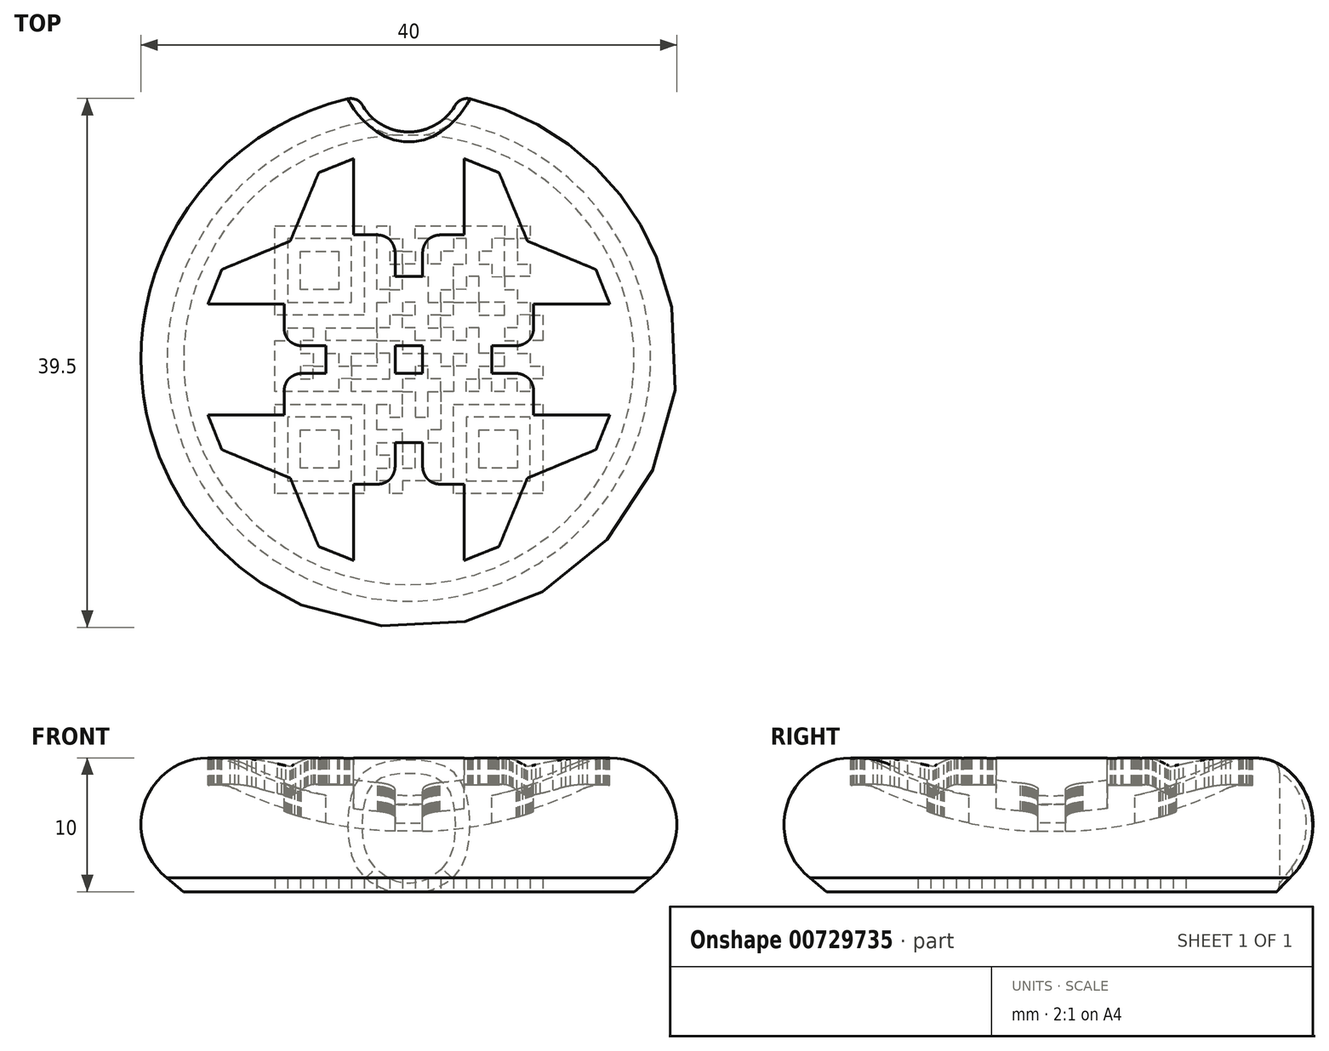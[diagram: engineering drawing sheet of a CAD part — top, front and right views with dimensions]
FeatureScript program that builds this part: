
annotation { "Feature Type Name" : "Feature", "Feature Type Description" : "" }
export const myFeature = defineFeature(function(context is Context, id is Id, definition is map)
    precondition{}
    {
        {
            var Q0;
            Q0=qCreatedBy(makeId("Front.planeOp"),FACE);
            var sketch = newSketch(context, id + "F0", { "sketchPlane" : qUnion([Q0])});
            skArc(sketch, "E0", {"start": v(-12.79, 9.48) * mm, "mid": v(-6.57, 7.26) * mm, "end": v(0, 6.5) * mm});
            skArc(sketch, "E1", {"start": v(-12.79, 9.48) * mm, "mid": v(-19.87, 6.14) * mm, "end": v(-15, 0) * mm});
            skLineSegment(sketch, "E2", {"start": v(0, 0) * mm, "end": v(-15, 0) * mm});
            skLineSegment(sketch, "E3", {"start": v(0, 0) * mm, "end": v(0, 6.5) * mm});
            skLineSegment(sketch, "E4", {"start": v(-18.21, 1.17) * mm, "end": v(-16.82, 0) * mm});
            skLineSegment(sketch, "E5", {"start": v(-16.82, 0) * mm, "end": v(-15, 0) * mm});
            skSolve(sketch);
        }
        {
            var Q0;
            Q0=qSketchRegion(id+"F0",true);
            var Q1;
            Q1=sQuery(id+"F0.wireOp",EDGE,"E3");
            revolve(context, id + "F1", {"surfaceOperationType" : NewSurfaceOperationType.NEW, "entities" : qUnion([Q0]), "axis" : qUnion([Q1]), "revolveType" : RevolveType.FULL});
        }
        {
            var Q0;
            Q0=qCreatedBy(makeId("Top.planeOp"),FACE);
            cPlane(context, id + "F2", {"entities" : qUnion([Q0]), "cplaneType" : CPlaneType.OFFSET, "offset" : 15 * mm, "width" : 150 * mm, "height" : 150 * mm});
        }
        {
            var Q0;
            Q0=qCreatedBy(id+"F2.planeOp",FACE);
            var sketch = newSketch(context, id + "F3", { "sketchPlane" : qUnion([Q0])});
            skLineSegment(sketch, "E6", {"start": v(9.31, -4.14) * mm, "end": v(9.31, -4.02) * mm});
            skLineSegment(sketch, "E7", {"start": v(9.31, -4.02) * mm, "end": v(9.31, -3.91) * mm});
            skLineSegment(sketch, "E8", {"start": v(9.31, -3.91) * mm, "end": v(9.31, -3.8) * mm});
            skLineSegment(sketch, "E9", {"start": v(9.31, -3.8) * mm, "end": v(9.31, -3.69) * mm});
            skLineSegment(sketch, "E10", {"start": v(9.31, -3.69) * mm, "end": v(9.31, -3.57) * mm});
            skLineSegment(sketch, "E11", {"start": v(9.31, -3.57) * mm, "end": v(9.31, -3.46) * mm});
            skLineSegment(sketch, "E12", {"start": v(9.31, -3.46) * mm, "end": v(9.31, -3.35) * mm});
            skLineSegment(sketch, "E13", {"start": v(9.31, -3.35) * mm, "end": v(9.31, -3.23) * mm});
            skLineSegment(sketch, "E14", {"start": v(9.31, -3.23) * mm, "end": v(9.31, -3.12) * mm});
            skLineSegment(sketch, "E15", {"start": v(9.31, -3.12) * mm, "end": v(9.31, -3) * mm});
            skLineSegment(sketch, "E16", {"start": v(9.31, -3) * mm, "end": v(9.31, -2.9) * mm});
            skLineSegment(sketch, "E17", {"start": v(9.31, -2.9) * mm, "end": v(9.31, -2.78) * mm});
            skLineSegment(sketch, "E18", {"start": v(9.31, -2.78) * mm, "end": v(9.31, -2.67) * mm});
            skLineSegment(sketch, "E19", {"start": v(9.31, -2.67) * mm, "end": v(9.31, -2.55) * mm});
            skLineSegment(sketch, "E20", {"start": v(9.31, -2.55) * mm, "end": v(9.31, -2.44) * mm});
            skLineSegment(sketch, "E21", {"start": v(9.31, -2.44) * mm, "end": v(9.31, -2.33) * mm});
            skLineSegment(sketch, "E22", {"start": v(9.31, -2.33) * mm, "end": v(9.3, -2.2) * mm});
            skLineSegment(sketch, "E23", {"start": v(9.3, -2.2) * mm, "end": v(9.28, -2.07) * mm});
            skLineSegment(sketch, "E24", {"start": v(9.28, -2.07) * mm, "end": v(9.25, -1.94) * mm});
            skLineSegment(sketch, "E25", {"start": v(9.25, -1.94) * mm, "end": v(9.2, -1.82) * mm});
            skLineSegment(sketch, "E26", {"start": v(9.2, -1.82) * mm, "end": v(9.15, -1.71) * mm});
            skLineSegment(sketch, "E27", {"start": v(9.15, -1.71) * mm, "end": v(9.09, -1.6) * mm});
            skLineSegment(sketch, "E28", {"start": v(9.09, -1.6) * mm, "end": v(9.02, -1.5) * mm});
            skLineSegment(sketch, "E29", {"start": v(9.02, -1.5) * mm, "end": v(8.93, -1.41) * mm});
            skLineSegment(sketch, "E30", {"start": v(8.93, -1.41) * mm, "end": v(8.84, -1.33) * mm});
            skLineSegment(sketch, "E31", {"start": v(8.84, -1.33) * mm, "end": v(8.74, -1.26) * mm});
            skLineSegment(sketch, "E32", {"start": v(8.74, -1.26) * mm, "end": v(8.63, -1.2) * mm});
            skLineSegment(sketch, "E33", {"start": v(8.63, -1.2) * mm, "end": v(8.52, -1.14) * mm});
            skLineSegment(sketch, "E34", {"start": v(8.52, -1.14) * mm, "end": v(8.4, -1.1) * mm});
            skLineSegment(sketch, "E35", {"start": v(8.4, -1.1) * mm, "end": v(8.28, -1.06) * mm});
            skLineSegment(sketch, "E36", {"start": v(8.28, -1.06) * mm, "end": v(8.15, -1.04) * mm});
            skLineSegment(sketch, "E37", {"start": v(8.15, -1.04) * mm, "end": v(8.02, -1.03) * mm});
            skLineSegment(sketch, "E38", {"start": v(8.02, -1.03) * mm, "end": v(7.9, -1.03) * mm});
            skLineSegment(sketch, "E39", {"start": v(7.9, -1.03) * mm, "end": v(7.8, -1.03) * mm});
            skLineSegment(sketch, "E40", {"start": v(7.8, -1.03) * mm, "end": v(7.68, -1.03) * mm});
            skLineSegment(sketch, "E41", {"start": v(7.68, -1.03) * mm, "end": v(7.56, -1.03) * mm});
            skLineSegment(sketch, "E42", {"start": v(7.56, -1.03) * mm, "end": v(7.45, -1.03) * mm});
            skLineSegment(sketch, "E43", {"start": v(7.45, -1.03) * mm, "end": v(7.34, -1.03) * mm});
            skLineSegment(sketch, "E44", {"start": v(7.34, -1.03) * mm, "end": v(7.23, -1.03) * mm});
            skLineSegment(sketch, "E45", {"start": v(7.23, -1.03) * mm, "end": v(7.11, -1.03) * mm});
            skLineSegment(sketch, "E46", {"start": v(7.11, -1.03) * mm, "end": v(7, -1.03) * mm});
            skLineSegment(sketch, "E47", {"start": v(7, -1.03) * mm, "end": v(6.89, -1.03) * mm});
            skLineSegment(sketch, "E48", {"start": v(6.89, -1.03) * mm, "end": v(6.77, -1.03) * mm});
            skLineSegment(sketch, "E49", {"start": v(6.77, -1.03) * mm, "end": v(6.66, -1.03) * mm});
            skLineSegment(sketch, "E50", {"start": v(6.66, -1.03) * mm, "end": v(6.55, -1.03) * mm});
            skLineSegment(sketch, "E51", {"start": v(6.55, -1.03) * mm, "end": v(6.43, -1.03) * mm});
            skLineSegment(sketch, "E52", {"start": v(6.43, -1.03) * mm, "end": v(6.32, -1.03) * mm});
            skLineSegment(sketch, "E53", {"start": v(6.32, -1.03) * mm, "end": v(6.2, -1.03) * mm});
            skLineSegment(sketch, "E54", {"start": v(6.2, -1.03) * mm, "end": v(6.2, -0.97) * mm});
            skLineSegment(sketch, "E55", {"start": v(6.2, -0.97) * mm, "end": v(6.2, -0.9) * mm});
            skLineSegment(sketch, "E56", {"start": v(6.2, -0.9) * mm, "end": v(6.2, -0.84) * mm});
            skLineSegment(sketch, "E57", {"start": v(6.2, -0.84) * mm, "end": v(6.2, -0.78) * mm});
            skLineSegment(sketch, "E58", {"start": v(6.2, -0.78) * mm, "end": v(6.2, -0.71) * mm});
            skLineSegment(sketch, "E59", {"start": v(6.2, -0.71) * mm, "end": v(6.2, -0.65) * mm});
            skLineSegment(sketch, "E60", {"start": v(6.2, -0.65) * mm, "end": v(6.2, -0.58) * mm});
            skLineSegment(sketch, "E61", {"start": v(6.2, -0.58) * mm, "end": v(6.2, -0.52) * mm});
            skLineSegment(sketch, "E62", {"start": v(6.2, -0.52) * mm, "end": v(6.2, -0.45) * mm});
            skLineSegment(sketch, "E63", {"start": v(6.2, -0.45) * mm, "end": v(6.2, -0.39) * mm});
            skLineSegment(sketch, "E64", {"start": v(6.2, -0.39) * mm, "end": v(6.2, -0.32) * mm});
            skLineSegment(sketch, "E65", {"start": v(6.2, -0.32) * mm, "end": v(6.2, -0.26) * mm});
            skLineSegment(sketch, "E66", {"start": v(6.2, -0.26) * mm, "end": v(6.2, -0.2) * mm});
            skLineSegment(sketch, "E67", {"start": v(6.2, -0.2) * mm, "end": v(6.2, -0.13) * mm});
            skLineSegment(sketch, "E68", {"start": v(6.2, -0.13) * mm, "end": v(6.2, -0.06) * mm});
            skLineSegment(sketch, "E69", {"start": v(6.2, -0.06) * mm, "end": v(6.2, 0) * mm});
            skLineSegment(sketch, "E70", {"start": v(6.2, 0) * mm, "end": v(6.2, 0.06) * mm});
            skLineSegment(sketch, "E71", {"start": v(6.2, 0.06) * mm, "end": v(6.2, 0.13) * mm});
            skLineSegment(sketch, "E72", {"start": v(6.2, 0.13) * mm, "end": v(6.2, 0.2) * mm});
            skLineSegment(sketch, "E73", {"start": v(6.2, 0.2) * mm, "end": v(6.2, 0.26) * mm});
            skLineSegment(sketch, "E74", {"start": v(6.2, 0.26) * mm, "end": v(6.2, 0.32) * mm});
            skLineSegment(sketch, "E75", {"start": v(6.2, 0.32) * mm, "end": v(6.2, 0.39) * mm});
            skLineSegment(sketch, "E76", {"start": v(6.2, 0.39) * mm, "end": v(6.2, 0.45) * mm});
            skLineSegment(sketch, "E77", {"start": v(6.2, 0.45) * mm, "end": v(6.2, 0.52) * mm});
            skLineSegment(sketch, "E78", {"start": v(6.2, 0.52) * mm, "end": v(6.2, 0.58) * mm});
            skLineSegment(sketch, "E79", {"start": v(6.2, 0.58) * mm, "end": v(6.2, 0.65) * mm});
            skLineSegment(sketch, "E80", {"start": v(6.2, 0.65) * mm, "end": v(6.2, 0.71) * mm});
            skLineSegment(sketch, "E81", {"start": v(6.2, 0.71) * mm, "end": v(6.2, 0.78) * mm});
            skLineSegment(sketch, "E82", {"start": v(6.2, 0.78) * mm, "end": v(6.2, 0.84) * mm});
            skLineSegment(sketch, "E83", {"start": v(6.2, 0.84) * mm, "end": v(6.2, 0.9) * mm});
            skLineSegment(sketch, "E84", {"start": v(6.2, 0.9) * mm, "end": v(6.2, 0.97) * mm});
            skLineSegment(sketch, "E85", {"start": v(6.2, 0.97) * mm, "end": v(6.2, 1.03) * mm});
            skLineSegment(sketch, "E86", {"start": v(6.2, 1.03) * mm, "end": v(6.32, 1.03) * mm});
            skLineSegment(sketch, "E87", {"start": v(6.32, 1.03) * mm, "end": v(6.43, 1.03) * mm});
            skLineSegment(sketch, "E88", {"start": v(6.43, 1.03) * mm, "end": v(6.55, 1.03) * mm});
            skLineSegment(sketch, "E89", {"start": v(6.55, 1.03) * mm, "end": v(6.66, 1.03) * mm});
            skLineSegment(sketch, "E90", {"start": v(6.66, 1.03) * mm, "end": v(6.77, 1.03) * mm});
            skLineSegment(sketch, "E91", {"start": v(6.77, 1.03) * mm, "end": v(6.89, 1.03) * mm});
            skLineSegment(sketch, "E92", {"start": v(6.89, 1.03) * mm, "end": v(7, 1.03) * mm});
            skLineSegment(sketch, "E93", {"start": v(7, 1.03) * mm, "end": v(7.11, 1.03) * mm});
            skLineSegment(sketch, "E94", {"start": v(7.11, 1.03) * mm, "end": v(7.23, 1.03) * mm});
            skLineSegment(sketch, "E95", {"start": v(7.23, 1.03) * mm, "end": v(7.34, 1.03) * mm});
            skLineSegment(sketch, "E96", {"start": v(7.34, 1.03) * mm, "end": v(7.45, 1.03) * mm});
            skLineSegment(sketch, "E97", {"start": v(7.45, 1.03) * mm, "end": v(7.56, 1.03) * mm});
            skLineSegment(sketch, "E98", {"start": v(7.56, 1.03) * mm, "end": v(7.68, 1.03) * mm});
            skLineSegment(sketch, "E99", {"start": v(7.68, 1.03) * mm, "end": v(7.8, 1.03) * mm});
            skLineSegment(sketch, "E100", {"start": v(7.8, 1.03) * mm, "end": v(7.9, 1.03) * mm});
            skLineSegment(sketch, "E101", {"start": v(7.9, 1.03) * mm, "end": v(8.02, 1.03) * mm});
            skLineSegment(sketch, "E102", {"start": v(8.02, 1.03) * mm, "end": v(8.15, 1.04) * mm});
            skLineSegment(sketch, "E103", {"start": v(8.15, 1.04) * mm, "end": v(8.28, 1.06) * mm});
            skLineSegment(sketch, "E104", {"start": v(8.28, 1.06) * mm, "end": v(8.4, 1.1) * mm});
            skLineSegment(sketch, "E105", {"start": v(8.4, 1.1) * mm, "end": v(8.52, 1.14) * mm});
            skLineSegment(sketch, "E106", {"start": v(8.52, 1.14) * mm, "end": v(8.63, 1.2) * mm});
            skLineSegment(sketch, "E107", {"start": v(8.63, 1.2) * mm, "end": v(8.74, 1.26) * mm});
            skLineSegment(sketch, "E108", {"start": v(8.74, 1.26) * mm, "end": v(8.84, 1.33) * mm});
            skLineSegment(sketch, "E109", {"start": v(8.84, 1.33) * mm, "end": v(8.93, 1.41) * mm});
            skLineSegment(sketch, "E110", {"start": v(8.93, 1.41) * mm, "end": v(9.02, 1.5) * mm});
            skLineSegment(sketch, "E111", {"start": v(9.02, 1.5) * mm, "end": v(9.09, 1.6) * mm});
            skLineSegment(sketch, "E112", {"start": v(9.09, 1.6) * mm, "end": v(9.15, 1.71) * mm});
            skLineSegment(sketch, "E113", {"start": v(9.15, 1.71) * mm, "end": v(9.2, 1.82) * mm});
            skLineSegment(sketch, "E114", {"start": v(9.2, 1.82) * mm, "end": v(9.25, 1.94) * mm});
            skLineSegment(sketch, "E115", {"start": v(9.25, 1.94) * mm, "end": v(9.28, 2.07) * mm});
            skLineSegment(sketch, "E116", {"start": v(9.28, 2.07) * mm, "end": v(9.3, 2.2) * mm});
            skLineSegment(sketch, "E117", {"start": v(9.3, 2.2) * mm, "end": v(9.31, 2.33) * mm});
            skLineSegment(sketch, "E118", {"start": v(9.31, 2.33) * mm, "end": v(9.31, 2.44) * mm});
            skLineSegment(sketch, "E119", {"start": v(9.31, 2.44) * mm, "end": v(9.31, 2.55) * mm});
            skLineSegment(sketch, "E120", {"start": v(9.31, 2.55) * mm, "end": v(9.31, 2.67) * mm});
            skLineSegment(sketch, "E121", {"start": v(9.31, 2.67) * mm, "end": v(9.31, 2.78) * mm});
            skLineSegment(sketch, "E122", {"start": v(9.31, 2.78) * mm, "end": v(9.31, 2.9) * mm});
            skLineSegment(sketch, "E123", {"start": v(9.31, 2.9) * mm, "end": v(9.31, 3) * mm});
            skLineSegment(sketch, "E124", {"start": v(9.31, 3) * mm, "end": v(9.31, 3.12) * mm});
            skLineSegment(sketch, "E125", {"start": v(9.31, 3.12) * mm, "end": v(9.31, 3.23) * mm});
            skLineSegment(sketch, "E126", {"start": v(9.31, 3.23) * mm, "end": v(9.31, 3.35) * mm});
            skLineSegment(sketch, "E127", {"start": v(9.31, 3.35) * mm, "end": v(9.31, 3.46) * mm});
            skLineSegment(sketch, "E128", {"start": v(9.31, 3.46) * mm, "end": v(9.31, 3.57) * mm});
            skLineSegment(sketch, "E129", {"start": v(9.31, 3.57) * mm, "end": v(9.31, 3.69) * mm});
            skLineSegment(sketch, "E130", {"start": v(9.31, 3.69) * mm, "end": v(9.31, 3.8) * mm});
            skLineSegment(sketch, "E131", {"start": v(9.31, 3.8) * mm, "end": v(9.31, 3.91) * mm});
            skLineSegment(sketch, "E132", {"start": v(9.31, 3.91) * mm, "end": v(9.31, 4.02) * mm});
            skLineSegment(sketch, "E133", {"start": v(9.31, 4.02) * mm, "end": v(9.31, 4.14) * mm});
            skLineSegment(sketch, "E134", {"start": v(9.31, 4.14) * mm, "end": v(9.44, 4.14) * mm});
            skLineSegment(sketch, "E135", {"start": v(9.44, 4.14) * mm, "end": v(9.57, 4.14) * mm});
            skLineSegment(sketch, "E136", {"start": v(9.57, 4.14) * mm, "end": v(9.7, 4.14) * mm});
            skLineSegment(sketch, "E137", {"start": v(9.7, 4.14) * mm, "end": v(9.83, 4.14) * mm});
            skLineSegment(sketch, "E138", {"start": v(9.83, 4.14) * mm, "end": v(9.96, 4.14) * mm});
            skLineSegment(sketch, "E139", {"start": v(9.96, 4.14) * mm, "end": v(10.09, 4.14) * mm});
            skLineSegment(sketch, "E140", {"start": v(10.09, 4.14) * mm, "end": v(10.22, 4.14) * mm});
            skLineSegment(sketch, "E141", {"start": v(10.22, 4.14) * mm, "end": v(10.34, 4.14) * mm});
            skLineSegment(sketch, "E142", {"start": v(10.34, 4.14) * mm, "end": v(10.47, 4.14) * mm});
            skLineSegment(sketch, "E143", {"start": v(10.47, 4.14) * mm, "end": v(10.6, 4.14) * mm});
            skLineSegment(sketch, "E144", {"start": v(10.6, 4.14) * mm, "end": v(10.73, 4.14) * mm});
            skLineSegment(sketch, "E145", {"start": v(10.73, 4.14) * mm, "end": v(10.86, 4.14) * mm});
            skLineSegment(sketch, "E146", {"start": v(10.86, 4.14) * mm, "end": v(11, 4.14) * mm});
            skLineSegment(sketch, "E147", {"start": v(11, 4.14) * mm, "end": v(11.12, 4.14) * mm});
            skLineSegment(sketch, "E148", {"start": v(11.12, 4.14) * mm, "end": v(11.25, 4.14) * mm});
            skLineSegment(sketch, "E149", {"start": v(11.25, 4.14) * mm, "end": v(11.38, 4.14) * mm});
            skLineSegment(sketch, "E150", {"start": v(11.38, 4.14) * mm, "end": v(11.6, 4.14) * mm});
            skLineSegment(sketch, "E151", {"start": v(11.6, 4.14) * mm, "end": v(11.83, 4.14) * mm});
            skLineSegment(sketch, "E152", {"start": v(11.83, 4.14) * mm, "end": v(12.06, 4.14) * mm});
            skLineSegment(sketch, "E153", {"start": v(12.06, 4.14) * mm, "end": v(12.28, 4.14) * mm});
            skLineSegment(sketch, "E154", {"start": v(12.28, 4.14) * mm, "end": v(12.51, 4.14) * mm});
            skLineSegment(sketch, "E155", {"start": v(12.51, 4.14) * mm, "end": v(12.74, 4.14) * mm});
            skLineSegment(sketch, "E156", {"start": v(12.74, 4.14) * mm, "end": v(12.96, 4.14) * mm});
            skLineSegment(sketch, "E157", {"start": v(12.96, 4.14) * mm, "end": v(13.19, 4.14) * mm});
            skLineSegment(sketch, "E158", {"start": v(13.19, 4.14) * mm, "end": v(13.42, 4.14) * mm});
            skLineSegment(sketch, "E159", {"start": v(13.42, 4.14) * mm, "end": v(13.64, 4.14) * mm});
            skLineSegment(sketch, "E160", {"start": v(13.64, 4.14) * mm, "end": v(13.87, 4.14) * mm});
            skLineSegment(sketch, "E161", {"start": v(13.87, 4.14) * mm, "end": v(14.1, 4.14) * mm});
            skLineSegment(sketch, "E162", {"start": v(14.1, 4.14) * mm, "end": v(14.32, 4.14) * mm});
            skLineSegment(sketch, "E163", {"start": v(14.32, 4.14) * mm, "end": v(14.55, 4.14) * mm});
            skLineSegment(sketch, "E164", {"start": v(14.55, 4.14) * mm, "end": v(14.77, 4.14) * mm});
            skLineSegment(sketch, "E165", {"start": v(14.77, 4.14) * mm, "end": v(15, 4.14) * mm});
            skLineSegment(sketch, "E166", {"start": v(15, 4.14) * mm, "end": v(14.95, 4.27) * mm});
            skLineSegment(sketch, "E167", {"start": v(14.95, 4.27) * mm, "end": v(14.9, 4.4) * mm});
            skLineSegment(sketch, "E168", {"start": v(14.9, 4.4) * mm, "end": v(14.84, 4.53) * mm});
            skLineSegment(sketch, "E169", {"start": v(14.84, 4.53) * mm, "end": v(14.8, 4.66) * mm});
            skLineSegment(sketch, "E170", {"start": v(14.8, 4.66) * mm, "end": v(14.74, 4.78) * mm});
            skLineSegment(sketch, "E171", {"start": v(14.74, 4.78) * mm, "end": v(14.69, 4.91) * mm});
            skLineSegment(sketch, "E172", {"start": v(14.69, 4.91) * mm, "end": v(14.64, 5.04) * mm});
            skLineSegment(sketch, "E173", {"start": v(14.64, 5.04) * mm, "end": v(14.59, 5.17) * mm});
            skLineSegment(sketch, "E174", {"start": v(14.59, 5.17) * mm, "end": v(14.53, 5.3) * mm});
            skLineSegment(sketch, "E175", {"start": v(14.53, 5.3) * mm, "end": v(14.48, 5.43) * mm});
            skLineSegment(sketch, "E176", {"start": v(14.48, 5.43) * mm, "end": v(14.43, 5.56) * mm});
            skLineSegment(sketch, "E177", {"start": v(14.43, 5.56) * mm, "end": v(14.38, 5.69) * mm});
            skLineSegment(sketch, "E178", {"start": v(14.38, 5.69) * mm, "end": v(14.33, 5.82) * mm});
            skLineSegment(sketch, "E179", {"start": v(14.33, 5.82) * mm, "end": v(14.28, 5.95) * mm});
            skLineSegment(sketch, "E180", {"start": v(14.28, 5.95) * mm, "end": v(14.22, 6.08) * mm});
            skLineSegment(sketch, "E181", {"start": v(14.22, 6.08) * mm, "end": v(14.17, 6.2) * mm});
            skLineSegment(sketch, "E182", {"start": v(14.17, 6.2) * mm, "end": v(14.16, 6.24) * mm});
            skLineSegment(sketch, "E183", {"start": v(14.16, 6.24) * mm, "end": v(14.15, 6.27) * mm});
            skLineSegment(sketch, "E184", {"start": v(14.15, 6.27) * mm, "end": v(14.13, 6.3) * mm});
            skLineSegment(sketch, "E185", {"start": v(14.13, 6.3) * mm, "end": v(14.12, 6.34) * mm});
            skLineSegment(sketch, "E186", {"start": v(14.12, 6.34) * mm, "end": v(14.1, 6.37) * mm});
            skLineSegment(sketch, "E187", {"start": v(14.1, 6.37) * mm, "end": v(14.1, 6.4) * mm});
            skLineSegment(sketch, "E188", {"start": v(14.1, 6.4) * mm, "end": v(14.08, 6.43) * mm});
            skLineSegment(sketch, "E189", {"start": v(14.08, 6.43) * mm, "end": v(14.07, 6.47) * mm});
            skLineSegment(sketch, "E190", {"start": v(14.07, 6.47) * mm, "end": v(14.06, 6.5) * mm});
            skLineSegment(sketch, "E191", {"start": v(14.06, 6.5) * mm, "end": v(14.04, 6.53) * mm});
            skLineSegment(sketch, "E192", {"start": v(14.04, 6.53) * mm, "end": v(14.03, 6.56) * mm});
            skLineSegment(sketch, "E193", {"start": v(14.03, 6.56) * mm, "end": v(14.02, 6.6) * mm});
            skLineSegment(sketch, "E194", {"start": v(14.02, 6.6) * mm, "end": v(14, 6.63) * mm});
            skLineSegment(sketch, "E195", {"start": v(14, 6.63) * mm, "end": v(14, 6.66) * mm});
            skLineSegment(sketch, "E196", {"start": v(14, 6.66) * mm, "end": v(13.98, 6.7) * mm});
            skLineSegment(sketch, "E197", {"start": v(13.98, 6.7) * mm, "end": v(13.97, 6.72) * mm});
            skLineSegment(sketch, "E198", {"start": v(13.97, 6.72) * mm, "end": v(13.65, 6.86) * mm});
            skLineSegment(sketch, "E199", {"start": v(13.65, 6.86) * mm, "end": v(13.33, 7) * mm});
            skLineSegment(sketch, "E200", {"start": v(13.33, 7) * mm, "end": v(13, 7.12) * mm});
            skLineSegment(sketch, "E201", {"start": v(13, 7.12) * mm, "end": v(12.69, 7.26) * mm});
            skLineSegment(sketch, "E202", {"start": v(12.69, 7.26) * mm, "end": v(12.37, 7.39) * mm});
            skLineSegment(sketch, "E203", {"start": v(12.37, 7.39) * mm, "end": v(12.05, 7.52) * mm});
            skLineSegment(sketch, "E204", {"start": v(12.05, 7.52) * mm, "end": v(11.73, 7.66) * mm});
            skLineSegment(sketch, "E205", {"start": v(11.73, 7.66) * mm, "end": v(11.4, 7.79) * mm});
            skLineSegment(sketch, "E206", {"start": v(11.4, 7.79) * mm, "end": v(11.1, 7.92) * mm});
            skLineSegment(sketch, "E207", {"start": v(11.1, 7.92) * mm, "end": v(10.77, 8.06) * mm});
            skLineSegment(sketch, "E208", {"start": v(10.77, 8.06) * mm, "end": v(10.45, 8.19) * mm});
            skLineSegment(sketch, "E209", {"start": v(10.45, 8.19) * mm, "end": v(10.13, 8.32) * mm});
            skLineSegment(sketch, "E210", {"start": v(10.13, 8.32) * mm, "end": v(9.81, 8.45) * mm});
            skLineSegment(sketch, "E211", {"start": v(9.81, 8.45) * mm, "end": v(9.5, 8.59) * mm});
            skLineSegment(sketch, "E212", {"start": v(9.5, 8.59) * mm, "end": v(9.17, 8.72) * mm});
            skLineSegment(sketch, "E213", {"start": v(9.17, 8.72) * mm, "end": v(8.85, 8.85) * mm});
            skLineSegment(sketch, "E214", {"start": v(8.85, 8.85) * mm, "end": v(8.72, 9.17) * mm});
            skLineSegment(sketch, "E215", {"start": v(8.72, 9.17) * mm, "end": v(8.59, 9.5) * mm});
            skLineSegment(sketch, "E216", {"start": v(8.59, 9.5) * mm, "end": v(8.45, 9.81) * mm});
            skLineSegment(sketch, "E217", {"start": v(8.45, 9.81) * mm, "end": v(8.32, 10.13) * mm});
            skLineSegment(sketch, "E218", {"start": v(8.32, 10.13) * mm, "end": v(8.19, 10.45) * mm});
            skLineSegment(sketch, "E219", {"start": v(8.19, 10.45) * mm, "end": v(8.06, 10.77) * mm});
            skLineSegment(sketch, "E220", {"start": v(8.06, 10.77) * mm, "end": v(7.92, 11.1) * mm});
            skLineSegment(sketch, "E221", {"start": v(7.92, 11.1) * mm, "end": v(7.79, 11.4) * mm});
            skLineSegment(sketch, "E222", {"start": v(7.79, 11.4) * mm, "end": v(7.66, 11.73) * mm});
            skLineSegment(sketch, "E223", {"start": v(7.66, 11.73) * mm, "end": v(7.52, 12.05) * mm});
            skLineSegment(sketch, "E224", {"start": v(7.52, 12.05) * mm, "end": v(7.39, 12.37) * mm});
            skLineSegment(sketch, "E225", {"start": v(7.39, 12.37) * mm, "end": v(7.26, 12.69) * mm});
            skLineSegment(sketch, "E226", {"start": v(7.26, 12.69) * mm, "end": v(7.12, 13) * mm});
            skLineSegment(sketch, "E227", {"start": v(7.12, 13) * mm, "end": v(7, 13.33) * mm});
            skLineSegment(sketch, "E228", {"start": v(7, 13.33) * mm, "end": v(6.86, 13.65) * mm});
            skLineSegment(sketch, "E229", {"start": v(6.86, 13.65) * mm, "end": v(6.72, 13.97) * mm});
            skLineSegment(sketch, "E230", {"start": v(6.72, 13.97) * mm, "end": v(6.7, 13.98) * mm});
            skLineSegment(sketch, "E231", {"start": v(6.7, 13.98) * mm, "end": v(6.66, 14) * mm});
            skLineSegment(sketch, "E232", {"start": v(6.66, 14) * mm, "end": v(6.63, 14) * mm});
            skLineSegment(sketch, "E233", {"start": v(6.63, 14) * mm, "end": v(6.6, 14.02) * mm});
            skLineSegment(sketch, "E234", {"start": v(6.6, 14.02) * mm, "end": v(6.56, 14.03) * mm});
            skLineSegment(sketch, "E235", {"start": v(6.56, 14.03) * mm, "end": v(6.53, 14.04) * mm});
            skLineSegment(sketch, "E236", {"start": v(6.53, 14.04) * mm, "end": v(6.5, 14.06) * mm});
            skLineSegment(sketch, "E237", {"start": v(6.5, 14.06) * mm, "end": v(6.47, 14.07) * mm});
            skLineSegment(sketch, "E238", {"start": v(6.47, 14.07) * mm, "end": v(6.43, 14.08) * mm});
            skLineSegment(sketch, "E239", {"start": v(6.43, 14.08) * mm, "end": v(6.4, 14.1) * mm});
            skLineSegment(sketch, "E240", {"start": v(6.4, 14.1) * mm, "end": v(6.37, 14.1) * mm});
            skLineSegment(sketch, "E241", {"start": v(6.37, 14.1) * mm, "end": v(6.34, 14.12) * mm});
            skLineSegment(sketch, "E242", {"start": v(6.34, 14.12) * mm, "end": v(6.3, 14.13) * mm});
            skLineSegment(sketch, "E243", {"start": v(6.3, 14.13) * mm, "end": v(6.27, 14.15) * mm});
            skLineSegment(sketch, "E244", {"start": v(6.27, 14.15) * mm, "end": v(6.24, 14.16) * mm});
            skLineSegment(sketch, "E245", {"start": v(6.24, 14.16) * mm, "end": v(6.2, 14.17) * mm});
            skLineSegment(sketch, "E246", {"start": v(6.2, 14.17) * mm, "end": v(6.08, 14.22) * mm});
            skLineSegment(sketch, "E247", {"start": v(6.08, 14.22) * mm, "end": v(5.95, 14.28) * mm});
            skLineSegment(sketch, "E248", {"start": v(5.95, 14.28) * mm, "end": v(5.82, 14.33) * mm});
            skLineSegment(sketch, "E249", {"start": v(5.82, 14.33) * mm, "end": v(5.69, 14.38) * mm});
            skLineSegment(sketch, "E250", {"start": v(5.69, 14.38) * mm, "end": v(5.56, 14.43) * mm});
            skLineSegment(sketch, "E251", {"start": v(5.56, 14.43) * mm, "end": v(5.43, 14.48) * mm});
            skLineSegment(sketch, "E252", {"start": v(5.43, 14.48) * mm, "end": v(5.3, 14.53) * mm});
            skLineSegment(sketch, "E253", {"start": v(5.3, 14.53) * mm, "end": v(5.17, 14.59) * mm});
            skLineSegment(sketch, "E254", {"start": v(5.17, 14.59) * mm, "end": v(5.04, 14.64) * mm});
            skLineSegment(sketch, "E255", {"start": v(5.04, 14.64) * mm, "end": v(4.91, 14.69) * mm});
            skLineSegment(sketch, "E256", {"start": v(4.91, 14.69) * mm, "end": v(4.78, 14.74) * mm});
            skLineSegment(sketch, "E257", {"start": v(4.78, 14.74) * mm, "end": v(4.66, 14.8) * mm});
            skLineSegment(sketch, "E258", {"start": v(4.66, 14.8) * mm, "end": v(4.53, 14.84) * mm});
            skLineSegment(sketch, "E259", {"start": v(4.53, 14.84) * mm, "end": v(4.4, 14.9) * mm});
            skLineSegment(sketch, "E260", {"start": v(4.4, 14.9) * mm, "end": v(4.27, 14.95) * mm});
            skLineSegment(sketch, "E261", {"start": v(4.27, 14.95) * mm, "end": v(4.14, 15) * mm});
            skLineSegment(sketch, "E262", {"start": v(4.14, 15) * mm, "end": v(4.14, 14.77) * mm});
            skLineSegment(sketch, "E263", {"start": v(4.14, 14.77) * mm, "end": v(4.14, 14.55) * mm});
            skLineSegment(sketch, "E264", {"start": v(4.14, 14.55) * mm, "end": v(4.14, 14.32) * mm});
            skLineSegment(sketch, "E265", {"start": v(4.14, 14.32) * mm, "end": v(4.14, 14.1) * mm});
            skLineSegment(sketch, "E266", {"start": v(4.14, 14.1) * mm, "end": v(4.14, 13.87) * mm});
            skLineSegment(sketch, "E267", {"start": v(4.14, 13.87) * mm, "end": v(4.14, 13.64) * mm});
            skLineSegment(sketch, "E268", {"start": v(4.14, 13.64) * mm, "end": v(4.14, 13.42) * mm});
            skLineSegment(sketch, "E269", {"start": v(4.14, 13.42) * mm, "end": v(4.14, 13.19) * mm});
            skLineSegment(sketch, "E270", {"start": v(4.14, 13.19) * mm, "end": v(4.14, 12.96) * mm});
            skLineSegment(sketch, "E271", {"start": v(4.14, 12.96) * mm, "end": v(4.14, 12.74) * mm});
            skLineSegment(sketch, "E272", {"start": v(4.14, 12.74) * mm, "end": v(4.14, 12.51) * mm});
            skLineSegment(sketch, "E273", {"start": v(4.14, 12.51) * mm, "end": v(4.14, 12.28) * mm});
            skLineSegment(sketch, "E274", {"start": v(4.14, 12.28) * mm, "end": v(4.14, 12.06) * mm});
            skLineSegment(sketch, "E275", {"start": v(4.14, 12.06) * mm, "end": v(4.14, 11.83) * mm});
            skLineSegment(sketch, "E276", {"start": v(4.14, 11.83) * mm, "end": v(4.14, 11.6) * mm});
            skLineSegment(sketch, "E277", {"start": v(4.14, 11.6) * mm, "end": v(4.14, 11.38) * mm});
            skLineSegment(sketch, "E278", {"start": v(4.14, 11.38) * mm, "end": v(4.14, 11.25) * mm});
            skLineSegment(sketch, "E279", {"start": v(4.14, 11.25) * mm, "end": v(4.14, 11.12) * mm});
            skLineSegment(sketch, "E280", {"start": v(4.14, 11.12) * mm, "end": v(4.14, 11) * mm});
            skLineSegment(sketch, "E281", {"start": v(4.14, 11) * mm, "end": v(4.14, 10.86) * mm});
            skLineSegment(sketch, "E282", {"start": v(4.14, 10.86) * mm, "end": v(4.14, 10.73) * mm});
            skLineSegment(sketch, "E283", {"start": v(4.14, 10.73) * mm, "end": v(4.14, 10.6) * mm});
            skLineSegment(sketch, "E284", {"start": v(4.14, 10.6) * mm, "end": v(4.14, 10.47) * mm});
            skLineSegment(sketch, "E285", {"start": v(4.14, 10.47) * mm, "end": v(4.14, 10.34) * mm});
            skLineSegment(sketch, "E286", {"start": v(4.14, 10.34) * mm, "end": v(4.14, 10.22) * mm});
            skLineSegment(sketch, "E287", {"start": v(4.14, 10.22) * mm, "end": v(4.14, 10.09) * mm});
            skLineSegment(sketch, "E288", {"start": v(4.14, 10.09) * mm, "end": v(4.14, 9.96) * mm});
            skLineSegment(sketch, "E289", {"start": v(4.14, 9.96) * mm, "end": v(4.14, 9.83) * mm});
            skLineSegment(sketch, "E290", {"start": v(4.14, 9.83) * mm, "end": v(4.14, 9.7) * mm});
            skLineSegment(sketch, "E291", {"start": v(4.14, 9.7) * mm, "end": v(4.14, 9.57) * mm});
            skLineSegment(sketch, "E292", {"start": v(4.14, 9.57) * mm, "end": v(4.14, 9.44) * mm});
            skLineSegment(sketch, "E293", {"start": v(4.14, 9.44) * mm, "end": v(4.14, 9.31) * mm});
            skLineSegment(sketch, "E294", {"start": v(4.14, 9.31) * mm, "end": v(4.02, 9.31) * mm});
            skLineSegment(sketch, "E295", {"start": v(4.02, 9.31) * mm, "end": v(3.91, 9.31) * mm});
            skLineSegment(sketch, "E296", {"start": v(3.91, 9.31) * mm, "end": v(3.8, 9.31) * mm});
            skLineSegment(sketch, "E297", {"start": v(3.8, 9.31) * mm, "end": v(3.69, 9.31) * mm});
            skLineSegment(sketch, "E298", {"start": v(3.69, 9.31) * mm, "end": v(3.57, 9.31) * mm});
            skLineSegment(sketch, "E299", {"start": v(3.57, 9.31) * mm, "end": v(3.46, 9.31) * mm});
            skLineSegment(sketch, "E300", {"start": v(3.46, 9.31) * mm, "end": v(3.35, 9.31) * mm});
            skLineSegment(sketch, "E301", {"start": v(3.35, 9.31) * mm, "end": v(3.23, 9.31) * mm});
            skLineSegment(sketch, "E302", {"start": v(3.23, 9.31) * mm, "end": v(3.12, 9.31) * mm});
            skLineSegment(sketch, "E303", {"start": v(3.12, 9.31) * mm, "end": v(3, 9.31) * mm});
            skLineSegment(sketch, "E304", {"start": v(3, 9.31) * mm, "end": v(2.9, 9.31) * mm});
            skLineSegment(sketch, "E305", {"start": v(2.9, 9.31) * mm, "end": v(2.78, 9.31) * mm});
            skLineSegment(sketch, "E306", {"start": v(2.78, 9.31) * mm, "end": v(2.67, 9.31) * mm});
            skLineSegment(sketch, "E307", {"start": v(2.67, 9.31) * mm, "end": v(2.55, 9.31) * mm});
            skLineSegment(sketch, "E308", {"start": v(2.55, 9.31) * mm, "end": v(2.44, 9.31) * mm});
            skLineSegment(sketch, "E309", {"start": v(2.44, 9.31) * mm, "end": v(2.33, 9.31) * mm});
            skLineSegment(sketch, "E310", {"start": v(2.33, 9.31) * mm, "end": v(2.2, 9.3) * mm});
            skLineSegment(sketch, "E311", {"start": v(2.2, 9.3) * mm, "end": v(2.07, 9.28) * mm});
            skLineSegment(sketch, "E312", {"start": v(2.07, 9.28) * mm, "end": v(1.94, 9.25) * mm});
            skLineSegment(sketch, "E313", {"start": v(1.94, 9.25) * mm, "end": v(1.82, 9.2) * mm});
            skLineSegment(sketch, "E314", {"start": v(1.82, 9.2) * mm, "end": v(1.71, 9.15) * mm});
            skLineSegment(sketch, "E315", {"start": v(1.71, 9.15) * mm, "end": v(1.6, 9.09) * mm});
            skLineSegment(sketch, "E316", {"start": v(1.6, 9.09) * mm, "end": v(1.5, 9.02) * mm});
            skLineSegment(sketch, "E317", {"start": v(1.5, 9.02) * mm, "end": v(1.41, 8.93) * mm});
            skLineSegment(sketch, "E318", {"start": v(1.41, 8.93) * mm, "end": v(1.33, 8.84) * mm});
            skLineSegment(sketch, "E319", {"start": v(1.33, 8.84) * mm, "end": v(1.26, 8.74) * mm});
            skLineSegment(sketch, "E320", {"start": v(1.26, 8.74) * mm, "end": v(1.2, 8.63) * mm});
            skLineSegment(sketch, "E321", {"start": v(1.2, 8.63) * mm, "end": v(1.14, 8.52) * mm});
            skLineSegment(sketch, "E322", {"start": v(1.14, 8.52) * mm, "end": v(1.1, 8.4) * mm});
            skLineSegment(sketch, "E323", {"start": v(1.1, 8.4) * mm, "end": v(1.06, 8.28) * mm});
            skLineSegment(sketch, "E324", {"start": v(1.06, 8.28) * mm, "end": v(1.04, 8.15) * mm});
            skLineSegment(sketch, "E325", {"start": v(1.04, 8.15) * mm, "end": v(1.03, 8.02) * mm});
            skLineSegment(sketch, "E326", {"start": v(1.03, 8.02) * mm, "end": v(1.03, 7.9) * mm});
            skLineSegment(sketch, "E327", {"start": v(1.03, 7.9) * mm, "end": v(1.03, 7.8) * mm});
            skLineSegment(sketch, "E328", {"start": v(1.03, 7.8) * mm, "end": v(1.03, 7.68) * mm});
            skLineSegment(sketch, "E329", {"start": v(1.03, 7.68) * mm, "end": v(1.03, 7.56) * mm});
            skLineSegment(sketch, "E330", {"start": v(1.03, 7.56) * mm, "end": v(1.03, 7.45) * mm});
            skLineSegment(sketch, "E331", {"start": v(1.03, 7.45) * mm, "end": v(1.03, 7.34) * mm});
            skLineSegment(sketch, "E332", {"start": v(1.03, 7.34) * mm, "end": v(1.03, 7.23) * mm});
            skLineSegment(sketch, "E333", {"start": v(1.03, 7.23) * mm, "end": v(1.03, 7.11) * mm});
            skLineSegment(sketch, "E334", {"start": v(1.03, 7.11) * mm, "end": v(1.03, 7) * mm});
            skLineSegment(sketch, "E335", {"start": v(1.03, 7) * mm, "end": v(1.03, 6.89) * mm});
            skLineSegment(sketch, "E336", {"start": v(1.03, 6.89) * mm, "end": v(1.03, 6.77) * mm});
            skLineSegment(sketch, "E337", {"start": v(1.03, 6.77) * mm, "end": v(1.03, 6.66) * mm});
            skLineSegment(sketch, "E338", {"start": v(1.03, 6.66) * mm, "end": v(1.03, 6.55) * mm});
            skLineSegment(sketch, "E339", {"start": v(1.03, 6.55) * mm, "end": v(1.03, 6.43) * mm});
            skLineSegment(sketch, "E340", {"start": v(1.03, 6.43) * mm, "end": v(1.03, 6.32) * mm});
            skLineSegment(sketch, "E341", {"start": v(1.03, 6.32) * mm, "end": v(1.03, 6.2) * mm});
            skLineSegment(sketch, "E342", {"start": v(1.03, 6.2) * mm, "end": v(0.97, 6.2) * mm});
            skLineSegment(sketch, "E343", {"start": v(0.97, 6.2) * mm, "end": v(0.9, 6.2) * mm});
            skLineSegment(sketch, "E344", {"start": v(0.9, 6.2) * mm, "end": v(0.84, 6.2) * mm});
            skLineSegment(sketch, "E345", {"start": v(0.84, 6.2) * mm, "end": v(0.78, 6.2) * mm});
            skLineSegment(sketch, "E346", {"start": v(0.78, 6.2) * mm, "end": v(0.71, 6.2) * mm});
            skLineSegment(sketch, "E347", {"start": v(0.71, 6.2) * mm, "end": v(0.65, 6.2) * mm});
            skLineSegment(sketch, "E348", {"start": v(0.65, 6.2) * mm, "end": v(0.58, 6.2) * mm});
            skLineSegment(sketch, "E349", {"start": v(0.58, 6.2) * mm, "end": v(0.52, 6.2) * mm});
            skLineSegment(sketch, "E350", {"start": v(0.52, 6.2) * mm, "end": v(0.45, 6.2) * mm});
            skLineSegment(sketch, "E351", {"start": v(0.45, 6.2) * mm, "end": v(0.39, 6.2) * mm});
            skLineSegment(sketch, "E352", {"start": v(0.39, 6.2) * mm, "end": v(0.32, 6.2) * mm});
            skLineSegment(sketch, "E353", {"start": v(0.32, 6.2) * mm, "end": v(0.26, 6.2) * mm});
            skLineSegment(sketch, "E354", {"start": v(0.26, 6.2) * mm, "end": v(0.2, 6.2) * mm});
            skLineSegment(sketch, "E355", {"start": v(0.2, 6.2) * mm, "end": v(0.13, 6.2) * mm});
            skLineSegment(sketch, "E356", {"start": v(0.13, 6.2) * mm, "end": v(0.06, 6.2) * mm});
            skLineSegment(sketch, "E357", {"start": v(0.06, 6.2) * mm, "end": v(0, 6.2) * mm});
            skLineSegment(sketch, "E358", {"start": v(0, 6.2) * mm, "end": v(-0.06, 6.2) * mm});
            skLineSegment(sketch, "E359", {"start": v(-0.06, 6.2) * mm, "end": v(-0.13, 6.2) * mm});
            skLineSegment(sketch, "E360", {"start": v(-0.13, 6.2) * mm, "end": v(-0.2, 6.2) * mm});
            skLineSegment(sketch, "E361", {"start": v(-0.2, 6.2) * mm, "end": v(-0.26, 6.2) * mm});
            skLineSegment(sketch, "E362", {"start": v(-0.26, 6.2) * mm, "end": v(-0.32, 6.2) * mm});
            skLineSegment(sketch, "E363", {"start": v(-0.32, 6.2) * mm, "end": v(-0.39, 6.2) * mm});
            skLineSegment(sketch, "E364", {"start": v(-0.39, 6.2) * mm, "end": v(-0.45, 6.2) * mm});
            skLineSegment(sketch, "E365", {"start": v(-0.45, 6.2) * mm, "end": v(-0.52, 6.2) * mm});
            skLineSegment(sketch, "E366", {"start": v(-0.52, 6.2) * mm, "end": v(-0.58, 6.2) * mm});
            skLineSegment(sketch, "E367", {"start": v(-0.58, 6.2) * mm, "end": v(-0.65, 6.2) * mm});
            skLineSegment(sketch, "E368", {"start": v(-0.65, 6.2) * mm, "end": v(-0.71, 6.2) * mm});
            skLineSegment(sketch, "E369", {"start": v(-0.71, 6.2) * mm, "end": v(-0.78, 6.2) * mm});
            skLineSegment(sketch, "E370", {"start": v(-0.78, 6.2) * mm, "end": v(-0.84, 6.2) * mm});
            skLineSegment(sketch, "E371", {"start": v(-0.84, 6.2) * mm, "end": v(-0.9, 6.2) * mm});
            skLineSegment(sketch, "E372", {"start": v(-0.9, 6.2) * mm, "end": v(-0.97, 6.2) * mm});
            skLineSegment(sketch, "E373", {"start": v(-0.97, 6.2) * mm, "end": v(-1.03, 6.2) * mm});
            skLineSegment(sketch, "E374", {"start": v(-1.03, 6.2) * mm, "end": v(-1.03, 6.32) * mm});
            skLineSegment(sketch, "E375", {"start": v(-1.03, 6.32) * mm, "end": v(-1.03, 6.43) * mm});
            skLineSegment(sketch, "E376", {"start": v(-1.03, 6.43) * mm, "end": v(-1.03, 6.55) * mm});
            skLineSegment(sketch, "E377", {"start": v(-1.03, 6.55) * mm, "end": v(-1.03, 6.66) * mm});
            skLineSegment(sketch, "E378", {"start": v(-1.03, 6.66) * mm, "end": v(-1.03, 6.77) * mm});
            skLineSegment(sketch, "E379", {"start": v(-1.03, 6.77) * mm, "end": v(-1.03, 6.89) * mm});
            skLineSegment(sketch, "E380", {"start": v(-1.03, 6.89) * mm, "end": v(-1.03, 7) * mm});
            skLineSegment(sketch, "E381", {"start": v(-1.03, 7) * mm, "end": v(-1.03, 7.11) * mm});
            skLineSegment(sketch, "E382", {"start": v(-1.03, 7.11) * mm, "end": v(-1.03, 7.23) * mm});
            skLineSegment(sketch, "E383", {"start": v(-1.03, 7.23) * mm, "end": v(-1.03, 7.34) * mm});
            skLineSegment(sketch, "E384", {"start": v(-1.03, 7.34) * mm, "end": v(-1.03, 7.45) * mm});
            skLineSegment(sketch, "E385", {"start": v(-1.03, 7.45) * mm, "end": v(-1.03, 7.56) * mm});
            skLineSegment(sketch, "E386", {"start": v(-1.03, 7.56) * mm, "end": v(-1.03, 7.68) * mm});
            skLineSegment(sketch, "E387", {"start": v(-1.03, 7.68) * mm, "end": v(-1.03, 7.8) * mm});
            skLineSegment(sketch, "E388", {"start": v(-1.03, 7.8) * mm, "end": v(-1.03, 7.9) * mm});
            skLineSegment(sketch, "E389", {"start": v(-1.03, 7.9) * mm, "end": v(-1.03, 8.02) * mm});
            skLineSegment(sketch, "E390", {"start": v(-1.03, 8.02) * mm, "end": v(-1.04, 8.15) * mm});
            skLineSegment(sketch, "E391", {"start": v(-1.04, 8.15) * mm, "end": v(-1.06, 8.28) * mm});
            skLineSegment(sketch, "E392", {"start": v(-1.06, 8.28) * mm, "end": v(-1.1, 8.4) * mm});
            skLineSegment(sketch, "E393", {"start": v(-1.1, 8.4) * mm, "end": v(-1.14, 8.52) * mm});
            skLineSegment(sketch, "E394", {"start": v(-1.14, 8.52) * mm, "end": v(-1.2, 8.63) * mm});
            skLineSegment(sketch, "E395", {"start": v(-1.2, 8.63) * mm, "end": v(-1.26, 8.74) * mm});
            skLineSegment(sketch, "E396", {"start": v(-1.26, 8.74) * mm, "end": v(-1.33, 8.84) * mm});
            skLineSegment(sketch, "E397", {"start": v(-1.33, 8.84) * mm, "end": v(-1.41, 8.93) * mm});
            skLineSegment(sketch, "E398", {"start": v(-1.41, 8.93) * mm, "end": v(-1.5, 9.02) * mm});
            skLineSegment(sketch, "E399", {"start": v(-1.5, 9.02) * mm, "end": v(-1.6, 9.09) * mm});
            skLineSegment(sketch, "E400", {"start": v(-1.6, 9.09) * mm, "end": v(-1.71, 9.15) * mm});
            skLineSegment(sketch, "E401", {"start": v(-1.71, 9.15) * mm, "end": v(-1.82, 9.2) * mm});
            skLineSegment(sketch, "E402", {"start": v(-1.82, 9.2) * mm, "end": v(-1.94, 9.25) * mm});
            skLineSegment(sketch, "E403", {"start": v(-1.94, 9.25) * mm, "end": v(-2.07, 9.28) * mm});
            skLineSegment(sketch, "E404", {"start": v(-2.07, 9.28) * mm, "end": v(-2.2, 9.3) * mm});
            skLineSegment(sketch, "E405", {"start": v(-2.2, 9.3) * mm, "end": v(-2.33, 9.31) * mm});
            skLineSegment(sketch, "E406", {"start": v(-2.33, 9.31) * mm, "end": v(-2.44, 9.31) * mm});
            skLineSegment(sketch, "E407", {"start": v(-2.44, 9.31) * mm, "end": v(-2.55, 9.31) * mm});
            skLineSegment(sketch, "E408", {"start": v(-2.55, 9.31) * mm, "end": v(-2.67, 9.31) * mm});
            skLineSegment(sketch, "E409", {"start": v(-2.67, 9.31) * mm, "end": v(-2.78, 9.31) * mm});
            skLineSegment(sketch, "E410", {"start": v(-2.78, 9.31) * mm, "end": v(-2.9, 9.31) * mm});
            skLineSegment(sketch, "E411", {"start": v(-2.9, 9.31) * mm, "end": v(-3, 9.31) * mm});
            skLineSegment(sketch, "E412", {"start": v(-3, 9.31) * mm, "end": v(-3.12, 9.31) * mm});
            skLineSegment(sketch, "E413", {"start": v(-3.12, 9.31) * mm, "end": v(-3.23, 9.31) * mm});
            skLineSegment(sketch, "E414", {"start": v(-3.23, 9.31) * mm, "end": v(-3.35, 9.31) * mm});
            skLineSegment(sketch, "E415", {"start": v(-3.35, 9.31) * mm, "end": v(-3.46, 9.31) * mm});
            skLineSegment(sketch, "E416", {"start": v(-3.46, 9.31) * mm, "end": v(-3.57, 9.31) * mm});
            skLineSegment(sketch, "E417", {"start": v(-3.57, 9.31) * mm, "end": v(-3.69, 9.31) * mm});
            skLineSegment(sketch, "E418", {"start": v(-3.69, 9.31) * mm, "end": v(-3.8, 9.31) * mm});
            skLineSegment(sketch, "E419", {"start": v(-3.8, 9.31) * mm, "end": v(-3.91, 9.31) * mm});
            skLineSegment(sketch, "E420", {"start": v(-3.91, 9.31) * mm, "end": v(-4.02, 9.31) * mm});
            skLineSegment(sketch, "E421", {"start": v(-4.02, 9.31) * mm, "end": v(-4.14, 9.31) * mm});
            skLineSegment(sketch, "E422", {"start": v(-4.14, 9.31) * mm, "end": v(-4.14, 9.44) * mm});
            skLineSegment(sketch, "E423", {"start": v(-4.14, 9.44) * mm, "end": v(-4.14, 9.57) * mm});
            skLineSegment(sketch, "E424", {"start": v(-4.14, 9.57) * mm, "end": v(-4.14, 9.7) * mm});
            skLineSegment(sketch, "E425", {"start": v(-4.14, 9.7) * mm, "end": v(-4.14, 9.83) * mm});
            skLineSegment(sketch, "E426", {"start": v(-4.14, 9.83) * mm, "end": v(-4.14, 9.96) * mm});
            skLineSegment(sketch, "E427", {"start": v(-4.14, 9.96) * mm, "end": v(-4.14, 10.09) * mm});
            skLineSegment(sketch, "E428", {"start": v(-4.14, 10.09) * mm, "end": v(-4.14, 10.22) * mm});
            skLineSegment(sketch, "E429", {"start": v(-4.14, 10.22) * mm, "end": v(-4.14, 10.34) * mm});
            skLineSegment(sketch, "E430", {"start": v(-4.14, 10.34) * mm, "end": v(-4.14, 10.47) * mm});
            skLineSegment(sketch, "E431", {"start": v(-4.14, 10.47) * mm, "end": v(-4.14, 10.6) * mm});
            skLineSegment(sketch, "E432", {"start": v(-4.14, 10.6) * mm, "end": v(-4.14, 10.73) * mm});
            skLineSegment(sketch, "E433", {"start": v(-4.14, 10.73) * mm, "end": v(-4.14, 10.86) * mm});
            skLineSegment(sketch, "E434", {"start": v(-4.14, 10.86) * mm, "end": v(-4.14, 11) * mm});
            skLineSegment(sketch, "E435", {"start": v(-4.14, 11) * mm, "end": v(-4.14, 11.12) * mm});
            skLineSegment(sketch, "E436", {"start": v(-4.14, 11.12) * mm, "end": v(-4.14, 11.25) * mm});
            skLineSegment(sketch, "E437", {"start": v(-4.14, 11.25) * mm, "end": v(-4.14, 11.38) * mm});
            skLineSegment(sketch, "E438", {"start": v(-4.14, 11.38) * mm, "end": v(-4.14, 11.6) * mm});
            skLineSegment(sketch, "E439", {"start": v(-4.14, 11.6) * mm, "end": v(-4.14, 11.83) * mm});
            skLineSegment(sketch, "E440", {"start": v(-4.14, 11.83) * mm, "end": v(-4.14, 12.06) * mm});
            skLineSegment(sketch, "E441", {"start": v(-4.14, 12.06) * mm, "end": v(-4.14, 12.28) * mm});
            skLineSegment(sketch, "E442", {"start": v(-4.14, 12.28) * mm, "end": v(-4.14, 12.51) * mm});
            skLineSegment(sketch, "E443", {"start": v(-4.14, 12.51) * mm, "end": v(-4.14, 12.74) * mm});
            skLineSegment(sketch, "E444", {"start": v(-4.14, 12.74) * mm, "end": v(-4.14, 12.96) * mm});
            skLineSegment(sketch, "E445", {"start": v(-4.14, 12.96) * mm, "end": v(-4.14, 13.19) * mm});
            skLineSegment(sketch, "E446", {"start": v(-4.14, 13.19) * mm, "end": v(-4.14, 13.42) * mm});
            skLineSegment(sketch, "E447", {"start": v(-4.14, 13.42) * mm, "end": v(-4.14, 13.64) * mm});
            skLineSegment(sketch, "E448", {"start": v(-4.14, 13.64) * mm, "end": v(-4.14, 13.87) * mm});
            skLineSegment(sketch, "E449", {"start": v(-4.14, 13.87) * mm, "end": v(-4.14, 14.1) * mm});
            skLineSegment(sketch, "E450", {"start": v(-4.14, 14.1) * mm, "end": v(-4.14, 14.32) * mm});
            skLineSegment(sketch, "E451", {"start": v(-4.14, 14.32) * mm, "end": v(-4.14, 14.55) * mm});
            skLineSegment(sketch, "E452", {"start": v(-4.14, 14.55) * mm, "end": v(-4.14, 14.77) * mm});
            skLineSegment(sketch, "E453", {"start": v(-4.14, 14.77) * mm, "end": v(-4.14, 15) * mm});
            skLineSegment(sketch, "E454", {"start": v(-4.14, 15) * mm, "end": v(-4.27, 14.95) * mm});
            skLineSegment(sketch, "E455", {"start": v(-4.27, 14.95) * mm, "end": v(-4.4, 14.9) * mm});
            skLineSegment(sketch, "E456", {"start": v(-4.4, 14.9) * mm, "end": v(-4.53, 14.84) * mm});
            skLineSegment(sketch, "E457", {"start": v(-4.53, 14.84) * mm, "end": v(-4.66, 14.8) * mm});
            skLineSegment(sketch, "E458", {"start": v(-4.66, 14.8) * mm, "end": v(-4.78, 14.74) * mm});
            skLineSegment(sketch, "E459", {"start": v(-4.78, 14.74) * mm, "end": v(-4.91, 14.69) * mm});
            skLineSegment(sketch, "E460", {"start": v(-4.91, 14.69) * mm, "end": v(-5.04, 14.64) * mm});
            skLineSegment(sketch, "E461", {"start": v(-5.04, 14.64) * mm, "end": v(-5.17, 14.59) * mm});
            skLineSegment(sketch, "E462", {"start": v(-5.17, 14.59) * mm, "end": v(-5.3, 14.53) * mm});
            skLineSegment(sketch, "E463", {"start": v(-5.3, 14.53) * mm, "end": v(-5.43, 14.48) * mm});
            skLineSegment(sketch, "E464", {"start": v(-5.43, 14.48) * mm, "end": v(-5.56, 14.43) * mm});
            skLineSegment(sketch, "E465", {"start": v(-5.56, 14.43) * mm, "end": v(-5.69, 14.38) * mm});
            skLineSegment(sketch, "E466", {"start": v(-5.69, 14.38) * mm, "end": v(-5.82, 14.33) * mm});
            skLineSegment(sketch, "E467", {"start": v(-5.82, 14.33) * mm, "end": v(-5.95, 14.28) * mm});
            skLineSegment(sketch, "E468", {"start": v(-5.95, 14.28) * mm, "end": v(-6.08, 14.22) * mm});
            skLineSegment(sketch, "E469", {"start": v(-6.08, 14.22) * mm, "end": v(-6.2, 14.17) * mm});
            skLineSegment(sketch, "E470", {"start": v(-6.2, 14.17) * mm, "end": v(-6.24, 14.16) * mm});
            skLineSegment(sketch, "E471", {"start": v(-6.24, 14.16) * mm, "end": v(-6.27, 14.15) * mm});
            skLineSegment(sketch, "E472", {"start": v(-6.27, 14.15) * mm, "end": v(-6.3, 14.13) * mm});
            skLineSegment(sketch, "E473", {"start": v(-6.3, 14.13) * mm, "end": v(-6.34, 14.12) * mm});
            skLineSegment(sketch, "E474", {"start": v(-6.34, 14.12) * mm, "end": v(-6.37, 14.1) * mm});
            skLineSegment(sketch, "E475", {"start": v(-6.37, 14.1) * mm, "end": v(-6.4, 14.1) * mm});
            skLineSegment(sketch, "E476", {"start": v(-6.4, 14.1) * mm, "end": v(-6.43, 14.08) * mm});
            skLineSegment(sketch, "E477", {"start": v(-6.43, 14.08) * mm, "end": v(-6.47, 14.07) * mm});
            skLineSegment(sketch, "E478", {"start": v(-6.47, 14.07) * mm, "end": v(-6.5, 14.06) * mm});
            skLineSegment(sketch, "E479", {"start": v(-6.5, 14.06) * mm, "end": v(-6.53, 14.04) * mm});
            skLineSegment(sketch, "E480", {"start": v(-6.53, 14.04) * mm, "end": v(-6.56, 14.03) * mm});
            skLineSegment(sketch, "E481", {"start": v(-6.56, 14.03) * mm, "end": v(-6.6, 14.02) * mm});
            skLineSegment(sketch, "E482", {"start": v(-6.6, 14.02) * mm, "end": v(-6.63, 14) * mm});
            skLineSegment(sketch, "E483", {"start": v(-6.63, 14) * mm, "end": v(-6.66, 14) * mm});
            skLineSegment(sketch, "E484", {"start": v(-6.66, 14) * mm, "end": v(-6.7, 13.98) * mm});
            skLineSegment(sketch, "E485", {"start": v(-6.7, 13.98) * mm, "end": v(-6.72, 13.97) * mm});
            skLineSegment(sketch, "E486", {"start": v(-6.72, 13.97) * mm, "end": v(-6.86, 13.65) * mm});
            skLineSegment(sketch, "E487", {"start": v(-6.86, 13.65) * mm, "end": v(-7, 13.33) * mm});
            skLineSegment(sketch, "E488", {"start": v(-7, 13.33) * mm, "end": v(-7.12, 13) * mm});
            skLineSegment(sketch, "E489", {"start": v(-7.12, 13) * mm, "end": v(-7.26, 12.69) * mm});
            skLineSegment(sketch, "E490", {"start": v(-7.26, 12.69) * mm, "end": v(-7.39, 12.37) * mm});
            skLineSegment(sketch, "E491", {"start": v(-7.39, 12.37) * mm, "end": v(-7.52, 12.05) * mm});
            skLineSegment(sketch, "E492", {"start": v(-7.52, 12.05) * mm, "end": v(-7.66, 11.73) * mm});
            skLineSegment(sketch, "E493", {"start": v(-7.66, 11.73) * mm, "end": v(-7.79, 11.4) * mm});
            skLineSegment(sketch, "E494", {"start": v(-7.79, 11.4) * mm, "end": v(-7.92, 11.1) * mm});
            skLineSegment(sketch, "E495", {"start": v(-7.92, 11.1) * mm, "end": v(-8.06, 10.77) * mm});
            skLineSegment(sketch, "E496", {"start": v(-8.06, 10.77) * mm, "end": v(-8.19, 10.45) * mm});
            skLineSegment(sketch, "E497", {"start": v(-8.19, 10.45) * mm, "end": v(-8.32, 10.13) * mm});
            skLineSegment(sketch, "E498", {"start": v(-8.32, 10.13) * mm, "end": v(-8.45, 9.81) * mm});
            skLineSegment(sketch, "E499", {"start": v(-8.45, 9.81) * mm, "end": v(-8.59, 9.5) * mm});
            skLineSegment(sketch, "E500", {"start": v(-8.59, 9.5) * mm, "end": v(-8.72, 9.17) * mm});
            skLineSegment(sketch, "E501", {"start": v(-8.72, 9.17) * mm, "end": v(-8.85, 8.85) * mm});
            skLineSegment(sketch, "E502", {"start": v(-8.85, 8.85) * mm, "end": v(-9.17, 8.72) * mm});
            skLineSegment(sketch, "E503", {"start": v(-9.17, 8.72) * mm, "end": v(-9.5, 8.59) * mm});
            skLineSegment(sketch, "E504", {"start": v(-9.5, 8.59) * mm, "end": v(-9.81, 8.45) * mm});
            skLineSegment(sketch, "E505", {"start": v(-9.81, 8.45) * mm, "end": v(-10.13, 8.32) * mm});
            skLineSegment(sketch, "E506", {"start": v(-10.13, 8.32) * mm, "end": v(-10.45, 8.19) * mm});
            skLineSegment(sketch, "E507", {"start": v(-10.45, 8.19) * mm, "end": v(-10.77, 8.06) * mm});
            skLineSegment(sketch, "E508", {"start": v(-10.77, 8.06) * mm, "end": v(-11.1, 7.92) * mm});
            skLineSegment(sketch, "E509", {"start": v(-11.1, 7.92) * mm, "end": v(-11.4, 7.79) * mm});
            skLineSegment(sketch, "E510", {"start": v(-11.4, 7.79) * mm, "end": v(-11.73, 7.66) * mm});
            skLineSegment(sketch, "E511", {"start": v(-11.73, 7.66) * mm, "end": v(-12.05, 7.52) * mm});
            skLineSegment(sketch, "E512", {"start": v(-12.05, 7.52) * mm, "end": v(-12.37, 7.39) * mm});
            skLineSegment(sketch, "E513", {"start": v(-12.37, 7.39) * mm, "end": v(-12.69, 7.26) * mm});
            skLineSegment(sketch, "E514", {"start": v(-12.69, 7.26) * mm, "end": v(-13, 7.12) * mm});
            skLineSegment(sketch, "E515", {"start": v(-13, 7.12) * mm, "end": v(-13.33, 7) * mm});
            skLineSegment(sketch, "E516", {"start": v(-13.33, 7) * mm, "end": v(-13.65, 6.86) * mm});
            skLineSegment(sketch, "E517", {"start": v(-13.65, 6.86) * mm, "end": v(-13.97, 6.72) * mm});
            skLineSegment(sketch, "E518", {"start": v(-13.97, 6.72) * mm, "end": v(-13.98, 6.7) * mm});
            skLineSegment(sketch, "E519", {"start": v(-13.98, 6.7) * mm, "end": v(-14, 6.66) * mm});
            skLineSegment(sketch, "E520", {"start": v(-14, 6.66) * mm, "end": v(-14, 6.63) * mm});
            skLineSegment(sketch, "E521", {"start": v(-14, 6.63) * mm, "end": v(-14.02, 6.6) * mm});
            skLineSegment(sketch, "E522", {"start": v(-14.02, 6.6) * mm, "end": v(-14.03, 6.56) * mm});
            skLineSegment(sketch, "E523", {"start": v(-14.03, 6.56) * mm, "end": v(-14.04, 6.53) * mm});
            skLineSegment(sketch, "E524", {"start": v(-14.04, 6.53) * mm, "end": v(-14.06, 6.5) * mm});
            skLineSegment(sketch, "E525", {"start": v(-14.06, 6.5) * mm, "end": v(-14.07, 6.47) * mm});
            skLineSegment(sketch, "E526", {"start": v(-14.07, 6.47) * mm, "end": v(-14.08, 6.43) * mm});
            skLineSegment(sketch, "E527", {"start": v(-14.08, 6.43) * mm, "end": v(-14.1, 6.4) * mm});
            skLineSegment(sketch, "E528", {"start": v(-14.1, 6.4) * mm, "end": v(-14.1, 6.37) * mm});
            skLineSegment(sketch, "E529", {"start": v(-14.1, 6.37) * mm, "end": v(-14.12, 6.34) * mm});
            skLineSegment(sketch, "E530", {"start": v(-14.12, 6.34) * mm, "end": v(-14.13, 6.3) * mm});
            skLineSegment(sketch, "E531", {"start": v(-14.13, 6.3) * mm, "end": v(-14.15, 6.27) * mm});
            skLineSegment(sketch, "E532", {"start": v(-14.15, 6.27) * mm, "end": v(-14.16, 6.24) * mm});
            skLineSegment(sketch, "E533", {"start": v(-14.16, 6.24) * mm, "end": v(-14.17, 6.2) * mm});
            skLineSegment(sketch, "E534", {"start": v(-14.17, 6.2) * mm, "end": v(-14.22, 6.08) * mm});
            skLineSegment(sketch, "E535", {"start": v(-14.22, 6.08) * mm, "end": v(-14.28, 5.95) * mm});
            skLineSegment(sketch, "E536", {"start": v(-14.28, 5.95) * mm, "end": v(-14.33, 5.82) * mm});
            skLineSegment(sketch, "E537", {"start": v(-14.33, 5.82) * mm, "end": v(-14.38, 5.69) * mm});
            skLineSegment(sketch, "E538", {"start": v(-14.38, 5.69) * mm, "end": v(-14.43, 5.56) * mm});
            skLineSegment(sketch, "E539", {"start": v(-14.43, 5.56) * mm, "end": v(-14.48, 5.43) * mm});
            skLineSegment(sketch, "E540", {"start": v(-14.48, 5.43) * mm, "end": v(-14.53, 5.3) * mm});
            skLineSegment(sketch, "E541", {"start": v(-14.53, 5.3) * mm, "end": v(-14.59, 5.17) * mm});
            skLineSegment(sketch, "E542", {"start": v(-14.59, 5.17) * mm, "end": v(-14.64, 5.04) * mm});
            skLineSegment(sketch, "E543", {"start": v(-14.64, 5.04) * mm, "end": v(-14.69, 4.91) * mm});
            skLineSegment(sketch, "E544", {"start": v(-14.69, 4.91) * mm, "end": v(-14.74, 4.78) * mm});
            skLineSegment(sketch, "E545", {"start": v(-14.74, 4.78) * mm, "end": v(-14.8, 4.66) * mm});
            skLineSegment(sketch, "E546", {"start": v(-14.8, 4.66) * mm, "end": v(-14.84, 4.53) * mm});
            skLineSegment(sketch, "E547", {"start": v(-14.84, 4.53) * mm, "end": v(-14.9, 4.4) * mm});
            skLineSegment(sketch, "E548", {"start": v(-14.9, 4.4) * mm, "end": v(-14.95, 4.27) * mm});
            skLineSegment(sketch, "E549", {"start": v(-14.95, 4.27) * mm, "end": v(-15, 4.14) * mm});
            skLineSegment(sketch, "E550", {"start": v(-15, 4.14) * mm, "end": v(-14.77, 4.14) * mm});
            skLineSegment(sketch, "E551", {"start": v(-14.77, 4.14) * mm, "end": v(-14.55, 4.14) * mm});
            skLineSegment(sketch, "E552", {"start": v(-14.55, 4.14) * mm, "end": v(-14.32, 4.14) * mm});
            skLineSegment(sketch, "E553", {"start": v(-14.32, 4.14) * mm, "end": v(-14.1, 4.14) * mm});
            skLineSegment(sketch, "E554", {"start": v(-14.1, 4.14) * mm, "end": v(-13.87, 4.14) * mm});
            skLineSegment(sketch, "E555", {"start": v(-13.87, 4.14) * mm, "end": v(-13.64, 4.14) * mm});
            skLineSegment(sketch, "E556", {"start": v(-13.64, 4.14) * mm, "end": v(-13.42, 4.14) * mm});
            skLineSegment(sketch, "E557", {"start": v(-13.42, 4.14) * mm, "end": v(-13.19, 4.14) * mm});
            skLineSegment(sketch, "E558", {"start": v(-13.19, 4.14) * mm, "end": v(-12.96, 4.14) * mm});
            skLineSegment(sketch, "E559", {"start": v(-12.96, 4.14) * mm, "end": v(-12.74, 4.14) * mm});
            skLineSegment(sketch, "E560", {"start": v(-12.74, 4.14) * mm, "end": v(-12.51, 4.14) * mm});
            skLineSegment(sketch, "E561", {"start": v(-12.51, 4.14) * mm, "end": v(-12.28, 4.14) * mm});
            skLineSegment(sketch, "E562", {"start": v(-12.28, 4.14) * mm, "end": v(-12.06, 4.14) * mm});
            skLineSegment(sketch, "E563", {"start": v(-12.06, 4.14) * mm, "end": v(-11.83, 4.14) * mm});
            skLineSegment(sketch, "E564", {"start": v(-11.83, 4.14) * mm, "end": v(-11.6, 4.14) * mm});
            skLineSegment(sketch, "E565", {"start": v(-11.6, 4.14) * mm, "end": v(-11.38, 4.14) * mm});
            skLineSegment(sketch, "E566", {"start": v(-11.38, 4.14) * mm, "end": v(-11.25, 4.14) * mm});
            skLineSegment(sketch, "E567", {"start": v(-11.25, 4.14) * mm, "end": v(-11.12, 4.14) * mm});
            skLineSegment(sketch, "E568", {"start": v(-11.12, 4.14) * mm, "end": v(-11, 4.14) * mm});
            skLineSegment(sketch, "E569", {"start": v(-11, 4.14) * mm, "end": v(-10.86, 4.14) * mm});
            skLineSegment(sketch, "E570", {"start": v(-10.86, 4.14) * mm, "end": v(-10.73, 4.14) * mm});
            skLineSegment(sketch, "E571", {"start": v(-10.73, 4.14) * mm, "end": v(-10.6, 4.14) * mm});
            skLineSegment(sketch, "E572", {"start": v(-10.6, 4.14) * mm, "end": v(-10.47, 4.14) * mm});
            skLineSegment(sketch, "E573", {"start": v(-10.47, 4.14) * mm, "end": v(-10.34, 4.14) * mm});
            skLineSegment(sketch, "E574", {"start": v(-10.34, 4.14) * mm, "end": v(-10.22, 4.14) * mm});
            skLineSegment(sketch, "E575", {"start": v(-10.22, 4.14) * mm, "end": v(-10.09, 4.14) * mm});
            skLineSegment(sketch, "E576", {"start": v(-10.09, 4.14) * mm, "end": v(-9.96, 4.14) * mm});
            skLineSegment(sketch, "E577", {"start": v(-9.96, 4.14) * mm, "end": v(-9.83, 4.14) * mm});
            skLineSegment(sketch, "E578", {"start": v(-9.83, 4.14) * mm, "end": v(-9.7, 4.14) * mm});
            skLineSegment(sketch, "E579", {"start": v(-9.7, 4.14) * mm, "end": v(-9.57, 4.14) * mm});
            skLineSegment(sketch, "E580", {"start": v(-9.57, 4.14) * mm, "end": v(-9.44, 4.14) * mm});
            skLineSegment(sketch, "E581", {"start": v(-9.44, 4.14) * mm, "end": v(-9.31, 4.14) * mm});
            skLineSegment(sketch, "E582", {"start": v(-9.31, 4.14) * mm, "end": v(-9.31, 4.02) * mm});
            skLineSegment(sketch, "E583", {"start": v(-9.31, 4.02) * mm, "end": v(-9.31, 3.91) * mm});
            skLineSegment(sketch, "E584", {"start": v(-9.31, 3.91) * mm, "end": v(-9.31, 3.8) * mm});
            skLineSegment(sketch, "E585", {"start": v(-9.31, 3.8) * mm, "end": v(-9.31, 3.69) * mm});
            skLineSegment(sketch, "E586", {"start": v(-9.31, 3.69) * mm, "end": v(-9.31, 3.57) * mm});
            skLineSegment(sketch, "E587", {"start": v(-9.31, 3.57) * mm, "end": v(-9.31, 3.46) * mm});
            skLineSegment(sketch, "E588", {"start": v(-9.31, 3.46) * mm, "end": v(-9.31, 3.35) * mm});
            skLineSegment(sketch, "E589", {"start": v(-9.31, 3.35) * mm, "end": v(-9.31, 3.23) * mm});
            skLineSegment(sketch, "E590", {"start": v(-9.31, 3.23) * mm, "end": v(-9.31, 3.12) * mm});
            skLineSegment(sketch, "E591", {"start": v(-9.31, 3.12) * mm, "end": v(-9.31, 3) * mm});
            skLineSegment(sketch, "E592", {"start": v(-9.31, 3) * mm, "end": v(-9.31, 2.9) * mm});
            skLineSegment(sketch, "E593", {"start": v(-9.31, 2.9) * mm, "end": v(-9.31, 2.78) * mm});
            skLineSegment(sketch, "E594", {"start": v(-9.31, 2.78) * mm, "end": v(-9.31, 2.67) * mm});
            skLineSegment(sketch, "E595", {"start": v(-9.31, 2.67) * mm, "end": v(-9.31, 2.55) * mm});
            skLineSegment(sketch, "E596", {"start": v(-9.31, 2.55) * mm, "end": v(-9.31, 2.44) * mm});
            skLineSegment(sketch, "E597", {"start": v(-9.31, 2.44) * mm, "end": v(-9.31, 2.33) * mm});
            skLineSegment(sketch, "E598", {"start": v(-9.31, 2.33) * mm, "end": v(-9.3, 2.2) * mm});
            skLineSegment(sketch, "E599", {"start": v(-9.3, 2.2) * mm, "end": v(-9.28, 2.07) * mm});
            skLineSegment(sketch, "E600", {"start": v(-9.28, 2.07) * mm, "end": v(-9.25, 1.94) * mm});
            skLineSegment(sketch, "E601", {"start": v(-9.25, 1.94) * mm, "end": v(-9.2, 1.82) * mm});
            skLineSegment(sketch, "E602", {"start": v(-9.2, 1.82) * mm, "end": v(-9.15, 1.71) * mm});
            skLineSegment(sketch, "E603", {"start": v(-9.15, 1.71) * mm, "end": v(-9.09, 1.6) * mm});
            skLineSegment(sketch, "E604", {"start": v(-9.09, 1.6) * mm, "end": v(-9.02, 1.5) * mm});
            skLineSegment(sketch, "E605", {"start": v(-9.02, 1.5) * mm, "end": v(-8.93, 1.41) * mm});
            skLineSegment(sketch, "E606", {"start": v(-8.93, 1.41) * mm, "end": v(-8.84, 1.33) * mm});
            skLineSegment(sketch, "E607", {"start": v(-8.84, 1.33) * mm, "end": v(-8.74, 1.26) * mm});
            skLineSegment(sketch, "E608", {"start": v(-8.74, 1.26) * mm, "end": v(-8.63, 1.2) * mm});
            skLineSegment(sketch, "E609", {"start": v(-8.63, 1.2) * mm, "end": v(-8.52, 1.14) * mm});
            skLineSegment(sketch, "E610", {"start": v(-8.52, 1.14) * mm, "end": v(-8.4, 1.1) * mm});
            skLineSegment(sketch, "E611", {"start": v(-8.4, 1.1) * mm, "end": v(-8.28, 1.06) * mm});
            skLineSegment(sketch, "E612", {"start": v(-8.28, 1.06) * mm, "end": v(-8.15, 1.04) * mm});
            skLineSegment(sketch, "E613", {"start": v(-8.15, 1.04) * mm, "end": v(-8.02, 1.03) * mm});
            skLineSegment(sketch, "E614", {"start": v(-8.02, 1.03) * mm, "end": v(-7.9, 1.03) * mm});
            skLineSegment(sketch, "E615", {"start": v(-7.9, 1.03) * mm, "end": v(-7.8, 1.03) * mm});
            skLineSegment(sketch, "E616", {"start": v(-7.8, 1.03) * mm, "end": v(-7.68, 1.03) * mm});
            skLineSegment(sketch, "E617", {"start": v(-7.68, 1.03) * mm, "end": v(-7.56, 1.03) * mm});
            skLineSegment(sketch, "E618", {"start": v(-7.56, 1.03) * mm, "end": v(-7.45, 1.03) * mm});
            skLineSegment(sketch, "E619", {"start": v(-7.45, 1.03) * mm, "end": v(-7.34, 1.03) * mm});
            skLineSegment(sketch, "E620", {"start": v(-7.34, 1.03) * mm, "end": v(-7.23, 1.03) * mm});
            skLineSegment(sketch, "E621", {"start": v(-7.23, 1.03) * mm, "end": v(-7.11, 1.03) * mm});
            skLineSegment(sketch, "E622", {"start": v(-7.11, 1.03) * mm, "end": v(-7, 1.03) * mm});
            skLineSegment(sketch, "E623", {"start": v(-7, 1.03) * mm, "end": v(-6.89, 1.03) * mm});
            skLineSegment(sketch, "E624", {"start": v(-6.89, 1.03) * mm, "end": v(-6.77, 1.03) * mm});
            skLineSegment(sketch, "E625", {"start": v(-6.77, 1.03) * mm, "end": v(-6.66, 1.03) * mm});
            skLineSegment(sketch, "E626", {"start": v(-6.66, 1.03) * mm, "end": v(-6.55, 1.03) * mm});
            skLineSegment(sketch, "E627", {"start": v(-6.55, 1.03) * mm, "end": v(-6.43, 1.03) * mm});
            skLineSegment(sketch, "E628", {"start": v(-6.43, 1.03) * mm, "end": v(-6.32, 1.03) * mm});
            skLineSegment(sketch, "E629", {"start": v(-6.32, 1.03) * mm, "end": v(-6.2, 1.03) * mm});
            skLineSegment(sketch, "E630", {"start": v(-6.2, 1.03) * mm, "end": v(-6.2, 0.97) * mm});
            skLineSegment(sketch, "E631", {"start": v(-6.2, 0.97) * mm, "end": v(-6.2, 0.9) * mm});
            skLineSegment(sketch, "E632", {"start": v(-6.2, 0.9) * mm, "end": v(-6.2, 0.84) * mm});
            skLineSegment(sketch, "E633", {"start": v(-6.2, 0.84) * mm, "end": v(-6.2, 0.78) * mm});
            skLineSegment(sketch, "E634", {"start": v(-6.2, 0.78) * mm, "end": v(-6.2, 0.71) * mm});
            skLineSegment(sketch, "E635", {"start": v(-6.2, 0.71) * mm, "end": v(-6.2, 0.65) * mm});
            skLineSegment(sketch, "E636", {"start": v(-6.2, 0.65) * mm, "end": v(-6.2, 0.58) * mm});
            skLineSegment(sketch, "E637", {"start": v(-6.2, 0.58) * mm, "end": v(-6.2, 0.52) * mm});
            skLineSegment(sketch, "E638", {"start": v(-6.2, 0.52) * mm, "end": v(-6.2, 0.45) * mm});
            skLineSegment(sketch, "E639", {"start": v(-6.2, 0.45) * mm, "end": v(-6.2, 0.39) * mm});
            skLineSegment(sketch, "E640", {"start": v(-6.2, 0.39) * mm, "end": v(-6.2, 0.32) * mm});
            skLineSegment(sketch, "E641", {"start": v(-6.2, 0.32) * mm, "end": v(-6.2, 0.26) * mm});
            skLineSegment(sketch, "E642", {"start": v(-6.2, 0.26) * mm, "end": v(-6.2, 0.2) * mm});
            skLineSegment(sketch, "E643", {"start": v(-6.2, 0.2) * mm, "end": v(-6.2, 0.13) * mm});
            skLineSegment(sketch, "E644", {"start": v(-6.2, 0.13) * mm, "end": v(-6.2, 0.06) * mm});
            skLineSegment(sketch, "E645", {"start": v(-6.2, 0.06) * mm, "end": v(-6.2, 0) * mm});
            skLineSegment(sketch, "E646", {"start": v(-6.2, 0) * mm, "end": v(-6.2, -0.06) * mm});
            skLineSegment(sketch, "E647", {"start": v(-6.2, -0.06) * mm, "end": v(-6.2, -0.13) * mm});
            skLineSegment(sketch, "E648", {"start": v(-6.2, -0.13) * mm, "end": v(-6.2, -0.2) * mm});
            skLineSegment(sketch, "E649", {"start": v(-6.2, -0.2) * mm, "end": v(-6.2, -0.26) * mm});
            skLineSegment(sketch, "E650", {"start": v(-6.2, -0.26) * mm, "end": v(-6.2, -0.32) * mm});
            skLineSegment(sketch, "E651", {"start": v(-6.2, -0.32) * mm, "end": v(-6.2, -0.39) * mm});
            skLineSegment(sketch, "E652", {"start": v(-6.2, -0.39) * mm, "end": v(-6.2, -0.45) * mm});
            skLineSegment(sketch, "E653", {"start": v(-6.2, -0.45) * mm, "end": v(-6.2, -0.52) * mm});
            skLineSegment(sketch, "E654", {"start": v(-6.2, -0.52) * mm, "end": v(-6.2, -0.58) * mm});
            skLineSegment(sketch, "E655", {"start": v(-6.2, -0.58) * mm, "end": v(-6.2, -0.65) * mm});
            skLineSegment(sketch, "E656", {"start": v(-6.2, -0.65) * mm, "end": v(-6.2, -0.71) * mm});
            skLineSegment(sketch, "E657", {"start": v(-6.2, -0.71) * mm, "end": v(-6.2, -0.78) * mm});
            skLineSegment(sketch, "E658", {"start": v(-6.2, -0.78) * mm, "end": v(-6.2, -0.84) * mm});
            skLineSegment(sketch, "E659", {"start": v(-6.2, -0.84) * mm, "end": v(-6.2, -0.9) * mm});
            skLineSegment(sketch, "E660", {"start": v(-6.2, -0.9) * mm, "end": v(-6.2, -0.97) * mm});
            skLineSegment(sketch, "E661", {"start": v(-6.2, -0.97) * mm, "end": v(-6.2, -1.03) * mm});
            skLineSegment(sketch, "E662", {"start": v(-6.2, -1.03) * mm, "end": v(-6.32, -1.03) * mm});
            skLineSegment(sketch, "E663", {"start": v(-6.32, -1.03) * mm, "end": v(-6.43, -1.03) * mm});
            skLineSegment(sketch, "E664", {"start": v(-6.43, -1.03) * mm, "end": v(-6.55, -1.03) * mm});
            skLineSegment(sketch, "E665", {"start": v(-6.55, -1.03) * mm, "end": v(-6.66, -1.03) * mm});
            skLineSegment(sketch, "E666", {"start": v(-6.66, -1.03) * mm, "end": v(-6.77, -1.03) * mm});
            skLineSegment(sketch, "E667", {"start": v(-6.77, -1.03) * mm, "end": v(-6.89, -1.03) * mm});
            skLineSegment(sketch, "E668", {"start": v(-6.89, -1.03) * mm, "end": v(-7, -1.03) * mm});
            skLineSegment(sketch, "E669", {"start": v(-7, -1.03) * mm, "end": v(-7.11, -1.03) * mm});
            skLineSegment(sketch, "E670", {"start": v(-7.11, -1.03) * mm, "end": v(-7.23, -1.03) * mm});
            skLineSegment(sketch, "E671", {"start": v(-7.23, -1.03) * mm, "end": v(-7.34, -1.03) * mm});
            skLineSegment(sketch, "E672", {"start": v(-7.34, -1.03) * mm, "end": v(-7.45, -1.03) * mm});
            skLineSegment(sketch, "E673", {"start": v(-7.45, -1.03) * mm, "end": v(-7.56, -1.03) * mm});
            skLineSegment(sketch, "E674", {"start": v(-7.56, -1.03) * mm, "end": v(-7.68, -1.03) * mm});
            skLineSegment(sketch, "E675", {"start": v(-7.68, -1.03) * mm, "end": v(-7.8, -1.03) * mm});
            skLineSegment(sketch, "E676", {"start": v(-7.8, -1.03) * mm, "end": v(-7.9, -1.03) * mm});
            skLineSegment(sketch, "E677", {"start": v(-7.9, -1.03) * mm, "end": v(-8.02, -1.03) * mm});
            skLineSegment(sketch, "E678", {"start": v(-8.02, -1.03) * mm, "end": v(-8.15, -1.04) * mm});
            skLineSegment(sketch, "E679", {"start": v(-8.15, -1.04) * mm, "end": v(-8.28, -1.06) * mm});
            skLineSegment(sketch, "E680", {"start": v(-8.28, -1.06) * mm, "end": v(-8.4, -1.1) * mm});
            skLineSegment(sketch, "E681", {"start": v(-8.4, -1.1) * mm, "end": v(-8.52, -1.14) * mm});
            skLineSegment(sketch, "E682", {"start": v(-8.52, -1.14) * mm, "end": v(-8.63, -1.2) * mm});
            skLineSegment(sketch, "E683", {"start": v(-8.63, -1.2) * mm, "end": v(-8.74, -1.26) * mm});
            skLineSegment(sketch, "E684", {"start": v(-8.74, -1.26) * mm, "end": v(-8.84, -1.33) * mm});
            skLineSegment(sketch, "E685", {"start": v(-8.84, -1.33) * mm, "end": v(-8.93, -1.41) * mm});
            skLineSegment(sketch, "E686", {"start": v(-8.93, -1.41) * mm, "end": v(-9.02, -1.5) * mm});
            skLineSegment(sketch, "E687", {"start": v(-9.02, -1.5) * mm, "end": v(-9.09, -1.6) * mm});
            skLineSegment(sketch, "E688", {"start": v(-9.09, -1.6) * mm, "end": v(-9.15, -1.71) * mm});
            skLineSegment(sketch, "E689", {"start": v(-9.15, -1.71) * mm, "end": v(-9.2, -1.82) * mm});
            skLineSegment(sketch, "E690", {"start": v(-9.2, -1.82) * mm, "end": v(-9.25, -1.94) * mm});
            skLineSegment(sketch, "E691", {"start": v(-9.25, -1.94) * mm, "end": v(-9.28, -2.07) * mm});
            skLineSegment(sketch, "E692", {"start": v(-9.28, -2.07) * mm, "end": v(-9.3, -2.2) * mm});
            skLineSegment(sketch, "E693", {"start": v(-9.3, -2.2) * mm, "end": v(-9.31, -2.33) * mm});
            skLineSegment(sketch, "E694", {"start": v(-9.31, -2.33) * mm, "end": v(-9.31, -2.44) * mm});
            skLineSegment(sketch, "E695", {"start": v(-9.31, -2.44) * mm, "end": v(-9.31, -2.55) * mm});
            skLineSegment(sketch, "E696", {"start": v(-9.31, -2.55) * mm, "end": v(-9.31, -2.67) * mm});
            skLineSegment(sketch, "E697", {"start": v(-9.31, -2.67) * mm, "end": v(-9.31, -2.78) * mm});
            skLineSegment(sketch, "E698", {"start": v(-9.31, -2.78) * mm, "end": v(-9.31, -2.9) * mm});
            skLineSegment(sketch, "E699", {"start": v(-9.31, -2.9) * mm, "end": v(-9.31, -3) * mm});
            skLineSegment(sketch, "E700", {"start": v(-9.31, -3) * mm, "end": v(-9.31, -3.12) * mm});
            skLineSegment(sketch, "E701", {"start": v(-9.31, -3.12) * mm, "end": v(-9.31, -3.23) * mm});
            skLineSegment(sketch, "E702", {"start": v(-9.31, -3.23) * mm, "end": v(-9.31, -3.35) * mm});
            skLineSegment(sketch, "E703", {"start": v(-9.31, -3.35) * mm, "end": v(-9.31, -3.46) * mm});
            skLineSegment(sketch, "E704", {"start": v(-9.31, -3.46) * mm, "end": v(-9.31, -3.57) * mm});
            skLineSegment(sketch, "E705", {"start": v(-9.31, -3.57) * mm, "end": v(-9.31, -3.69) * mm});
            skLineSegment(sketch, "E706", {"start": v(-9.31, -3.69) * mm, "end": v(-9.31, -3.8) * mm});
            skLineSegment(sketch, "E707", {"start": v(-9.31, -3.8) * mm, "end": v(-9.31, -3.91) * mm});
            skLineSegment(sketch, "E708", {"start": v(-9.31, -3.91) * mm, "end": v(-9.31, -4.02) * mm});
            skLineSegment(sketch, "E709", {"start": v(-9.31, -4.02) * mm, "end": v(-9.31, -4.14) * mm});
            skLineSegment(sketch, "E710", {"start": v(-9.31, -4.14) * mm, "end": v(-9.44, -4.14) * mm});
            skLineSegment(sketch, "E711", {"start": v(-9.44, -4.14) * mm, "end": v(-9.57, -4.14) * mm});
            skLineSegment(sketch, "E712", {"start": v(-9.57, -4.14) * mm, "end": v(-9.7, -4.14) * mm});
            skLineSegment(sketch, "E713", {"start": v(-9.7, -4.14) * mm, "end": v(-9.83, -4.14) * mm});
            skLineSegment(sketch, "E714", {"start": v(-9.83, -4.14) * mm, "end": v(-9.96, -4.14) * mm});
            skLineSegment(sketch, "E715", {"start": v(-9.96, -4.14) * mm, "end": v(-10.09, -4.14) * mm});
            skLineSegment(sketch, "E716", {"start": v(-10.09, -4.14) * mm, "end": v(-10.22, -4.14) * mm});
            skLineSegment(sketch, "E717", {"start": v(-10.22, -4.14) * mm, "end": v(-10.34, -4.14) * mm});
            skLineSegment(sketch, "E718", {"start": v(-10.34, -4.14) * mm, "end": v(-10.47, -4.14) * mm});
            skLineSegment(sketch, "E719", {"start": v(-10.47, -4.14) * mm, "end": v(-10.6, -4.14) * mm});
            skLineSegment(sketch, "E720", {"start": v(-10.6, -4.14) * mm, "end": v(-10.73, -4.14) * mm});
            skLineSegment(sketch, "E721", {"start": v(-10.73, -4.14) * mm, "end": v(-10.86, -4.14) * mm});
            skLineSegment(sketch, "E722", {"start": v(-10.86, -4.14) * mm, "end": v(-11, -4.14) * mm});
            skLineSegment(sketch, "E723", {"start": v(-11, -4.14) * mm, "end": v(-11.12, -4.14) * mm});
            skLineSegment(sketch, "E724", {"start": v(-11.12, -4.14) * mm, "end": v(-11.25, -4.14) * mm});
            skLineSegment(sketch, "E725", {"start": v(-11.25, -4.14) * mm, "end": v(-11.38, -4.14) * mm});
            skLineSegment(sketch, "E726", {"start": v(-11.38, -4.14) * mm, "end": v(-11.6, -4.14) * mm});
            skLineSegment(sketch, "E727", {"start": v(-11.6, -4.14) * mm, "end": v(-11.83, -4.14) * mm});
            skLineSegment(sketch, "E728", {"start": v(-11.83, -4.14) * mm, "end": v(-12.06, -4.14) * mm});
            skLineSegment(sketch, "E729", {"start": v(-12.06, -4.14) * mm, "end": v(-12.28, -4.14) * mm});
            skLineSegment(sketch, "E730", {"start": v(-12.28, -4.14) * mm, "end": v(-12.51, -4.14) * mm});
            skLineSegment(sketch, "E731", {"start": v(-12.51, -4.14) * mm, "end": v(-12.74, -4.14) * mm});
            skLineSegment(sketch, "E732", {"start": v(-12.74, -4.14) * mm, "end": v(-12.96, -4.14) * mm});
            skLineSegment(sketch, "E733", {"start": v(-12.96, -4.14) * mm, "end": v(-13.19, -4.14) * mm});
            skLineSegment(sketch, "E734", {"start": v(-13.19, -4.14) * mm, "end": v(-13.42, -4.14) * mm});
            skLineSegment(sketch, "E735", {"start": v(-13.42, -4.14) * mm, "end": v(-13.64, -4.14) * mm});
            skLineSegment(sketch, "E736", {"start": v(-13.64, -4.14) * mm, "end": v(-13.87, -4.14) * mm});
            skLineSegment(sketch, "E737", {"start": v(-13.87, -4.14) * mm, "end": v(-14.1, -4.14) * mm});
            skLineSegment(sketch, "E738", {"start": v(-14.1, -4.14) * mm, "end": v(-14.32, -4.14) * mm});
            skLineSegment(sketch, "E739", {"start": v(-14.32, -4.14) * mm, "end": v(-14.55, -4.14) * mm});
            skLineSegment(sketch, "E740", {"start": v(-14.55, -4.14) * mm, "end": v(-14.77, -4.14) * mm});
            skLineSegment(sketch, "E741", {"start": v(-14.77, -4.14) * mm, "end": v(-15, -4.14) * mm});
            skLineSegment(sketch, "E742", {"start": v(-15, -4.14) * mm, "end": v(-14.95, -4.27) * mm});
            skLineSegment(sketch, "E743", {"start": v(-14.95, -4.27) * mm, "end": v(-14.9, -4.4) * mm});
            skLineSegment(sketch, "E744", {"start": v(-14.9, -4.4) * mm, "end": v(-14.84, -4.53) * mm});
            skLineSegment(sketch, "E745", {"start": v(-14.84, -4.53) * mm, "end": v(-14.8, -4.66) * mm});
            skLineSegment(sketch, "E746", {"start": v(-14.8, -4.66) * mm, "end": v(-14.74, -4.78) * mm});
            skLineSegment(sketch, "E747", {"start": v(-14.74, -4.78) * mm, "end": v(-14.69, -4.91) * mm});
            skLineSegment(sketch, "E748", {"start": v(-14.69, -4.91) * mm, "end": v(-14.64, -5.04) * mm});
            skLineSegment(sketch, "E749", {"start": v(-14.64, -5.04) * mm, "end": v(-14.59, -5.17) * mm});
            skLineSegment(sketch, "E750", {"start": v(-14.59, -5.17) * mm, "end": v(-14.53, -5.3) * mm});
            skLineSegment(sketch, "E751", {"start": v(-14.53, -5.3) * mm, "end": v(-14.48, -5.43) * mm});
            skLineSegment(sketch, "E752", {"start": v(-14.48, -5.43) * mm, "end": v(-14.43, -5.56) * mm});
            skLineSegment(sketch, "E753", {"start": v(-14.43, -5.56) * mm, "end": v(-14.38, -5.69) * mm});
            skLineSegment(sketch, "E754", {"start": v(-14.38, -5.69) * mm, "end": v(-14.33, -5.82) * mm});
            skLineSegment(sketch, "E755", {"start": v(-14.33, -5.82) * mm, "end": v(-14.28, -5.95) * mm});
            skLineSegment(sketch, "E756", {"start": v(-14.28, -5.95) * mm, "end": v(-14.22, -6.08) * mm});
            skLineSegment(sketch, "E757", {"start": v(-14.22, -6.08) * mm, "end": v(-14.17, -6.2) * mm});
            skLineSegment(sketch, "E758", {"start": v(-14.17, -6.2) * mm, "end": v(-14.16, -6.24) * mm});
            skLineSegment(sketch, "E759", {"start": v(-14.16, -6.24) * mm, "end": v(-14.15, -6.27) * mm});
            skLineSegment(sketch, "E760", {"start": v(-14.15, -6.27) * mm, "end": v(-14.13, -6.3) * mm});
            skLineSegment(sketch, "E761", {"start": v(-14.13, -6.3) * mm, "end": v(-14.12, -6.34) * mm});
            skLineSegment(sketch, "E762", {"start": v(-14.12, -6.34) * mm, "end": v(-14.1, -6.37) * mm});
            skLineSegment(sketch, "E763", {"start": v(-14.1, -6.37) * mm, "end": v(-14.1, -6.4) * mm});
            skLineSegment(sketch, "E764", {"start": v(-14.1, -6.4) * mm, "end": v(-14.08, -6.43) * mm});
            skLineSegment(sketch, "E765", {"start": v(-14.08, -6.43) * mm, "end": v(-14.07, -6.47) * mm});
            skLineSegment(sketch, "E766", {"start": v(-14.07, -6.47) * mm, "end": v(-14.06, -6.5) * mm});
            skLineSegment(sketch, "E767", {"start": v(-14.06, -6.5) * mm, "end": v(-14.04, -6.53) * mm});
            skLineSegment(sketch, "E768", {"start": v(-14.04, -6.53) * mm, "end": v(-14.03, -6.56) * mm});
            skLineSegment(sketch, "E769", {"start": v(-14.03, -6.56) * mm, "end": v(-14.02, -6.6) * mm});
            skLineSegment(sketch, "E770", {"start": v(-14.02, -6.6) * mm, "end": v(-14, -6.63) * mm});
            skLineSegment(sketch, "E771", {"start": v(-14, -6.63) * mm, "end": v(-14, -6.66) * mm});
            skLineSegment(sketch, "E772", {"start": v(-14, -6.66) * mm, "end": v(-13.98, -6.7) * mm});
            skLineSegment(sketch, "E773", {"start": v(-13.98, -6.7) * mm, "end": v(-13.97, -6.72) * mm});
            skLineSegment(sketch, "E774", {"start": v(-13.97, -6.72) * mm, "end": v(-13.65, -6.86) * mm});
            skLineSegment(sketch, "E775", {"start": v(-13.65, -6.86) * mm, "end": v(-13.33, -7) * mm});
            skLineSegment(sketch, "E776", {"start": v(-13.33, -7) * mm, "end": v(-13, -7.12) * mm});
            skLineSegment(sketch, "E777", {"start": v(-13, -7.12) * mm, "end": v(-12.69, -7.26) * mm});
            skLineSegment(sketch, "E778", {"start": v(-12.69, -7.26) * mm, "end": v(-12.37, -7.39) * mm});
            skLineSegment(sketch, "E779", {"start": v(-12.37, -7.39) * mm, "end": v(-12.05, -7.52) * mm});
            skLineSegment(sketch, "E780", {"start": v(-12.05, -7.52) * mm, "end": v(-11.73, -7.66) * mm});
            skLineSegment(sketch, "E781", {"start": v(-11.73, -7.66) * mm, "end": v(-11.4, -7.79) * mm});
            skLineSegment(sketch, "E782", {"start": v(-11.4, -7.79) * mm, "end": v(-11.1, -7.92) * mm});
            skLineSegment(sketch, "E783", {"start": v(-11.1, -7.92) * mm, "end": v(-10.77, -8.06) * mm});
            skLineSegment(sketch, "E784", {"start": v(-10.77, -8.06) * mm, "end": v(-10.45, -8.19) * mm});
            skLineSegment(sketch, "E785", {"start": v(-10.45, -8.19) * mm, "end": v(-10.13, -8.32) * mm});
            skLineSegment(sketch, "E786", {"start": v(-10.13, -8.32) * mm, "end": v(-9.81, -8.45) * mm});
            skLineSegment(sketch, "E787", {"start": v(-9.81, -8.45) * mm, "end": v(-9.5, -8.59) * mm});
            skLineSegment(sketch, "E788", {"start": v(-9.5, -8.59) * mm, "end": v(-9.17, -8.72) * mm});
            skLineSegment(sketch, "E789", {"start": v(-9.17, -8.72) * mm, "end": v(-8.85, -8.85) * mm});
            skLineSegment(sketch, "E790", {"start": v(-8.85, -8.85) * mm, "end": v(-8.72, -9.17) * mm});
            skLineSegment(sketch, "E791", {"start": v(-8.72, -9.17) * mm, "end": v(-8.59, -9.5) * mm});
            skLineSegment(sketch, "E792", {"start": v(-8.59, -9.5) * mm, "end": v(-8.45, -9.81) * mm});
            skLineSegment(sketch, "E793", {"start": v(-8.45, -9.81) * mm, "end": v(-8.32, -10.13) * mm});
            skLineSegment(sketch, "E794", {"start": v(-8.32, -10.13) * mm, "end": v(-8.19, -10.45) * mm});
            skLineSegment(sketch, "E795", {"start": v(-8.19, -10.45) * mm, "end": v(-8.06, -10.77) * mm});
            skLineSegment(sketch, "E796", {"start": v(-8.06, -10.77) * mm, "end": v(-7.92, -11.1) * mm});
            skLineSegment(sketch, "E797", {"start": v(-7.92, -11.1) * mm, "end": v(-7.79, -11.4) * mm});
            skLineSegment(sketch, "E798", {"start": v(-7.79, -11.4) * mm, "end": v(-7.66, -11.73) * mm});
            skLineSegment(sketch, "E799", {"start": v(-7.66, -11.73) * mm, "end": v(-7.52, -12.05) * mm});
            skLineSegment(sketch, "E800", {"start": v(-7.52, -12.05) * mm, "end": v(-7.39, -12.37) * mm});
            skLineSegment(sketch, "E801", {"start": v(-7.39, -12.37) * mm, "end": v(-7.26, -12.69) * mm});
            skLineSegment(sketch, "E802", {"start": v(-7.26, -12.69) * mm, "end": v(-7.12, -13) * mm});
            skLineSegment(sketch, "E803", {"start": v(-7.12, -13) * mm, "end": v(-7, -13.33) * mm});
            skLineSegment(sketch, "E804", {"start": v(-7, -13.33) * mm, "end": v(-6.86, -13.65) * mm});
            skLineSegment(sketch, "E805", {"start": v(-6.86, -13.65) * mm, "end": v(-6.72, -13.97) * mm});
            skLineSegment(sketch, "E806", {"start": v(-6.72, -13.97) * mm, "end": v(-6.7, -13.98) * mm});
            skLineSegment(sketch, "E807", {"start": v(-6.7, -13.98) * mm, "end": v(-6.66, -14) * mm});
            skLineSegment(sketch, "E808", {"start": v(-6.66, -14) * mm, "end": v(-6.63, -14) * mm});
            skLineSegment(sketch, "E809", {"start": v(-6.63, -14) * mm, "end": v(-6.6, -14.02) * mm});
            skLineSegment(sketch, "E810", {"start": v(-6.6, -14.02) * mm, "end": v(-6.56, -14.03) * mm});
            skLineSegment(sketch, "E811", {"start": v(-6.56, -14.03) * mm, "end": v(-6.53, -14.04) * mm});
            skLineSegment(sketch, "E812", {"start": v(-6.53, -14.04) * mm, "end": v(-6.5, -14.06) * mm});
            skLineSegment(sketch, "E813", {"start": v(-6.5, -14.06) * mm, "end": v(-6.47, -14.07) * mm});
            skLineSegment(sketch, "E814", {"start": v(-6.47, -14.07) * mm, "end": v(-6.43, -14.08) * mm});
            skLineSegment(sketch, "E815", {"start": v(-6.43, -14.08) * mm, "end": v(-6.4, -14.1) * mm});
            skLineSegment(sketch, "E816", {"start": v(-6.4, -14.1) * mm, "end": v(-6.37, -14.1) * mm});
            skLineSegment(sketch, "E817", {"start": v(-6.37, -14.1) * mm, "end": v(-6.34, -14.12) * mm});
            skLineSegment(sketch, "E818", {"start": v(-6.34, -14.12) * mm, "end": v(-6.3, -14.13) * mm});
            skLineSegment(sketch, "E819", {"start": v(-6.3, -14.13) * mm, "end": v(-6.27, -14.15) * mm});
            skLineSegment(sketch, "E820", {"start": v(-6.27, -14.15) * mm, "end": v(-6.24, -14.16) * mm});
            skLineSegment(sketch, "E821", {"start": v(-6.24, -14.16) * mm, "end": v(-6.2, -14.17) * mm});
            skLineSegment(sketch, "E822", {"start": v(-6.2, -14.17) * mm, "end": v(-6.08, -14.22) * mm});
            skLineSegment(sketch, "E823", {"start": v(-6.08, -14.22) * mm, "end": v(-5.95, -14.28) * mm});
            skLineSegment(sketch, "E824", {"start": v(-5.95, -14.28) * mm, "end": v(-5.82, -14.33) * mm});
            skLineSegment(sketch, "E825", {"start": v(-5.82, -14.33) * mm, "end": v(-5.69, -14.38) * mm});
            skLineSegment(sketch, "E826", {"start": v(-5.69, -14.38) * mm, "end": v(-5.56, -14.43) * mm});
            skLineSegment(sketch, "E827", {"start": v(-5.56, -14.43) * mm, "end": v(-5.43, -14.48) * mm});
            skLineSegment(sketch, "E828", {"start": v(-5.43, -14.48) * mm, "end": v(-5.3, -14.53) * mm});
            skLineSegment(sketch, "E829", {"start": v(-5.3, -14.53) * mm, "end": v(-5.17, -14.59) * mm});
            skLineSegment(sketch, "E830", {"start": v(-5.17, -14.59) * mm, "end": v(-5.04, -14.64) * mm});
            skLineSegment(sketch, "E831", {"start": v(-5.04, -14.64) * mm, "end": v(-4.91, -14.69) * mm});
            skLineSegment(sketch, "E832", {"start": v(-4.91, -14.69) * mm, "end": v(-4.78, -14.74) * mm});
            skLineSegment(sketch, "E833", {"start": v(-4.78, -14.74) * mm, "end": v(-4.66, -14.8) * mm});
            skLineSegment(sketch, "E834", {"start": v(-4.66, -14.8) * mm, "end": v(-4.53, -14.84) * mm});
            skLineSegment(sketch, "E835", {"start": v(-4.53, -14.84) * mm, "end": v(-4.4, -14.9) * mm});
            skLineSegment(sketch, "E836", {"start": v(-4.4, -14.9) * mm, "end": v(-4.27, -14.95) * mm});
            skLineSegment(sketch, "E837", {"start": v(-4.27, -14.95) * mm, "end": v(-4.14, -15) * mm});
            skLineSegment(sketch, "E838", {"start": v(-4.14, -15) * mm, "end": v(-4.14, -14.77) * mm});
            skLineSegment(sketch, "E839", {"start": v(-4.14, -14.77) * mm, "end": v(-4.14, -14.55) * mm});
            skLineSegment(sketch, "E840", {"start": v(-4.14, -14.55) * mm, "end": v(-4.14, -14.32) * mm});
            skLineSegment(sketch, "E841", {"start": v(-4.14, -14.32) * mm, "end": v(-4.14, -14.1) * mm});
            skLineSegment(sketch, "E842", {"start": v(-4.14, -14.1) * mm, "end": v(-4.14, -13.87) * mm});
            skLineSegment(sketch, "E843", {"start": v(-4.14, -13.87) * mm, "end": v(-4.14, -13.64) * mm});
            skLineSegment(sketch, "E844", {"start": v(-4.14, -13.64) * mm, "end": v(-4.14, -13.42) * mm});
            skLineSegment(sketch, "E845", {"start": v(-4.14, -13.42) * mm, "end": v(-4.14, -13.19) * mm});
            skLineSegment(sketch, "E846", {"start": v(-4.14, -13.19) * mm, "end": v(-4.14, -12.96) * mm});
            skLineSegment(sketch, "E847", {"start": v(-4.14, -12.96) * mm, "end": v(-4.14, -12.74) * mm});
            skLineSegment(sketch, "E848", {"start": v(-4.14, -12.74) * mm, "end": v(-4.14, -12.51) * mm});
            skLineSegment(sketch, "E849", {"start": v(-4.14, -12.51) * mm, "end": v(-4.14, -12.28) * mm});
            skLineSegment(sketch, "E850", {"start": v(-4.14, -12.28) * mm, "end": v(-4.14, -12.06) * mm});
            skLineSegment(sketch, "E851", {"start": v(-4.14, -12.06) * mm, "end": v(-4.14, -11.83) * mm});
            skLineSegment(sketch, "E852", {"start": v(-4.14, -11.83) * mm, "end": v(-4.14, -11.6) * mm});
            skLineSegment(sketch, "E853", {"start": v(-4.14, -11.6) * mm, "end": v(-4.14, -11.38) * mm});
            skLineSegment(sketch, "E854", {"start": v(-4.14, -11.38) * mm, "end": v(-4.14, -11.25) * mm});
            skLineSegment(sketch, "E855", {"start": v(-4.14, -11.25) * mm, "end": v(-4.14, -11.12) * mm});
            skLineSegment(sketch, "E856", {"start": v(-4.14, -11.12) * mm, "end": v(-4.14, -11) * mm});
            skLineSegment(sketch, "E857", {"start": v(-4.14, -11) * mm, "end": v(-4.14, -10.86) * mm});
            skLineSegment(sketch, "E858", {"start": v(-4.14, -10.86) * mm, "end": v(-4.14, -10.73) * mm});
            skLineSegment(sketch, "E859", {"start": v(-4.14, -10.73) * mm, "end": v(-4.14, -10.6) * mm});
            skLineSegment(sketch, "E860", {"start": v(-4.14, -10.6) * mm, "end": v(-4.14, -10.47) * mm});
            skLineSegment(sketch, "E861", {"start": v(-4.14, -10.47) * mm, "end": v(-4.14, -10.34) * mm});
            skLineSegment(sketch, "E862", {"start": v(-4.14, -10.34) * mm, "end": v(-4.14, -10.22) * mm});
            skLineSegment(sketch, "E863", {"start": v(-4.14, -10.22) * mm, "end": v(-4.14, -10.09) * mm});
            skLineSegment(sketch, "E864", {"start": v(-4.14, -10.09) * mm, "end": v(-4.14, -9.96) * mm});
            skLineSegment(sketch, "E865", {"start": v(-4.14, -9.96) * mm, "end": v(-4.14, -9.83) * mm});
            skLineSegment(sketch, "E866", {"start": v(-4.14, -9.83) * mm, "end": v(-4.14, -9.7) * mm});
            skLineSegment(sketch, "E867", {"start": v(-4.14, -9.7) * mm, "end": v(-4.14, -9.57) * mm});
            skLineSegment(sketch, "E868", {"start": v(-4.14, -9.57) * mm, "end": v(-4.14, -9.44) * mm});
            skLineSegment(sketch, "E869", {"start": v(-4.14, -9.44) * mm, "end": v(-4.14, -9.31) * mm});
            skLineSegment(sketch, "E870", {"start": v(-4.14, -9.31) * mm, "end": v(-4.02, -9.31) * mm});
            skLineSegment(sketch, "E871", {"start": v(-4.02, -9.31) * mm, "end": v(-3.91, -9.31) * mm});
            skLineSegment(sketch, "E872", {"start": v(-3.91, -9.31) * mm, "end": v(-3.8, -9.31) * mm});
            skLineSegment(sketch, "E873", {"start": v(-3.8, -9.31) * mm, "end": v(-3.69, -9.31) * mm});
            skLineSegment(sketch, "E874", {"start": v(-3.69, -9.31) * mm, "end": v(-3.57, -9.31) * mm});
            skLineSegment(sketch, "E875", {"start": v(-3.57, -9.31) * mm, "end": v(-3.46, -9.31) * mm});
            skLineSegment(sketch, "E876", {"start": v(-3.46, -9.31) * mm, "end": v(-3.35, -9.31) * mm});
            skLineSegment(sketch, "E877", {"start": v(-3.35, -9.31) * mm, "end": v(-3.23, -9.31) * mm});
            skLineSegment(sketch, "E878", {"start": v(-3.23, -9.31) * mm, "end": v(-3.12, -9.31) * mm});
            skLineSegment(sketch, "E879", {"start": v(-3.12, -9.31) * mm, "end": v(-3, -9.31) * mm});
            skLineSegment(sketch, "E880", {"start": v(-3, -9.31) * mm, "end": v(-2.9, -9.31) * mm});
            skLineSegment(sketch, "E881", {"start": v(-2.9, -9.31) * mm, "end": v(-2.78, -9.31) * mm});
            skLineSegment(sketch, "E882", {"start": v(-2.78, -9.31) * mm, "end": v(-2.67, -9.31) * mm});
            skLineSegment(sketch, "E883", {"start": v(-2.67, -9.31) * mm, "end": v(-2.55, -9.31) * mm});
            skLineSegment(sketch, "E884", {"start": v(-2.55, -9.31) * mm, "end": v(-2.44, -9.31) * mm});
            skLineSegment(sketch, "E885", {"start": v(-2.44, -9.31) * mm, "end": v(-2.33, -9.31) * mm});
            skLineSegment(sketch, "E886", {"start": v(-2.33, -9.31) * mm, "end": v(-2.2, -9.3) * mm});
            skLineSegment(sketch, "E887", {"start": v(-2.2, -9.3) * mm, "end": v(-2.07, -9.28) * mm});
            skLineSegment(sketch, "E888", {"start": v(-2.07, -9.28) * mm, "end": v(-1.94, -9.25) * mm});
            skLineSegment(sketch, "E889", {"start": v(-1.94, -9.25) * mm, "end": v(-1.82, -9.2) * mm});
            skLineSegment(sketch, "E890", {"start": v(-1.82, -9.2) * mm, "end": v(-1.71, -9.15) * mm});
            skLineSegment(sketch, "E891", {"start": v(-1.71, -9.15) * mm, "end": v(-1.6, -9.09) * mm});
            skLineSegment(sketch, "E892", {"start": v(-1.6, -9.09) * mm, "end": v(-1.5, -9.02) * mm});
            skLineSegment(sketch, "E893", {"start": v(-1.5, -9.02) * mm, "end": v(-1.41, -8.93) * mm});
            skLineSegment(sketch, "E894", {"start": v(-1.41, -8.93) * mm, "end": v(-1.33, -8.84) * mm});
            skLineSegment(sketch, "E895", {"start": v(-1.33, -8.84) * mm, "end": v(-1.26, -8.74) * mm});
            skLineSegment(sketch, "E896", {"start": v(-1.26, -8.74) * mm, "end": v(-1.2, -8.63) * mm});
            skLineSegment(sketch, "E897", {"start": v(-1.2, -8.63) * mm, "end": v(-1.14, -8.52) * mm});
            skLineSegment(sketch, "E898", {"start": v(-1.14, -8.52) * mm, "end": v(-1.1, -8.4) * mm});
            skLineSegment(sketch, "E899", {"start": v(-1.1, -8.4) * mm, "end": v(-1.06, -8.28) * mm});
            skLineSegment(sketch, "E900", {"start": v(-1.06, -8.28) * mm, "end": v(-1.04, -8.15) * mm});
            skLineSegment(sketch, "E901", {"start": v(-1.04, -8.15) * mm, "end": v(-1.03, -8.02) * mm});
            skLineSegment(sketch, "E902", {"start": v(-1.03, -8.02) * mm, "end": v(-1.03, -7.9) * mm});
            skLineSegment(sketch, "E903", {"start": v(-1.03, -7.9) * mm, "end": v(-1.03, -7.8) * mm});
            skLineSegment(sketch, "E904", {"start": v(-1.03, -7.8) * mm, "end": v(-1.03, -7.68) * mm});
            skLineSegment(sketch, "E905", {"start": v(-1.03, -7.68) * mm, "end": v(-1.03, -7.56) * mm});
            skLineSegment(sketch, "E906", {"start": v(-1.03, -7.56) * mm, "end": v(-1.03, -7.45) * mm});
            skLineSegment(sketch, "E907", {"start": v(-1.03, -7.45) * mm, "end": v(-1.03, -7.34) * mm});
            skLineSegment(sketch, "E908", {"start": v(-1.03, -7.34) * mm, "end": v(-1.03, -7.23) * mm});
            skLineSegment(sketch, "E909", {"start": v(-1.03, -7.23) * mm, "end": v(-1.03, -7.11) * mm});
            skLineSegment(sketch, "E910", {"start": v(-1.03, -7.11) * mm, "end": v(-1.03, -7) * mm});
            skLineSegment(sketch, "E911", {"start": v(-1.03, -7) * mm, "end": v(-1.03, -6.89) * mm});
            skLineSegment(sketch, "E912", {"start": v(-1.03, -6.89) * mm, "end": v(-1.03, -6.77) * mm});
            skLineSegment(sketch, "E913", {"start": v(-1.03, -6.77) * mm, "end": v(-1.03, -6.66) * mm});
            skLineSegment(sketch, "E914", {"start": v(-1.03, -6.66) * mm, "end": v(-1.03, -6.55) * mm});
            skLineSegment(sketch, "E915", {"start": v(-1.03, -6.55) * mm, "end": v(-1.03, -6.43) * mm});
            skLineSegment(sketch, "E916", {"start": v(-1.03, -6.43) * mm, "end": v(-1.03, -6.32) * mm});
            skLineSegment(sketch, "E917", {"start": v(-1.03, -6.32) * mm, "end": v(-1.03, -6.2) * mm});
            skLineSegment(sketch, "E918", {"start": v(-1.03, -6.2) * mm, "end": v(-0.97, -6.2) * mm});
            skLineSegment(sketch, "E919", {"start": v(-0.97, -6.2) * mm, "end": v(-0.9, -6.2) * mm});
            skLineSegment(sketch, "E920", {"start": v(-0.9, -6.2) * mm, "end": v(-0.84, -6.2) * mm});
            skLineSegment(sketch, "E921", {"start": v(-0.84, -6.2) * mm, "end": v(-0.78, -6.2) * mm});
            skLineSegment(sketch, "E922", {"start": v(-0.78, -6.2) * mm, "end": v(-0.71, -6.2) * mm});
            skLineSegment(sketch, "E923", {"start": v(-0.71, -6.2) * mm, "end": v(-0.65, -6.2) * mm});
            skLineSegment(sketch, "E924", {"start": v(-0.65, -6.2) * mm, "end": v(-0.58, -6.2) * mm});
            skLineSegment(sketch, "E925", {"start": v(-0.58, -6.2) * mm, "end": v(-0.52, -6.2) * mm});
            skLineSegment(sketch, "E926", {"start": v(-0.52, -6.2) * mm, "end": v(-0.45, -6.2) * mm});
            skLineSegment(sketch, "E927", {"start": v(-0.45, -6.2) * mm, "end": v(-0.39, -6.2) * mm});
            skLineSegment(sketch, "E928", {"start": v(-0.39, -6.2) * mm, "end": v(-0.32, -6.2) * mm});
            skLineSegment(sketch, "E929", {"start": v(-0.32, -6.2) * mm, "end": v(-0.26, -6.2) * mm});
            skLineSegment(sketch, "E930", {"start": v(-0.26, -6.2) * mm, "end": v(-0.2, -6.2) * mm});
            skLineSegment(sketch, "E931", {"start": v(-0.2, -6.2) * mm, "end": v(-0.13, -6.2) * mm});
            skLineSegment(sketch, "E932", {"start": v(-0.13, -6.2) * mm, "end": v(-0.06, -6.2) * mm});
            skLineSegment(sketch, "E933", {"start": v(-0.06, -6.2) * mm, "end": v(0, -6.2) * mm});
            skLineSegment(sketch, "E934", {"start": v(0, -6.2) * mm, "end": v(0.06, -6.2) * mm});
            skLineSegment(sketch, "E935", {"start": v(0.06, -6.2) * mm, "end": v(0.13, -6.2) * mm});
            skLineSegment(sketch, "E936", {"start": v(0.13, -6.2) * mm, "end": v(0.2, -6.2) * mm});
            skLineSegment(sketch, "E937", {"start": v(0.2, -6.2) * mm, "end": v(0.26, -6.2) * mm});
            skLineSegment(sketch, "E938", {"start": v(0.26, -6.2) * mm, "end": v(0.32, -6.2) * mm});
            skLineSegment(sketch, "E939", {"start": v(0.32, -6.2) * mm, "end": v(0.39, -6.2) * mm});
            skLineSegment(sketch, "E940", {"start": v(0.39, -6.2) * mm, "end": v(0.45, -6.2) * mm});
            skLineSegment(sketch, "E941", {"start": v(0.45, -6.2) * mm, "end": v(0.52, -6.2) * mm});
            skLineSegment(sketch, "E942", {"start": v(0.52, -6.2) * mm, "end": v(0.58, -6.2) * mm});
            skLineSegment(sketch, "E943", {"start": v(0.58, -6.2) * mm, "end": v(0.65, -6.2) * mm});
            skLineSegment(sketch, "E944", {"start": v(0.65, -6.2) * mm, "end": v(0.71, -6.2) * mm});
            skLineSegment(sketch, "E945", {"start": v(0.71, -6.2) * mm, "end": v(0.78, -6.2) * mm});
            skLineSegment(sketch, "E946", {"start": v(0.78, -6.2) * mm, "end": v(0.84, -6.2) * mm});
            skLineSegment(sketch, "E947", {"start": v(0.84, -6.2) * mm, "end": v(0.9, -6.2) * mm});
            skLineSegment(sketch, "E948", {"start": v(0.9, -6.2) * mm, "end": v(0.97, -6.2) * mm});
            skLineSegment(sketch, "E949", {"start": v(0.97, -6.2) * mm, "end": v(1.03, -6.2) * mm});
            skLineSegment(sketch, "E950", {"start": v(1.03, -6.2) * mm, "end": v(1.03, -6.32) * mm});
            skLineSegment(sketch, "E951", {"start": v(1.03, -6.32) * mm, "end": v(1.03, -6.43) * mm});
            skLineSegment(sketch, "E952", {"start": v(1.03, -6.43) * mm, "end": v(1.03, -6.55) * mm});
            skLineSegment(sketch, "E953", {"start": v(1.03, -6.55) * mm, "end": v(1.03, -6.66) * mm});
            skLineSegment(sketch, "E954", {"start": v(1.03, -6.66) * mm, "end": v(1.03, -6.77) * mm});
            skLineSegment(sketch, "E955", {"start": v(1.03, -6.77) * mm, "end": v(1.03, -6.89) * mm});
            skLineSegment(sketch, "E956", {"start": v(1.03, -6.89) * mm, "end": v(1.03, -7) * mm});
            skLineSegment(sketch, "E957", {"start": v(1.03, -7) * mm, "end": v(1.03, -7.11) * mm});
            skLineSegment(sketch, "E958", {"start": v(1.03, -7.11) * mm, "end": v(1.03, -7.23) * mm});
            skLineSegment(sketch, "E959", {"start": v(1.03, -7.23) * mm, "end": v(1.03, -7.34) * mm});
            skLineSegment(sketch, "E960", {"start": v(1.03, -7.34) * mm, "end": v(1.03, -7.45) * mm});
            skLineSegment(sketch, "E961", {"start": v(1.03, -7.45) * mm, "end": v(1.03, -7.56) * mm});
            skLineSegment(sketch, "E962", {"start": v(1.03, -7.56) * mm, "end": v(1.03, -7.68) * mm});
            skLineSegment(sketch, "E963", {"start": v(1.03, -7.68) * mm, "end": v(1.03, -7.8) * mm});
            skLineSegment(sketch, "E964", {"start": v(1.03, -7.8) * mm, "end": v(1.03, -7.9) * mm});
            skLineSegment(sketch, "E965", {"start": v(1.03, -7.9) * mm, "end": v(1.03, -8.02) * mm});
            skLineSegment(sketch, "E966", {"start": v(1.03, -8.02) * mm, "end": v(1.04, -8.15) * mm});
            skLineSegment(sketch, "E967", {"start": v(1.04, -8.15) * mm, "end": v(1.06, -8.28) * mm});
            skLineSegment(sketch, "E968", {"start": v(1.06, -8.28) * mm, "end": v(1.1, -8.4) * mm});
            skLineSegment(sketch, "E969", {"start": v(1.1, -8.4) * mm, "end": v(1.14, -8.52) * mm});
            skLineSegment(sketch, "E970", {"start": v(1.14, -8.52) * mm, "end": v(1.2, -8.63) * mm});
            skLineSegment(sketch, "E971", {"start": v(1.2, -8.63) * mm, "end": v(1.26, -8.74) * mm});
            skLineSegment(sketch, "E972", {"start": v(1.26, -8.74) * mm, "end": v(1.33, -8.84) * mm});
            skLineSegment(sketch, "E973", {"start": v(1.33, -8.84) * mm, "end": v(1.41, -8.93) * mm});
            skLineSegment(sketch, "E974", {"start": v(1.41, -8.93) * mm, "end": v(1.5, -9.02) * mm});
            skLineSegment(sketch, "E975", {"start": v(1.5, -9.02) * mm, "end": v(1.6, -9.09) * mm});
            skLineSegment(sketch, "E976", {"start": v(1.6, -9.09) * mm, "end": v(1.71, -9.15) * mm});
            skLineSegment(sketch, "E977", {"start": v(1.71, -9.15) * mm, "end": v(1.82, -9.2) * mm});
            skLineSegment(sketch, "E978", {"start": v(1.82, -9.2) * mm, "end": v(1.94, -9.25) * mm});
            skLineSegment(sketch, "E979", {"start": v(1.94, -9.25) * mm, "end": v(2.07, -9.28) * mm});
            skLineSegment(sketch, "E980", {"start": v(2.07, -9.28) * mm, "end": v(2.2, -9.3) * mm});
            skLineSegment(sketch, "E981", {"start": v(2.2, -9.3) * mm, "end": v(2.33, -9.31) * mm});
            skLineSegment(sketch, "E982", {"start": v(2.33, -9.31) * mm, "end": v(2.44, -9.31) * mm});
            skLineSegment(sketch, "E983", {"start": v(2.44, -9.31) * mm, "end": v(2.55, -9.31) * mm});
            skLineSegment(sketch, "E984", {"start": v(2.55, -9.31) * mm, "end": v(2.67, -9.31) * mm});
            skLineSegment(sketch, "E985", {"start": v(2.67, -9.31) * mm, "end": v(2.78, -9.31) * mm});
            skLineSegment(sketch, "E986", {"start": v(2.78, -9.31) * mm, "end": v(2.9, -9.31) * mm});
            skLineSegment(sketch, "E987", {"start": v(2.9, -9.31) * mm, "end": v(3, -9.31) * mm});
            skLineSegment(sketch, "E988", {"start": v(3, -9.31) * mm, "end": v(3.12, -9.31) * mm});
            skLineSegment(sketch, "E989", {"start": v(3.12, -9.31) * mm, "end": v(3.23, -9.31) * mm});
            skLineSegment(sketch, "E990", {"start": v(3.23, -9.31) * mm, "end": v(3.35, -9.31) * mm});
            skLineSegment(sketch, "E991", {"start": v(3.35, -9.31) * mm, "end": v(3.46, -9.31) * mm});
            skLineSegment(sketch, "E992", {"start": v(3.46, -9.31) * mm, "end": v(3.57, -9.31) * mm});
            skLineSegment(sketch, "E993", {"start": v(3.57, -9.31) * mm, "end": v(3.69, -9.31) * mm});
            skLineSegment(sketch, "E994", {"start": v(3.69, -9.31) * mm, "end": v(3.8, -9.31) * mm});
            skLineSegment(sketch, "E995", {"start": v(3.8, -9.31) * mm, "end": v(3.91, -9.31) * mm});
            skLineSegment(sketch, "E996", {"start": v(3.91, -9.31) * mm, "end": v(4.02, -9.31) * mm});
            skLineSegment(sketch, "E997", {"start": v(4.02, -9.31) * mm, "end": v(4.14, -9.31) * mm});
            skLineSegment(sketch, "E998", {"start": v(4.14, -9.31) * mm, "end": v(4.14, -9.44) * mm});
            skLineSegment(sketch, "E999", {"start": v(4.14, -9.44) * mm, "end": v(4.14, -9.57) * mm});
            skLineSegment(sketch, "E1000", {"start": v(4.14, -9.57) * mm, "end": v(4.14, -9.7) * mm});
            skLineSegment(sketch, "E1001", {"start": v(4.14, -9.7) * mm, "end": v(4.14, -9.83) * mm});
            skLineSegment(sketch, "E1002", {"start": v(4.14, -9.83) * mm, "end": v(4.14, -9.96) * mm});
            skLineSegment(sketch, "E1003", {"start": v(4.14, -9.96) * mm, "end": v(4.14, -10.09) * mm});
            skLineSegment(sketch, "E1004", {"start": v(4.14, -10.09) * mm, "end": v(4.14, -10.22) * mm});
            skLineSegment(sketch, "E1005", {"start": v(4.14, -10.22) * mm, "end": v(4.14, -10.34) * mm});
            skLineSegment(sketch, "E1006", {"start": v(4.14, -10.34) * mm, "end": v(4.14, -10.47) * mm});
            skLineSegment(sketch, "E1007", {"start": v(4.14, -10.47) * mm, "end": v(4.14, -10.6) * mm});
            skLineSegment(sketch, "E1008", {"start": v(4.14, -10.6) * mm, "end": v(4.14, -10.73) * mm});
            skLineSegment(sketch, "E1009", {"start": v(4.14, -10.73) * mm, "end": v(4.14, -10.86) * mm});
            skLineSegment(sketch, "E1010", {"start": v(4.14, -10.86) * mm, "end": v(4.14, -11) * mm});
            skLineSegment(sketch, "E1011", {"start": v(4.14, -11) * mm, "end": v(4.14, -11.12) * mm});
            skLineSegment(sketch, "E1012", {"start": v(4.14, -11.12) * mm, "end": v(4.14, -11.25) * mm});
            skLineSegment(sketch, "E1013", {"start": v(4.14, -11.25) * mm, "end": v(4.14, -11.38) * mm});
            skLineSegment(sketch, "E1014", {"start": v(4.14, -11.38) * mm, "end": v(4.14, -11.6) * mm});
            skLineSegment(sketch, "E1015", {"start": v(4.14, -11.6) * mm, "end": v(4.14, -11.83) * mm});
            skLineSegment(sketch, "E1016", {"start": v(4.14, -11.83) * mm, "end": v(4.14, -12.06) * mm});
            skLineSegment(sketch, "E1017", {"start": v(4.14, -12.06) * mm, "end": v(4.14, -12.28) * mm});
            skLineSegment(sketch, "E1018", {"start": v(4.14, -12.28) * mm, "end": v(4.14, -12.51) * mm});
            skLineSegment(sketch, "E1019", {"start": v(4.14, -12.51) * mm, "end": v(4.14, -12.74) * mm});
            skLineSegment(sketch, "E1020", {"start": v(4.14, -12.74) * mm, "end": v(4.14, -12.96) * mm});
            skLineSegment(sketch, "E1021", {"start": v(4.14, -12.96) * mm, "end": v(4.14, -13.19) * mm});
            skLineSegment(sketch, "E1022", {"start": v(4.14, -13.19) * mm, "end": v(4.14, -13.42) * mm});
            skLineSegment(sketch, "E1023", {"start": v(4.14, -13.42) * mm, "end": v(4.14, -13.64) * mm});
            skLineSegment(sketch, "E1024", {"start": v(4.14, -13.64) * mm, "end": v(4.14, -13.87) * mm});
            skLineSegment(sketch, "E1025", {"start": v(4.14, -13.87) * mm, "end": v(4.14, -14.1) * mm});
            skLineSegment(sketch, "E1026", {"start": v(4.14, -14.1) * mm, "end": v(4.14, -14.32) * mm});
            skLineSegment(sketch, "E1027", {"start": v(4.14, -14.32) * mm, "end": v(4.14, -14.55) * mm});
            skLineSegment(sketch, "E1028", {"start": v(4.14, -14.55) * mm, "end": v(4.14, -14.77) * mm});
            skLineSegment(sketch, "E1029", {"start": v(4.14, -14.77) * mm, "end": v(4.14, -15) * mm});
            skLineSegment(sketch, "E1030", {"start": v(4.14, -15) * mm, "end": v(4.27, -14.95) * mm});
            skLineSegment(sketch, "E1031", {"start": v(4.27, -14.95) * mm, "end": v(4.4, -14.9) * mm});
            skLineSegment(sketch, "E1032", {"start": v(4.4, -14.9) * mm, "end": v(4.53, -14.84) * mm});
            skLineSegment(sketch, "E1033", {"start": v(4.53, -14.84) * mm, "end": v(4.66, -14.8) * mm});
            skLineSegment(sketch, "E1034", {"start": v(4.66, -14.8) * mm, "end": v(4.78, -14.74) * mm});
            skLineSegment(sketch, "E1035", {"start": v(4.78, -14.74) * mm, "end": v(4.91, -14.69) * mm});
            skLineSegment(sketch, "E1036", {"start": v(4.91, -14.69) * mm, "end": v(5.04, -14.64) * mm});
            skLineSegment(sketch, "E1037", {"start": v(5.04, -14.64) * mm, "end": v(5.17, -14.59) * mm});
            skLineSegment(sketch, "E1038", {"start": v(5.17, -14.59) * mm, "end": v(5.3, -14.53) * mm});
            skLineSegment(sketch, "E1039", {"start": v(5.3, -14.53) * mm, "end": v(5.43, -14.48) * mm});
            skLineSegment(sketch, "E1040", {"start": v(5.43, -14.48) * mm, "end": v(5.56, -14.43) * mm});
            skLineSegment(sketch, "E1041", {"start": v(5.56, -14.43) * mm, "end": v(5.69, -14.38) * mm});
            skLineSegment(sketch, "E1042", {"start": v(5.69, -14.38) * mm, "end": v(5.82, -14.33) * mm});
            skLineSegment(sketch, "E1043", {"start": v(5.82, -14.33) * mm, "end": v(5.95, -14.28) * mm});
            skLineSegment(sketch, "E1044", {"start": v(5.95, -14.28) * mm, "end": v(6.08, -14.22) * mm});
            skLineSegment(sketch, "E1045", {"start": v(6.08, -14.22) * mm, "end": v(6.2, -14.17) * mm});
            skLineSegment(sketch, "E1046", {"start": v(6.2, -14.17) * mm, "end": v(6.24, -14.16) * mm});
            skLineSegment(sketch, "E1047", {"start": v(6.24, -14.16) * mm, "end": v(6.27, -14.15) * mm});
            skLineSegment(sketch, "E1048", {"start": v(6.27, -14.15) * mm, "end": v(6.3, -14.13) * mm});
            skLineSegment(sketch, "E1049", {"start": v(6.3, -14.13) * mm, "end": v(6.34, -14.12) * mm});
            skLineSegment(sketch, "E1050", {"start": v(6.34, -14.12) * mm, "end": v(6.37, -14.1) * mm});
            skLineSegment(sketch, "E1051", {"start": v(6.37, -14.1) * mm, "end": v(6.4, -14.1) * mm});
            skLineSegment(sketch, "E1052", {"start": v(6.4, -14.1) * mm, "end": v(6.43, -14.08) * mm});
            skLineSegment(sketch, "E1053", {"start": v(6.43, -14.08) * mm, "end": v(6.47, -14.07) * mm});
            skLineSegment(sketch, "E1054", {"start": v(6.47, -14.07) * mm, "end": v(6.5, -14.06) * mm});
            skLineSegment(sketch, "E1055", {"start": v(6.5, -14.06) * mm, "end": v(6.53, -14.04) * mm});
            skLineSegment(sketch, "E1056", {"start": v(6.53, -14.04) * mm, "end": v(6.56, -14.03) * mm});
            skLineSegment(sketch, "E1057", {"start": v(6.56, -14.03) * mm, "end": v(6.6, -14.02) * mm});
            skLineSegment(sketch, "E1058", {"start": v(6.6, -14.02) * mm, "end": v(6.63, -14) * mm});
            skLineSegment(sketch, "E1059", {"start": v(6.63, -14) * mm, "end": v(6.66, -14) * mm});
            skLineSegment(sketch, "E1060", {"start": v(6.66, -14) * mm, "end": v(6.7, -13.98) * mm});
            skLineSegment(sketch, "E1061", {"start": v(6.7, -13.98) * mm, "end": v(6.72, -13.97) * mm});
            skLineSegment(sketch, "E1062", {"start": v(6.72, -13.97) * mm, "end": v(6.86, -13.65) * mm});
            skLineSegment(sketch, "E1063", {"start": v(6.86, -13.65) * mm, "end": v(7, -13.33) * mm});
            skLineSegment(sketch, "E1064", {"start": v(7, -13.33) * mm, "end": v(7.12, -13) * mm});
            skLineSegment(sketch, "E1065", {"start": v(7.12, -13) * mm, "end": v(7.26, -12.69) * mm});
            skLineSegment(sketch, "E1066", {"start": v(7.26, -12.69) * mm, "end": v(7.39, -12.37) * mm});
            skLineSegment(sketch, "E1067", {"start": v(7.39, -12.37) * mm, "end": v(7.52, -12.05) * mm});
            skLineSegment(sketch, "E1068", {"start": v(7.52, -12.05) * mm, "end": v(7.66, -11.73) * mm});
            skLineSegment(sketch, "E1069", {"start": v(7.66, -11.73) * mm, "end": v(7.79, -11.4) * mm});
            skLineSegment(sketch, "E1070", {"start": v(7.79, -11.4) * mm, "end": v(7.92, -11.1) * mm});
            skLineSegment(sketch, "E1071", {"start": v(7.92, -11.1) * mm, "end": v(8.06, -10.77) * mm});
            skLineSegment(sketch, "E1072", {"start": v(8.06, -10.77) * mm, "end": v(8.19, -10.45) * mm});
            skLineSegment(sketch, "E1073", {"start": v(8.19, -10.45) * mm, "end": v(8.32, -10.13) * mm});
            skLineSegment(sketch, "E1074", {"start": v(8.32, -10.13) * mm, "end": v(8.45, -9.81) * mm});
            skLineSegment(sketch, "E1075", {"start": v(8.45, -9.81) * mm, "end": v(8.59, -9.5) * mm});
            skLineSegment(sketch, "E1076", {"start": v(8.59, -9.5) * mm, "end": v(8.72, -9.17) * mm});
            skLineSegment(sketch, "E1077", {"start": v(8.72, -9.17) * mm, "end": v(8.85, -8.85) * mm});
            skLineSegment(sketch, "E1078", {"start": v(8.85, -8.85) * mm, "end": v(9.17, -8.72) * mm});
            skLineSegment(sketch, "E1079", {"start": v(9.17, -8.72) * mm, "end": v(9.5, -8.59) * mm});
            skLineSegment(sketch, "E1080", {"start": v(9.5, -8.59) * mm, "end": v(9.81, -8.45) * mm});
            skLineSegment(sketch, "E1081", {"start": v(9.81, -8.45) * mm, "end": v(10.13, -8.32) * mm});
            skLineSegment(sketch, "E1082", {"start": v(10.13, -8.32) * mm, "end": v(10.45, -8.19) * mm});
            skLineSegment(sketch, "E1083", {"start": v(10.45, -8.19) * mm, "end": v(10.77, -8.06) * mm});
            skLineSegment(sketch, "E1084", {"start": v(10.77, -8.06) * mm, "end": v(11.1, -7.92) * mm});
            skLineSegment(sketch, "E1085", {"start": v(11.1, -7.92) * mm, "end": v(11.4, -7.79) * mm});
            skLineSegment(sketch, "E1086", {"start": v(11.4, -7.79) * mm, "end": v(11.73, -7.66) * mm});
            skLineSegment(sketch, "E1087", {"start": v(11.73, -7.66) * mm, "end": v(12.05, -7.52) * mm});
            skLineSegment(sketch, "E1088", {"start": v(12.05, -7.52) * mm, "end": v(12.37, -7.39) * mm});
            skLineSegment(sketch, "E1089", {"start": v(12.37, -7.39) * mm, "end": v(12.69, -7.26) * mm});
            skLineSegment(sketch, "E1090", {"start": v(12.69, -7.26) * mm, "end": v(13, -7.12) * mm});
            skLineSegment(sketch, "E1091", {"start": v(13, -7.12) * mm, "end": v(13.33, -7) * mm});
            skLineSegment(sketch, "E1092", {"start": v(13.33, -7) * mm, "end": v(13.65, -6.86) * mm});
            skLineSegment(sketch, "E1093", {"start": v(13.65, -6.86) * mm, "end": v(13.97, -6.72) * mm});
            skLineSegment(sketch, "E1094", {"start": v(13.97, -6.72) * mm, "end": v(13.98, -6.7) * mm});
            skLineSegment(sketch, "E1095", {"start": v(13.98, -6.7) * mm, "end": v(14, -6.66) * mm});
            skLineSegment(sketch, "E1096", {"start": v(14, -6.66) * mm, "end": v(14, -6.63) * mm});
            skLineSegment(sketch, "E1097", {"start": v(14, -6.63) * mm, "end": v(14.02, -6.6) * mm});
            skLineSegment(sketch, "E1098", {"start": v(14.02, -6.6) * mm, "end": v(14.03, -6.56) * mm});
            skLineSegment(sketch, "E1099", {"start": v(14.03, -6.56) * mm, "end": v(14.04, -6.53) * mm});
            skLineSegment(sketch, "E1100", {"start": v(14.04, -6.53) * mm, "end": v(14.06, -6.5) * mm});
            skLineSegment(sketch, "E1101", {"start": v(14.06, -6.5) * mm, "end": v(14.07, -6.47) * mm});
            skLineSegment(sketch, "E1102", {"start": v(14.07, -6.47) * mm, "end": v(14.08, -6.43) * mm});
            skLineSegment(sketch, "E1103", {"start": v(14.08, -6.43) * mm, "end": v(14.1, -6.4) * mm});
            skLineSegment(sketch, "E1104", {"start": v(14.1, -6.4) * mm, "end": v(14.1, -6.37) * mm});
            skLineSegment(sketch, "E1105", {"start": v(14.1, -6.37) * mm, "end": v(14.12, -6.34) * mm});
            skLineSegment(sketch, "E1106", {"start": v(14.12, -6.34) * mm, "end": v(14.13, -6.3) * mm});
            skLineSegment(sketch, "E1107", {"start": v(14.13, -6.3) * mm, "end": v(14.15, -6.27) * mm});
            skLineSegment(sketch, "E1108", {"start": v(14.15, -6.27) * mm, "end": v(14.16, -6.24) * mm});
            skLineSegment(sketch, "E1109", {"start": v(14.16, -6.24) * mm, "end": v(14.17, -6.2) * mm});
            skLineSegment(sketch, "E1110", {"start": v(14.17, -6.2) * mm, "end": v(14.22, -6.08) * mm});
            skLineSegment(sketch, "E1111", {"start": v(14.22, -6.08) * mm, "end": v(14.28, -5.95) * mm});
            skLineSegment(sketch, "E1112", {"start": v(14.28, -5.95) * mm, "end": v(14.33, -5.82) * mm});
            skLineSegment(sketch, "E1113", {"start": v(14.33, -5.82) * mm, "end": v(14.38, -5.69) * mm});
            skLineSegment(sketch, "E1114", {"start": v(14.38, -5.69) * mm, "end": v(14.43, -5.56) * mm});
            skLineSegment(sketch, "E1115", {"start": v(14.43, -5.56) * mm, "end": v(14.48, -5.43) * mm});
            skLineSegment(sketch, "E1116", {"start": v(14.48, -5.43) * mm, "end": v(14.53, -5.3) * mm});
            skLineSegment(sketch, "E1117", {"start": v(14.53, -5.3) * mm, "end": v(14.59, -5.17) * mm});
            skLineSegment(sketch, "E1118", {"start": v(14.59, -5.17) * mm, "end": v(14.64, -5.04) * mm});
            skLineSegment(sketch, "E1119", {"start": v(14.64, -5.04) * mm, "end": v(14.69, -4.91) * mm});
            skLineSegment(sketch, "E1120", {"start": v(14.69, -4.91) * mm, "end": v(14.74, -4.78) * mm});
            skLineSegment(sketch, "E1121", {"start": v(14.74, -4.78) * mm, "end": v(14.8, -4.66) * mm});
            skLineSegment(sketch, "E1122", {"start": v(14.8, -4.66) * mm, "end": v(14.84, -4.53) * mm});
            skLineSegment(sketch, "E1123", {"start": v(14.84, -4.53) * mm, "end": v(14.9, -4.4) * mm});
            skLineSegment(sketch, "E1124", {"start": v(14.9, -4.4) * mm, "end": v(14.95, -4.27) * mm});
            skLineSegment(sketch, "E1125", {"start": v(14.95, -4.27) * mm, "end": v(15, -4.14) * mm});
            skLineSegment(sketch, "E1126", {"start": v(15, -4.14) * mm, "end": v(14.77, -4.14) * mm});
            skLineSegment(sketch, "E1127", {"start": v(14.77, -4.14) * mm, "end": v(14.55, -4.14) * mm});
            skLineSegment(sketch, "E1128", {"start": v(14.55, -4.14) * mm, "end": v(14.32, -4.14) * mm});
            skLineSegment(sketch, "E1129", {"start": v(14.32, -4.14) * mm, "end": v(14.1, -4.14) * mm});
            skLineSegment(sketch, "E1130", {"start": v(14.1, -4.14) * mm, "end": v(13.87, -4.14) * mm});
            skLineSegment(sketch, "E1131", {"start": v(13.87, -4.14) * mm, "end": v(13.64, -4.14) * mm});
            skLineSegment(sketch, "E1132", {"start": v(13.64, -4.14) * mm, "end": v(13.42, -4.14) * mm});
            skLineSegment(sketch, "E1133", {"start": v(13.42, -4.14) * mm, "end": v(13.19, -4.14) * mm});
            skLineSegment(sketch, "E1134", {"start": v(13.19, -4.14) * mm, "end": v(12.96, -4.14) * mm});
            skLineSegment(sketch, "E1135", {"start": v(12.96, -4.14) * mm, "end": v(12.74, -4.14) * mm});
            skLineSegment(sketch, "E1136", {"start": v(12.74, -4.14) * mm, "end": v(12.51, -4.14) * mm});
            skLineSegment(sketch, "E1137", {"start": v(12.51, -4.14) * mm, "end": v(12.28, -4.14) * mm});
            skLineSegment(sketch, "E1138", {"start": v(12.28, -4.14) * mm, "end": v(12.06, -4.14) * mm});
            skLineSegment(sketch, "E1139", {"start": v(12.06, -4.14) * mm, "end": v(11.83, -4.14) * mm});
            skLineSegment(sketch, "E1140", {"start": v(11.83, -4.14) * mm, "end": v(11.6, -4.14) * mm});
            skLineSegment(sketch, "E1141", {"start": v(11.6, -4.14) * mm, "end": v(11.38, -4.14) * mm});
            skLineSegment(sketch, "E1142", {"start": v(11.38, -4.14) * mm, "end": v(11.25, -4.14) * mm});
            skLineSegment(sketch, "E1143", {"start": v(11.25, -4.14) * mm, "end": v(11.12, -4.14) * mm});
            skLineSegment(sketch, "E1144", {"start": v(11.12, -4.14) * mm, "end": v(11, -4.14) * mm});
            skLineSegment(sketch, "E1145", {"start": v(11, -4.14) * mm, "end": v(10.86, -4.14) * mm});
            skLineSegment(sketch, "E1146", {"start": v(10.86, -4.14) * mm, "end": v(10.73, -4.14) * mm});
            skLineSegment(sketch, "E1147", {"start": v(10.73, -4.14) * mm, "end": v(10.6, -4.14) * mm});
            skLineSegment(sketch, "E1148", {"start": v(10.6, -4.14) * mm, "end": v(10.47, -4.14) * mm});
            skLineSegment(sketch, "E1149", {"start": v(10.47, -4.14) * mm, "end": v(10.34, -4.14) * mm});
            skLineSegment(sketch, "E1150", {"start": v(10.34, -4.14) * mm, "end": v(10.22, -4.14) * mm});
            skLineSegment(sketch, "E1151", {"start": v(10.22, -4.14) * mm, "end": v(10.09, -4.14) * mm});
            skLineSegment(sketch, "E1152", {"start": v(10.09, -4.14) * mm, "end": v(9.96, -4.14) * mm});
            skLineSegment(sketch, "E1153", {"start": v(9.96, -4.14) * mm, "end": v(9.83, -4.14) * mm});
            skLineSegment(sketch, "E1154", {"start": v(9.83, -4.14) * mm, "end": v(9.7, -4.14) * mm});
            skLineSegment(sketch, "E1155", {"start": v(9.7, -4.14) * mm, "end": v(9.57, -4.14) * mm});
            skLineSegment(sketch, "E1156", {"start": v(9.57, -4.14) * mm, "end": v(9.44, -4.14) * mm});
            skLineSegment(sketch, "E1157", {"start": v(9.44, -4.14) * mm, "end": v(9.31, -4.14) * mm});
            skLineSegment(sketch, "E1158", {"start": v(-1.03, -1.03) * mm, "end": v(-1.03, -0.9) * mm});
            skLineSegment(sketch, "E1159", {"start": v(-1.03, -0.9) * mm, "end": v(-1.03, -0.78) * mm});
            skLineSegment(sketch, "E1160", {"start": v(-1.03, -0.78) * mm, "end": v(-1.03, -0.65) * mm});
            skLineSegment(sketch, "E1161", {"start": v(-1.03, -0.65) * mm, "end": v(-1.03, -0.52) * mm});
            skLineSegment(sketch, "E1162", {"start": v(-1.03, -0.52) * mm, "end": v(-1.03, -0.39) * mm});
            skLineSegment(sketch, "E1163", {"start": v(-1.03, -0.39) * mm, "end": v(-1.03, -0.26) * mm});
            skLineSegment(sketch, "E1164", {"start": v(-1.03, -0.26) * mm, "end": v(-1.03, -0.13) * mm});
            skLineSegment(sketch, "E1165", {"start": v(-1.03, -0.13) * mm, "end": v(-1.03, 0) * mm});
            skLineSegment(sketch, "E1166", {"start": v(-1.03, 0) * mm, "end": v(-1.03, 0.13) * mm});
            skLineSegment(sketch, "E1167", {"start": v(-1.03, 0.13) * mm, "end": v(-1.03, 0.26) * mm});
            skLineSegment(sketch, "E1168", {"start": v(-1.03, 0.26) * mm, "end": v(-1.03, 0.39) * mm});
            skLineSegment(sketch, "E1169", {"start": v(-1.03, 0.39) * mm, "end": v(-1.03, 0.52) * mm});
            skLineSegment(sketch, "E1170", {"start": v(-1.03, 0.52) * mm, "end": v(-1.03, 0.65) * mm});
            skLineSegment(sketch, "E1171", {"start": v(-1.03, 0.65) * mm, "end": v(-1.03, 0.78) * mm});
            skLineSegment(sketch, "E1172", {"start": v(-1.03, 0.78) * mm, "end": v(-1.03, 0.9) * mm});
            skLineSegment(sketch, "E1173", {"start": v(-1.03, 0.9) * mm, "end": v(-1.03, 1.03) * mm});
            skLineSegment(sketch, "E1174", {"start": v(-1.03, 1.03) * mm, "end": v(-0.9, 1.03) * mm});
            skLineSegment(sketch, "E1175", {"start": v(-0.9, 1.03) * mm, "end": v(-0.78, 1.03) * mm});
            skLineSegment(sketch, "E1176", {"start": v(-0.78, 1.03) * mm, "end": v(-0.65, 1.03) * mm});
            skLineSegment(sketch, "E1177", {"start": v(-0.65, 1.03) * mm, "end": v(-0.52, 1.03) * mm});
            skLineSegment(sketch, "E1178", {"start": v(-0.52, 1.03) * mm, "end": v(-0.39, 1.03) * mm});
            skLineSegment(sketch, "E1179", {"start": v(-0.39, 1.03) * mm, "end": v(-0.26, 1.03) * mm});
            skLineSegment(sketch, "E1180", {"start": v(-0.26, 1.03) * mm, "end": v(-0.13, 1.03) * mm});
            skLineSegment(sketch, "E1181", {"start": v(-0.13, 1.03) * mm, "end": v(0, 1.03) * mm});
            skLineSegment(sketch, "E1182", {"start": v(0, 1.03) * mm, "end": v(0.13, 1.03) * mm});
            skLineSegment(sketch, "E1183", {"start": v(0.13, 1.03) * mm, "end": v(0.26, 1.03) * mm});
            skLineSegment(sketch, "E1184", {"start": v(0.26, 1.03) * mm, "end": v(0.39, 1.03) * mm});
            skLineSegment(sketch, "E1185", {"start": v(0.39, 1.03) * mm, "end": v(0.52, 1.03) * mm});
            skLineSegment(sketch, "E1186", {"start": v(0.52, 1.03) * mm, "end": v(0.65, 1.03) * mm});
            skLineSegment(sketch, "E1187", {"start": v(0.65, 1.03) * mm, "end": v(0.78, 1.03) * mm});
            skLineSegment(sketch, "E1188", {"start": v(0.78, 1.03) * mm, "end": v(0.9, 1.03) * mm});
            skLineSegment(sketch, "E1189", {"start": v(0.9, 1.03) * mm, "end": v(1.03, 1.03) * mm});
            skLineSegment(sketch, "E1190", {"start": v(1.03, 1.03) * mm, "end": v(1.03, 0.9) * mm});
            skLineSegment(sketch, "E1191", {"start": v(1.03, 0.9) * mm, "end": v(1.03, 0.78) * mm});
            skLineSegment(sketch, "E1192", {"start": v(1.03, 0.78) * mm, "end": v(1.03, 0.65) * mm});
            skLineSegment(sketch, "E1193", {"start": v(1.03, 0.65) * mm, "end": v(1.03, 0.52) * mm});
            skLineSegment(sketch, "E1194", {"start": v(1.03, 0.52) * mm, "end": v(1.03, 0.39) * mm});
            skLineSegment(sketch, "E1195", {"start": v(1.03, 0.39) * mm, "end": v(1.03, 0.26) * mm});
            skLineSegment(sketch, "E1196", {"start": v(1.03, 0.26) * mm, "end": v(1.03, 0.13) * mm});
            skLineSegment(sketch, "E1197", {"start": v(1.03, 0.13) * mm, "end": v(1.03, 0) * mm});
            skLineSegment(sketch, "E1198", {"start": v(1.03, 0) * mm, "end": v(1.03, -0.13) * mm});
            skLineSegment(sketch, "E1199", {"start": v(1.03, -0.13) * mm, "end": v(1.03, -0.26) * mm});
            skLineSegment(sketch, "E1200", {"start": v(1.03, -0.26) * mm, "end": v(1.03, -0.39) * mm});
            skLineSegment(sketch, "E1201", {"start": v(1.03, -0.39) * mm, "end": v(1.03, -0.52) * mm});
            skLineSegment(sketch, "E1202", {"start": v(1.03, -0.52) * mm, "end": v(1.03, -0.65) * mm});
            skLineSegment(sketch, "E1203", {"start": v(1.03, -0.65) * mm, "end": v(1.03, -0.78) * mm});
            skLineSegment(sketch, "E1204", {"start": v(1.03, -0.78) * mm, "end": v(1.03, -0.9) * mm});
            skLineSegment(sketch, "E1205", {"start": v(1.03, -0.9) * mm, "end": v(1.03, -1.03) * mm});
            skLineSegment(sketch, "E1206", {"start": v(1.03, -1.03) * mm, "end": v(0.9, -1.03) * mm});
            skLineSegment(sketch, "E1207", {"start": v(0.9, -1.03) * mm, "end": v(0.78, -1.03) * mm});
            skLineSegment(sketch, "E1208", {"start": v(0.78, -1.03) * mm, "end": v(0.65, -1.03) * mm});
            skLineSegment(sketch, "E1209", {"start": v(0.65, -1.03) * mm, "end": v(0.52, -1.03) * mm});
            skLineSegment(sketch, "E1210", {"start": v(0.52, -1.03) * mm, "end": v(0.39, -1.03) * mm});
            skLineSegment(sketch, "E1211", {"start": v(0.39, -1.03) * mm, "end": v(0.26, -1.03) * mm});
            skLineSegment(sketch, "E1212", {"start": v(0.26, -1.03) * mm, "end": v(0.13, -1.03) * mm});
            skLineSegment(sketch, "E1213", {"start": v(0.13, -1.03) * mm, "end": v(0, -1.03) * mm});
            skLineSegment(sketch, "E1214", {"start": v(0, -1.03) * mm, "end": v(-0.13, -1.03) * mm});
            skLineSegment(sketch, "E1215", {"start": v(-0.13, -1.03) * mm, "end": v(-0.26, -1.03) * mm});
            skLineSegment(sketch, "E1216", {"start": v(-0.26, -1.03) * mm, "end": v(-0.39, -1.03) * mm});
            skLineSegment(sketch, "E1217", {"start": v(-0.39, -1.03) * mm, "end": v(-0.52, -1.03) * mm});
            skLineSegment(sketch, "E1218", {"start": v(-0.52, -1.03) * mm, "end": v(-0.65, -1.03) * mm});
            skLineSegment(sketch, "E1219", {"start": v(-0.65, -1.03) * mm, "end": v(-0.78, -1.03) * mm});
            skLineSegment(sketch, "E1220", {"start": v(-0.78, -1.03) * mm, "end": v(-0.9, -1.03) * mm});
            skLineSegment(sketch, "E1221", {"start": v(-0.9, -1.03) * mm, "end": v(-1.03, -1.03) * mm});
            skLineSegment(sketch, "E1222.bottom", {"start": v(-1.23, 1.27) * mm, "end": v(1.39, 1.27) * mm});
            skLineSegment(sketch, "E1222.top", {"start": v(-1.23, -1.26) * mm, "end": v(1.39, -1.26) * mm});
            skLineSegment(sketch, "E1222.left", {"start": v(-1.23, 1.27) * mm, "end": v(-1.23, -1.26) * mm});
            skLineSegment(sketch, "E1222.right", {"start": v(1.39, 1.27) * mm, "end": v(1.39, -1.26) * mm});
            skSolve(sketch);
        }
        {
            var Q0;
            Q0=makeQuery(id+"F3.imprint","IMPRINT",FACE,{"disambiguationData":[TD([[makeQuery(id+"F3.imprint","IMPRINT",EDGE,{"derivedFrom":sQuery(id+"F3.wireOp",EDGE,"E6")}),1.0]])]});
            var Q1;
            Q1=makeQuery(id+"F3.imprint","IMPRINT",FACE,{"disambiguationData":[TD([[makeQuery(id+"F3.imprint","IMPRINT",EDGE,{"derivedFrom":sQuery(id+"F3.wireOp",EDGE,"E1158")}),1.0]])]});
            extrude(context, id + "F4", {"entities" : qUnion([Q0, Q1]), "operationType" : NewBodyOperationType.REMOVE, "oppositeDirection" : true, "depth" : 12 * mm, "offsetDistance" : 25 * mm});
        }
        {
            var Q0;
            Q0=qCreatedBy(makeId("Front.planeOp"),FACE);
            var sketch = newSketch(context, id + "F5", { "sketchPlane" : qUnion([Q0])});
            skArc(sketch, "E1223.0", {"start": v(-13.67, 7.7) * mm, "mid": v(-17.92, 5.68) * mm, "end": v(-15, 2) * mm});
            skArc(sketch, "E1223.1", {"start": v(-13.67, 7.7) * mm, "mid": v(-7.02, 5.3) * mm, "end": v(0, 4.5) * mm});
            skLineSegment(sketch, "E1223.2", {"start": v(0, 2) * mm, "end": v(0, 4.5) * mm});
            skLineSegment(sketch, "E1223.3", {"start": v(0, 2) * mm, "end": v(-15, 2) * mm});
            skSolve(sketch);
        }
        {
            var Q0;
            Q0=qSketchRegion(id+"F5",true);
            var Q1;
            Q1=sQuery(id+"F0.wireOp",EDGE,"E3");
            revolve(context, id + "F6", {"operationType" : NewBodyOperationType.ADD, "surfaceOperationType" : NewSurfaceOperationType.NEW, "entities" : qUnion([Q0]), "axis" : qUnion([Q1]), "revolveType" : RevolveType.FULL});
        }
        {
            var Q0;
            Q0=qCreatedBy(makeId("Top.planeOp"),FACE);
            var sketch = newSketch(context, id + "F7", { "sketchPlane" : qUnion([Q0])});
            skCircle(sketch, "E1224", {"center": v(0, 21) * mm, "radius": 4 * mm});
            skSolve(sketch);
        }
        {
            var Q0;
            Q0=makeQuery(id+"F7.imprint","IMPRINT",FACE,{"disambiguationData":[TD([[makeQuery(id+"F7.imprint","IMPRINT",EDGE,{"derivedFrom":sQuery(id+"F7.wireOp",EDGE,"E1224")}),1.0]])]});
            extrude(context, id + "F8", {"entities" : qUnion([Q0]), "operationType" : NewBodyOperationType.REMOVE, "depth" : 25 * mm, "offsetDistance" : 25 * mm});
        }
        {
            var Q0;
            Q0=makeQuery(id+"F8.boolean.opBoolean","INTERSECT",EDGE,{"derivedFrom":[makeQuery(id+"F4.boolean.opBoolean","SPLIT",FACE,{"disambiguationData":[TD([makeQuery(id+"F1.opRevolve","SWEPT_FACE",FACE,{"disambiguationData":[OSD([sQuery(id+"F0.wireOp",EDGE,"E2")])]}),makeQuery(id+"F4.opExtrude","SWEPT_FACE",FACE,{"disambiguationData":[OSD([sQuery(id+"F3.wireOp",EDGE,"705da5c4-06c6-4740-92ce-35b712dfc936.0")])]}),makeQuery(id+"F4.opExtrude","SWEPT_FACE",FACE,{"disambiguationData":[OSD([sQuery(id+"F3.wireOp",EDGE,"705da5c4-06c6-4740-92ce-35b712dfc936.1")])]}),makeQuery(id+"F4.opExtrude","SWEPT_FACE",FACE,{"disambiguationData":[OSD([sQuery(id+"F3.wireOp",EDGE,"705da5c4-06c6-4740-92ce-35b712dfc936.2")])]}),makeQuery(id+"F4.opExtrude","SWEPT_FACE",FACE,{"disambiguationData":[OSD([sQuery(id+"F3.wireOp",EDGE,"705da5c4-06c6-4740-92ce-35b712dfc936.3")])]}),makeQuery(id+"F4.opExtrude","SWEPT_FACE",FACE,{"disambiguationData":[OSD([sQuery(id+"F3.wireOp",EDGE,"705da5c4-06c6-4740-92ce-35b712dfc936.4")])]}),makeQuery(id+"F4.opExtrude","SWEPT_FACE",FACE,{"disambiguationData":[OSD([sQuery(id+"F3.wireOp",EDGE,"705da5c4-06c6-4740-92ce-35b712dfc936.5")])]})])],"derivedFrom":makeQuery(id+"F1.opRevolve","SWEPT_FACE",FACE,{"disambiguationData":[OSD([sQuery(id+"F0.wireOp",EDGE,"E1")])]})}),makeQuery(id+"F8.opExtrude","SWEPT_FACE",FACE,{"disambiguationData":[OSD([sQuery(id+"F7.wireOp",EDGE,"E1224")])]})]});
            fillet(context, id + "F9", {"entities" : qUnion([Q0]), "radius" : 1 * mm, "tangentPropagation" : true, "allowEdgeOverflow" : false});
        }
        {
            var Q0;
            Q0=makeQuery(id+"F1.opRevolve","SWEPT_FACE",FACE,{"disambiguationData":[OSD([sQuery(id+"F0.wireOp",EDGE,"E2"),sQuery(id+"F0.wireOp",EDGE,"E5")])]});
            var sketch = newSketch(context, id + "F10", { "sketchPlane" : qUnion([Q0])});
            skLineSegment(sketch, "E1225", {"start": v(9.05, -10) * mm, "end": v(9.05, -9.05) * mm});
            skLineSegment(sketch, "E1226", {"start": v(9.05, -9.05) * mm, "end": v(8.1, -9.05) * mm});
            skLineSegment(sketch, "E1227", {"start": v(8.1, -9.05) * mm, "end": v(8.1, -10) * mm});
            skLineSegment(sketch, "E1228", {"start": v(8.1, -10) * mm, "end": v(9.05, -10) * mm});
            skLineSegment(sketch, "E1229", {"start": v(7.14, -8.1) * mm, "end": v(7.14, -9.05) * mm});
            skLineSegment(sketch, "E1230", {"start": v(7.14, -9.05) * mm, "end": v(8.09, -9.04) * mm});
            skLineSegment(sketch, "E1231", {"start": v(8.09, -9.04) * mm, "end": v(8.1, -8.1) * mm});
            skLineSegment(sketch, "E1232", {"start": v(8.1, -8.1) * mm, "end": v(8.1, -7.14) * mm});
            skLineSegment(sketch, "E1233", {"start": v(8.1, -7.14) * mm, "end": v(9.05, -7.14) * mm});
            skLineSegment(sketch, "E1234", {"start": v(9.05, -7.14) * mm, "end": v(9.05, -6.2) * mm});
            skLineSegment(sketch, "E1235", {"start": v(9.05, -6.2) * mm, "end": v(8.1, -6.2) * mm});
            skLineSegment(sketch, "E1236", {"start": v(8.1, -6.2) * mm, "end": v(7.14, -6.2) * mm});
            skLineSegment(sketch, "E1237", {"start": v(7.14, -6.2) * mm, "end": v(7.14, -7.14) * mm});
            skLineSegment(sketch, "E1238", {"start": v(7.14, -7.14) * mm, "end": v(7.14, -8.1) * mm});
            skLineSegment(sketch, "E1239", {"start": v(0.48, -8.1) * mm, "end": v(0.48, -7.14) * mm});
            skLineSegment(sketch, "E1240", {"start": v(0.48, -7.14) * mm, "end": v(-0.48, -7.14) * mm});
            skLineSegment(sketch, "E1241", {"start": v(-0.48, -7.14) * mm, "end": v(-0.48, -8.1) * mm});
            skLineSegment(sketch, "E1242", {"start": v(-0.48, -8.1) * mm, "end": v(0.48, -8.1) * mm});
            skLineSegment(sketch, "E1243", {"start": v(-1.43, -5.24) * mm, "end": v(-2.38, -5.24) * mm});
            skLineSegment(sketch, "E1244", {"start": v(-2.38, -5.24) * mm, "end": v(-2.38, -6.2) * mm});
            skLineSegment(sketch, "E1245", {"start": v(-2.38, -6.2) * mm, "end": v(-2.38, -7.14) * mm});
            skLineSegment(sketch, "E1246", {"start": v(-2.38, -7.14) * mm, "end": v(-2.38, -8.1) * mm});
            skLineSegment(sketch, "E1247", {"start": v(-2.38, -8.1) * mm, "end": v(-2.38, -9.05) * mm});
            skLineSegment(sketch, "E1248", {"start": v(-2.38, -9.05) * mm, "end": v(-2.38, -10) * mm});
            skLineSegment(sketch, "E1249", {"start": v(-2.38, -10) * mm, "end": v(-1.43, -10) * mm});
            skLineSegment(sketch, "E1250", {"start": v(-1.43, -10) * mm, "end": v(-1.43, -9.05) * mm});
            skLineSegment(sketch, "E1251", {"start": v(-1.43, -9.05) * mm, "end": v(-0.48, -9.05) * mm});
            skLineSegment(sketch, "E1252", {"start": v(-0.48, -9.05) * mm, "end": v(-0.49, -8.1) * mm});
            skLineSegment(sketch, "E1253", {"start": v(-0.49, -8.1) * mm, "end": v(-1.43, -8.1) * mm});
            skLineSegment(sketch, "E1254", {"start": v(-1.43, -8.1) * mm, "end": v(-1.43, -7.14) * mm});
            skLineSegment(sketch, "E1255", {"start": v(-1.43, -7.14) * mm, "end": v(-0.49, -7.13) * mm});
            skLineSegment(sketch, "E1256", {"start": v(-0.49, -7.13) * mm, "end": v(-0.48, -6.2) * mm});
            skLineSegment(sketch, "E1257", {"start": v(-0.48, -6.2) * mm, "end": v(-1.43, -6.2) * mm});
            skLineSegment(sketch, "E1258", {"start": v(-1.43, -6.2) * mm, "end": v(-1.43, -5.24) * mm});
            skLineSegment(sketch, "E1259", {"start": v(-7.14, -5.24) * mm, "end": v(-8.1, -5.24) * mm});
            skLineSegment(sketch, "E1260", {"start": v(-8.1, -5.24) * mm, "end": v(-8.1, -6.2) * mm});
            skLineSegment(sketch, "E1261", {"start": v(-8.1, -6.2) * mm, "end": v(-8.1, -7.14) * mm});
            skLineSegment(sketch, "E1262", {"start": v(-8.1, -7.14) * mm, "end": v(-8.1, -8.1) * mm});
            skLineSegment(sketch, "E1263", {"start": v(-8.1, -8.1) * mm, "end": v(-7.14, -8.1) * mm});
            skLineSegment(sketch, "E1264", {"start": v(-7.14, -8.1) * mm, "end": v(-6.2, -8.1) * mm});
            skLineSegment(sketch, "E1265", {"start": v(-6.2, -8.1) * mm, "end": v(-5.24, -8.1) * mm});
            skLineSegment(sketch, "E1266", {"start": v(-5.24, -8.1) * mm, "end": v(-5.24, -7.14) * mm});
            skLineSegment(sketch, "E1267", {"start": v(-5.24, -7.14) * mm, "end": v(-5.24, -6.2) * mm});
            skLineSegment(sketch, "E1268", {"start": v(-5.24, -6.2) * mm, "end": v(-5.24, -5.24) * mm});
            skLineSegment(sketch, "E1269", {"start": v(-5.24, -5.24) * mm, "end": v(-6.2, -5.24) * mm});
            skLineSegment(sketch, "E1270", {"start": v(-6.2, -5.24) * mm, "end": v(-7.14, -5.24) * mm});
            skLineSegment(sketch, "E1271", {"start": v(2.38, -4.29) * mm, "end": v(2.38, -5.24) * mm});
            skLineSegment(sketch, "E1272", {"start": v(2.38, -5.24) * mm, "end": v(3.33, -5.24) * mm});
            skLineSegment(sketch, "E1273", {"start": v(3.33, -5.24) * mm, "end": v(3.33, -4.29) * mm});
            skLineSegment(sketch, "E1274", {"start": v(3.33, -4.29) * mm, "end": v(2.38, -4.29) * mm});
            skLineSegment(sketch, "E1275", {"start": v(1.43, -3.33) * mm, "end": v(1.43, -2.38) * mm});
            skLineSegment(sketch, "E1276", {"start": v(1.43, -2.38) * mm, "end": v(2.38, -2.38) * mm});
            skLineSegment(sketch, "E1277", {"start": v(2.38, -2.38) * mm, "end": v(2.38, -1.43) * mm});
            skLineSegment(sketch, "E1278", {"start": v(2.38, -1.43) * mm, "end": v(1.43, -1.43) * mm});
            skLineSegment(sketch, "E1279", {"start": v(1.43, -1.43) * mm, "end": v(0.48, -1.43) * mm});
            skLineSegment(sketch, "E1280", {"start": v(0.48, -1.43) * mm, "end": v(0.48, -2.38) * mm});
            skLineSegment(sketch, "E1281", {"start": v(0.48, -2.38) * mm, "end": v(-0.48, -2.38) * mm});
            skLineSegment(sketch, "E1282", {"start": v(-0.48, -2.38) * mm, "end": v(-0.47, -3.32) * mm});
            skLineSegment(sketch, "E1283", {"start": v(-0.47, -3.32) * mm, "end": v(0.48, -3.33) * mm});
            skLineSegment(sketch, "E1284", {"start": v(0.48, -3.33) * mm, "end": v(0.48, -4.29) * mm});
            skLineSegment(sketch, "E1285", {"start": v(0.48, -4.29) * mm, "end": v(-0.48, -4.29) * mm});
            skLineSegment(sketch, "E1286", {"start": v(-0.48, -4.29) * mm, "end": v(-0.48, -3.33) * mm});
            skLineSegment(sketch, "E1287", {"start": v(-0.48, -3.33) * mm, "end": v(-1.43, -3.33) * mm});
            skLineSegment(sketch, "E1288", {"start": v(-1.43, -3.33) * mm, "end": v(-1.43, -2.38) * mm});
            skLineSegment(sketch, "E1289", {"start": v(-1.43, -2.38) * mm, "end": v(-2.38, -2.38) * mm});
            skLineSegment(sketch, "E1290", {"start": v(-2.38, -2.38) * mm, "end": v(-2.38, -3.33) * mm});
            skLineSegment(sketch, "E1291", {"start": v(-2.38, -3.33) * mm, "end": v(-2.38, -4.29) * mm});
            skLineSegment(sketch, "E1292", {"start": v(-2.38, -4.29) * mm, "end": v(-1.43, -4.29) * mm});
            skLineSegment(sketch, "E1293", {"start": v(-1.43, -4.29) * mm, "end": v(-1.42, -5.23) * mm});
            skLineSegment(sketch, "E1294", {"start": v(-1.42, -5.23) * mm, "end": v(-0.48, -5.24) * mm});
            skLineSegment(sketch, "E1295", {"start": v(-0.48, -5.24) * mm, "end": v(-0.47, -6.18) * mm});
            skLineSegment(sketch, "E1296", {"start": v(-0.47, -6.18) * mm, "end": v(0.48, -6.2) * mm});
            skLineSegment(sketch, "E1297", {"start": v(0.48, -6.2) * mm, "end": v(1.43, -6.2) * mm});
            skLineSegment(sketch, "E1298", {"start": v(1.43, -6.2) * mm, "end": v(1.43, -5.24) * mm});
            skLineSegment(sketch, "E1299", {"start": v(1.43, -5.24) * mm, "end": v(1.43, -4.29) * mm});
            skLineSegment(sketch, "E1300", {"start": v(1.43, -4.29) * mm, "end": v(2.37, -4.28) * mm});
            skLineSegment(sketch, "E1301", {"start": v(2.37, -4.28) * mm, "end": v(2.38, -3.33) * mm});
            skLineSegment(sketch, "E1302", {"start": v(2.38, -3.33) * mm, "end": v(1.43, -3.33) * mm});
            skLineSegment(sketch, "E1303", {"start": v(-5.24, -3.33) * mm, "end": v(-6.2, -3.33) * mm});
            skLineSegment(sketch, "E1304", {"start": v(-6.2, -3.33) * mm, "end": v(-7.14, -3.33) * mm});
            skLineSegment(sketch, "E1305", {"start": v(-7.14, -3.33) * mm, "end": v(-8.1, -3.33) * mm});
            skLineSegment(sketch, "E1306", {"start": v(-8.1, -3.33) * mm, "end": v(-9.05, -3.33) * mm});
            skLineSegment(sketch, "E1307", {"start": v(-9.05, -3.33) * mm, "end": v(-10, -3.33) * mm});
            skLineSegment(sketch, "E1308", {"start": v(-10, -3.33) * mm, "end": v(-10, -4.29) * mm});
            skLineSegment(sketch, "E1309", {"start": v(-10, -4.29) * mm, "end": v(-10, -5.24) * mm});
            skLineSegment(sketch, "E1310", {"start": v(-10, -5.24) * mm, "end": v(-10, -6.2) * mm});
            skLineSegment(sketch, "E1311", {"start": v(-10, -6.2) * mm, "end": v(-10, -7.14) * mm});
            skLineSegment(sketch, "E1312", {"start": v(-10, -7.14) * mm, "end": v(-10, -8.1) * mm});
            skLineSegment(sketch, "E1313", {"start": v(-10, -8.1) * mm, "end": v(-10, -9.05) * mm});
            skLineSegment(sketch, "E1314", {"start": v(-10, -9.05) * mm, "end": v(-10, -10) * mm});
            skLineSegment(sketch, "E1315", {"start": v(-10, -10) * mm, "end": v(-9.05, -10) * mm});
            skLineSegment(sketch, "E1316", {"start": v(-9.05, -10) * mm, "end": v(-8.1, -10) * mm});
            skLineSegment(sketch, "E1317", {"start": v(-8.1, -10) * mm, "end": v(-7.14, -10) * mm});
            skLineSegment(sketch, "E1318", {"start": v(-7.14, -10) * mm, "end": v(-6.2, -10) * mm});
            skLineSegment(sketch, "E1319", {"start": v(-6.2, -10) * mm, "end": v(-5.24, -10) * mm});
            skLineSegment(sketch, "E1320", {"start": v(-5.24, -10) * mm, "end": v(-4.29, -10) * mm});
            skLineSegment(sketch, "E1321", {"start": v(-4.29, -10) * mm, "end": v(-3.33, -10) * mm});
            skLineSegment(sketch, "E1322", {"start": v(-3.33, -10) * mm, "end": v(-3.33, -9.05) * mm});
            skLineSegment(sketch, "E1323", {"start": v(-3.33, -9.05) * mm, "end": v(-3.33, -8.1) * mm});
            skLineSegment(sketch, "E1324", {"start": v(-3.33, -8.1) * mm, "end": v(-3.33, -7.14) * mm});
            skLineSegment(sketch, "E1325", {"start": v(-3.33, -7.14) * mm, "end": v(-3.33, -6.2) * mm});
            skLineSegment(sketch, "E1326", {"start": v(-3.33, -6.2) * mm, "end": v(-3.33, -5.24) * mm});
            skLineSegment(sketch, "E1327", {"start": v(-3.33, -5.24) * mm, "end": v(-3.33, -4.29) * mm});
            skLineSegment(sketch, "E1328", {"start": v(-3.33, -4.29) * mm, "end": v(-3.33, -3.33) * mm});
            skLineSegment(sketch, "E1329", {"start": v(-3.33, -3.33) * mm, "end": v(-4.29, -3.33) * mm});
            skLineSegment(sketch, "E1330", {"start": v(-4.29, -3.33) * mm, "end": v(-5.24, -3.33) * mm});
            skLineSegment(sketch, "E1331", {"start": v(-4.29, -5.24) * mm, "end": v(-4.29, -6.2) * mm});
            skLineSegment(sketch, "E1332", {"start": v(-4.29, -6.2) * mm, "end": v(-4.29, -7.14) * mm});
            skLineSegment(sketch, "E1333", {"start": v(-4.29, -7.14) * mm, "end": v(-4.29, -8.1) * mm});
            skLineSegment(sketch, "E1334", {"start": v(-4.29, -8.1) * mm, "end": v(-4.29, -9.05) * mm});
            skLineSegment(sketch, "E1335", {"start": v(-4.29, -9.05) * mm, "end": v(-5.24, -9.05) * mm});
            skLineSegment(sketch, "E1336", {"start": v(-5.24, -9.05) * mm, "end": v(-6.2, -9.05) * mm});
            skLineSegment(sketch, "E1337", {"start": v(-6.2, -9.05) * mm, "end": v(-7.14, -9.05) * mm});
            skLineSegment(sketch, "E1338", {"start": v(-7.14, -9.05) * mm, "end": v(-8.1, -9.05) * mm});
            skLineSegment(sketch, "E1339", {"start": v(-8.1, -9.05) * mm, "end": v(-9.05, -9.05) * mm});
            skLineSegment(sketch, "E1340", {"start": v(-9.05, -9.05) * mm, "end": v(-9.05, -8.1) * mm});
            skLineSegment(sketch, "E1341", {"start": v(-9.05, -8.1) * mm, "end": v(-9.05, -7.14) * mm});
            skLineSegment(sketch, "E1342", {"start": v(-9.05, -7.14) * mm, "end": v(-9.05, -6.2) * mm});
            skLineSegment(sketch, "E1343", {"start": v(-9.05, -6.2) * mm, "end": v(-9.05, -5.24) * mm});
            skLineSegment(sketch, "E1344", {"start": v(-9.05, -5.24) * mm, "end": v(-9.05, -4.29) * mm});
            skLineSegment(sketch, "E1345", {"start": v(-9.05, -4.29) * mm, "end": v(-8.1, -4.29) * mm});
            skLineSegment(sketch, "E1346", {"start": v(-8.1, -4.29) * mm, "end": v(-7.14, -4.29) * mm});
            skLineSegment(sketch, "E1347", {"start": v(-7.14, -4.29) * mm, "end": v(-6.2, -4.29) * mm});
            skLineSegment(sketch, "E1348", {"start": v(-6.2, -4.29) * mm, "end": v(-5.24, -4.29) * mm});
            skLineSegment(sketch, "E1349", {"start": v(-5.24, -4.29) * mm, "end": v(-4.29, -4.29) * mm});
            skLineSegment(sketch, "E1350", {"start": v(-4.29, -4.29) * mm, "end": v(-4.29, -5.24) * mm});
            skLineSegment(sketch, "E1351", {"start": v(10, -2.38) * mm, "end": v(10, -1.43) * mm});
            skLineSegment(sketch, "E1352", {"start": v(10, -1.43) * mm, "end": v(9.05, -1.43) * mm});
            skLineSegment(sketch, "E1353", {"start": v(9.05, -1.43) * mm, "end": v(9.05, -2.38) * mm});
            skLineSegment(sketch, "E1354", {"start": v(9.05, -2.38) * mm, "end": v(9.05, -3.33) * mm});
            skLineSegment(sketch, "E1355", {"start": v(9.05, -3.33) * mm, "end": v(10, -3.33) * mm});
            skLineSegment(sketch, "E1356", {"start": v(10, -3.33) * mm, "end": v(10, -2.38) * mm});
            skLineSegment(sketch, "E1357", {"start": v(-3.33, -1.43) * mm, "end": v(-4.29, -1.43) * mm});
            skLineSegment(sketch, "E1358", {"start": v(-4.29, -1.43) * mm, "end": v(-5.24, -1.43) * mm});
            skLineSegment(sketch, "E1359", {"start": v(-5.24, -1.43) * mm, "end": v(-6.2, -1.43) * mm});
            skLineSegment(sketch, "E1360", {"start": v(-6.2, -1.43) * mm, "end": v(-6.2, -2.38) * mm});
            skLineSegment(sketch, "E1361", {"start": v(-6.2, -2.38) * mm, "end": v(-5.24, -2.38) * mm});
            skLineSegment(sketch, "E1362", {"start": v(-5.24, -2.38) * mm, "end": v(-4.29, -2.38) * mm});
            skLineSegment(sketch, "E1363", {"start": v(-4.29, -2.38) * mm, "end": v(-3.33, -2.38) * mm});
            skLineSegment(sketch, "E1364", {"start": v(-3.33, -2.38) * mm, "end": v(-2.4, -2.37) * mm});
            skLineSegment(sketch, "E1365", {"start": v(-2.4, -2.37) * mm, "end": v(-2.38, -1.43) * mm});
            skLineSegment(sketch, "E1366", {"start": v(-2.38, -1.43) * mm, "end": v(-3.33, -1.43) * mm});
            skLineSegment(sketch, "E1367", {"start": v(-0.48, -1.43) * mm, "end": v(-0.48, -0.48) * mm});
            skLineSegment(sketch, "E1368", {"start": v(-0.48, -0.48) * mm, "end": v(0.48, -0.48) * mm});
            skLineSegment(sketch, "E1369", {"start": v(0.48, -0.48) * mm, "end": v(1.43, -0.48) * mm});
            skLineSegment(sketch, "E1370", {"start": v(1.43, -0.48) * mm, "end": v(2.38, -0.48) * mm});
            skLineSegment(sketch, "E1371", {"start": v(2.38, -0.48) * mm, "end": v(2.38, 0.48) * mm});
            skLineSegment(sketch, "E1372", {"start": v(2.38, 0.48) * mm, "end": v(3.33, 0.48) * mm});
            skLineSegment(sketch, "E1373", {"start": v(3.33, 0.48) * mm, "end": v(3.33, 1.43) * mm});
            skLineSegment(sketch, "E1374", {"start": v(3.33, 1.43) * mm, "end": v(3.33, 2.38) * mm});
            skLineSegment(sketch, "E1375", {"start": v(3.33, 2.38) * mm, "end": v(2.38, 2.38) * mm});
            skLineSegment(sketch, "E1376", {"start": v(2.38, 2.38) * mm, "end": v(2.38, 1.43) * mm});
            skLineSegment(sketch, "E1377", {"start": v(2.38, 1.43) * mm, "end": v(1.43, 1.43) * mm});
            skLineSegment(sketch, "E1378", {"start": v(1.43, 1.43) * mm, "end": v(1.43, 0.48) * mm});
            skLineSegment(sketch, "E1379", {"start": v(1.43, 0.48) * mm, "end": v(0.48, 0.48) * mm});
            skLineSegment(sketch, "E1380", {"start": v(0.48, 0.48) * mm, "end": v(0.48, 1.43) * mm});
            skLineSegment(sketch, "E1381", {"start": v(0.48, 1.43) * mm, "end": v(-0.48, 1.43) * mm});
            skLineSegment(sketch, "E1382", {"start": v(-0.48, 1.43) * mm, "end": v(-0.48, 2.38) * mm});
            skLineSegment(sketch, "E1383", {"start": v(-0.48, 2.38) * mm, "end": v(-1.43, 2.38) * mm});
            skLineSegment(sketch, "E1384", {"start": v(-1.43, 2.38) * mm, "end": v(-2.38, 2.38) * mm});
            skLineSegment(sketch, "E1385", {"start": v(-2.38, 2.38) * mm, "end": v(-3.33, 2.38) * mm});
            skLineSegment(sketch, "E1386", {"start": v(-3.33, 2.38) * mm, "end": v(-4.29, 2.38) * mm});
            skLineSegment(sketch, "E1387", {"start": v(-4.29, 2.38) * mm, "end": v(-4.29, 1.43) * mm});
            skLineSegment(sketch, "E1388", {"start": v(-4.29, 1.43) * mm, "end": v(-3.33, 1.43) * mm});
            skLineSegment(sketch, "E1389", {"start": v(-3.33, 1.43) * mm, "end": v(-2.38, 1.43) * mm});
            skLineSegment(sketch, "E1390", {"start": v(-2.38, 1.43) * mm, "end": v(-1.43, 1.43) * mm});
            skLineSegment(sketch, "E1391", {"start": v(-1.43, 1.43) * mm, "end": v(-1.43, 0.48) * mm});
            skLineSegment(sketch, "E1392", {"start": v(-1.43, 0.48) * mm, "end": v(-1.43, -0.48) * mm});
            skLineSegment(sketch, "E1393", {"start": v(-1.43, -0.48) * mm, "end": v(-2.38, -0.48) * mm});
            skLineSegment(sketch, "E1394", {"start": v(-2.38, -0.48) * mm, "end": v(-2.37, -1.42) * mm});
            skLineSegment(sketch, "E1395", {"start": v(-2.37, -1.42) * mm, "end": v(-1.43, -1.43) * mm});
            skLineSegment(sketch, "E1396", {"start": v(-1.43, -1.43) * mm, "end": v(-0.48, -1.43) * mm});
            skLineSegment(sketch, "E1397", {"start": v(4.29, -0.48) * mm, "end": v(4.29, 0.48) * mm});
            skLineSegment(sketch, "E1398", {"start": v(4.29, 0.48) * mm, "end": v(3.34, 0.47) * mm});
            skLineSegment(sketch, "E1399", {"start": v(3.34, 0.47) * mm, "end": v(3.33, -0.48) * mm});
            skLineSegment(sketch, "E1400", {"start": v(3.33, -0.48) * mm, "end": v(4.29, -0.48) * mm});
            skLineSegment(sketch, "E1401", {"start": v(-3.33, 0.48) * mm, "end": v(-4.29, 0.48) * mm});
            skLineSegment(sketch, "E1402", {"start": v(-4.29, 0.48) * mm, "end": v(-4.29, -0.48) * mm});
            skLineSegment(sketch, "E1403", {"start": v(-4.29, -0.48) * mm, "end": v(-3.33, -0.48) * mm});
            skLineSegment(sketch, "E1404", {"start": v(-3.33, -0.48) * mm, "end": v(-2.4, -0.47) * mm});
            skLineSegment(sketch, "E1405", {"start": v(-2.4, -0.47) * mm, "end": v(-2.38, 0.48) * mm});
            skLineSegment(sketch, "E1406", {"start": v(-2.38, 0.48) * mm, "end": v(-3.33, 0.48) * mm});
            skLineSegment(sketch, "E1407", {"start": v(-5.24, 1.43) * mm, "end": v(-5.24, 2.38) * mm});
            skLineSegment(sketch, "E1408", {"start": v(-5.24, 2.38) * mm, "end": v(-6.2, 2.38) * mm});
            skLineSegment(sketch, "E1409", {"start": v(-6.2, 2.38) * mm, "end": v(-7.14, 2.38) * mm});
            skLineSegment(sketch, "E1410", {"start": v(-7.14, 2.38) * mm, "end": v(-8.1, 2.38) * mm});
            skLineSegment(sketch, "E1411", {"start": v(-8.1, 2.38) * mm, "end": v(-9.05, 2.38) * mm});
            skLineSegment(sketch, "E1412", {"start": v(-9.05, 2.38) * mm, "end": v(-10, 2.38) * mm});
            skLineSegment(sketch, "E1413", {"start": v(-10, 2.38) * mm, "end": v(-10, 1.43) * mm});
            skLineSegment(sketch, "E1414", {"start": v(-10, 1.43) * mm, "end": v(-10, 0.48) * mm});
            skLineSegment(sketch, "E1415", {"start": v(-10, 0.48) * mm, "end": v(-10, -0.48) * mm});
            skLineSegment(sketch, "E1416", {"start": v(-10, -0.48) * mm, "end": v(-10, -1.43) * mm});
            skLineSegment(sketch, "E1417", {"start": v(-10, -1.43) * mm, "end": v(-9.05, -1.43) * mm});
            skLineSegment(sketch, "E1418", {"start": v(-9.05, -1.43) * mm, "end": v(-9.05, -2.38) * mm});
            skLineSegment(sketch, "E1419", {"start": v(-9.05, -2.38) * mm, "end": v(-8.1, -2.38) * mm});
            skLineSegment(sketch, "E1420", {"start": v(-8.1, -2.38) * mm, "end": v(-7.14, -2.38) * mm});
            skLineSegment(sketch, "E1421", {"start": v(-7.14, -2.38) * mm, "end": v(-7.14, -1.43) * mm});
            skLineSegment(sketch, "E1422", {"start": v(-7.14, -1.43) * mm, "end": v(-8.1, -1.43) * mm});
            skLineSegment(sketch, "E1423", {"start": v(-8.1, -1.43) * mm, "end": v(-8.1, -0.48) * mm});
            skLineSegment(sketch, "E1424", {"start": v(-8.1, -0.48) * mm, "end": v(-7.14, -0.48) * mm});
            skLineSegment(sketch, "E1425", {"start": v(-7.14, -0.48) * mm, "end": v(-7.15, 0.47) * mm});
            skLineSegment(sketch, "E1426", {"start": v(-7.15, 0.47) * mm, "end": v(-8.1, 0.48) * mm});
            skLineSegment(sketch, "E1427", {"start": v(-8.1, 0.48) * mm, "end": v(-8.1, 1.43) * mm});
            skLineSegment(sketch, "E1428", {"start": v(-8.1, 1.43) * mm, "end": v(-7.14, 1.43) * mm});
            skLineSegment(sketch, "E1429", {"start": v(-7.14, 1.43) * mm, "end": v(-7.14, 0.48) * mm});
            skLineSegment(sketch, "E1430", {"start": v(-7.14, 0.48) * mm, "end": v(-6.2, 0.48) * mm});
            skLineSegment(sketch, "E1431", {"start": v(-6.2, 0.48) * mm, "end": v(-6.2, -0.48) * mm});
            skLineSegment(sketch, "E1432", {"start": v(-6.2, -0.48) * mm, "end": v(-5.24, -0.48) * mm});
            skLineSegment(sketch, "E1433", {"start": v(-5.24, -0.48) * mm, "end": v(-5.24, 0.48) * mm});
            skLineSegment(sketch, "E1434", {"start": v(-5.24, 0.48) * mm, "end": v(-4.29, 0.49) * mm});
            skLineSegment(sketch, "E1435", {"start": v(-4.29, 0.49) * mm, "end": v(-4.29, 1.42) * mm});
            skLineSegment(sketch, "E1436", {"start": v(-4.29, 1.42) * mm, "end": v(-5.23, 1.43) * mm});
            skLineSegment(sketch, "E1437", {"start": v(-5.23, 1.43) * mm, "end": v(-5.24, 1.43) * mm});
            skLineSegment(sketch, "E1438", {"start": v(9.05, 2.38) * mm, "end": v(8.1, 2.38) * mm});
            skLineSegment(sketch, "E1439", {"start": v(8.1, 2.38) * mm, "end": v(8.1, 1.43) * mm});
            skLineSegment(sketch, "E1440", {"start": v(8.1, 1.43) * mm, "end": v(7.14, 1.43) * mm});
            skLineSegment(sketch, "E1441", {"start": v(7.14, 1.43) * mm, "end": v(7.14, 2.38) * mm});
            skLineSegment(sketch, "E1442", {"start": v(7.14, 2.38) * mm, "end": v(6.2, 2.38) * mm});
            skLineSegment(sketch, "E1443", {"start": v(6.2, 2.38) * mm, "end": v(6.2, 1.43) * mm});
            skLineSegment(sketch, "E1444", {"start": v(6.2, 1.43) * mm, "end": v(5.24, 1.43) * mm});
            skLineSegment(sketch, "E1445", {"start": v(5.24, 1.43) * mm, "end": v(5.24, 0.48) * mm});
            skLineSegment(sketch, "E1446", {"start": v(5.24, 0.48) * mm, "end": v(6.2, 0.48) * mm});
            skLineSegment(sketch, "E1447", {"start": v(6.2, 0.48) * mm, "end": v(7.14, 0.48) * mm});
            skLineSegment(sketch, "E1448", {"start": v(7.14, 0.48) * mm, "end": v(7.14, -0.48) * mm});
            skLineSegment(sketch, "E1449", {"start": v(7.14, -0.48) * mm, "end": v(6.2, -0.48) * mm});
            skLineSegment(sketch, "E1450", {"start": v(6.2, -0.48) * mm, "end": v(5.24, -0.48) * mm});
            skLineSegment(sketch, "E1451", {"start": v(5.24, -0.48) * mm, "end": v(5.24, -1.43) * mm});
            skLineSegment(sketch, "E1452", {"start": v(5.24, -1.43) * mm, "end": v(5.24, -2.38) * mm});
            skLineSegment(sketch, "E1453", {"start": v(5.24, -2.38) * mm, "end": v(4.29, -2.38) * mm});
            skLineSegment(sketch, "E1454", {"start": v(4.29, -2.38) * mm, "end": v(4.29, -1.43) * mm});
            skLineSegment(sketch, "E1455", {"start": v(4.29, -1.43) * mm, "end": v(3.33, -1.43) * mm});
            skLineSegment(sketch, "E1456", {"start": v(3.33, -1.43) * mm, "end": v(3.33, -2.38) * mm});
            skLineSegment(sketch, "E1457", {"start": v(3.33, -2.38) * mm, "end": v(2.38, -2.4) * mm});
            skLineSegment(sketch, "E1458", {"start": v(2.38, -2.4) * mm, "end": v(2.38, -3.32) * mm});
            skLineSegment(sketch, "E1459", {"start": v(2.38, -3.32) * mm, "end": v(3.33, -3.33) * mm});
            skLineSegment(sketch, "E1460", {"start": v(3.33, -3.33) * mm, "end": v(3.34, -4.28) * mm});
            skLineSegment(sketch, "E1461", {"start": v(3.34, -4.28) * mm, "end": v(4.29, -4.29) * mm});
            skLineSegment(sketch, "E1462", {"start": v(4.29, -4.29) * mm, "end": v(5.23, -4.28) * mm});
            skLineSegment(sketch, "E1463", {"start": v(5.23, -4.28) * mm, "end": v(5.24, -3.33) * mm});
            skLineSegment(sketch, "E1464", {"start": v(5.24, -3.33) * mm, "end": v(6.2, -3.33) * mm});
            skLineSegment(sketch, "E1465", {"start": v(6.2, -3.33) * mm, "end": v(7.14, -3.33) * mm});
            skLineSegment(sketch, "E1466", {"start": v(7.14, -3.33) * mm, "end": v(7.14, -4.29) * mm});
            skLineSegment(sketch, "E1467", {"start": v(7.14, -4.29) * mm, "end": v(6.2, -4.29) * mm});
            skLineSegment(sketch, "E1468", {"start": v(6.2, -4.29) * mm, "end": v(5.24, -4.29) * mm});
            skLineSegment(sketch, "E1469", {"start": v(5.24, -4.29) * mm, "end": v(5.24, -5.24) * mm});
            skLineSegment(sketch, "E1470", {"start": v(5.24, -5.24) * mm, "end": v(5.24, -6.2) * mm});
            skLineSegment(sketch, "E1471", {"start": v(5.24, -6.2) * mm, "end": v(4.29, -6.2) * mm});
            skLineSegment(sketch, "E1472", {"start": v(4.29, -6.2) * mm, "end": v(4.29, -5.24) * mm});
            skLineSegment(sketch, "E1473", {"start": v(4.29, -5.24) * mm, "end": v(3.34, -5.25) * mm});
            skLineSegment(sketch, "E1474", {"start": v(3.34, -5.25) * mm, "end": v(3.33, -6.2) * mm});
            skLineSegment(sketch, "E1475", {"start": v(3.33, -6.2) * mm, "end": v(3.33, -7.14) * mm});
            skLineSegment(sketch, "E1476", {"start": v(3.33, -7.14) * mm, "end": v(4.29, -7.14) * mm});
            skLineSegment(sketch, "E1477", {"start": v(4.29, -7.14) * mm, "end": v(4.29, -8.1) * mm});
            skLineSegment(sketch, "E1478", {"start": v(4.29, -8.1) * mm, "end": v(4.29, -9.05) * mm});
            skLineSegment(sketch, "E1479", {"start": v(4.29, -9.05) * mm, "end": v(3.33, -9.05) * mm});
            skLineSegment(sketch, "E1480", {"start": v(3.33, -9.05) * mm, "end": v(3.33, -8.1) * mm});
            skLineSegment(sketch, "E1481", {"start": v(3.33, -8.1) * mm, "end": v(2.38, -8.1) * mm});
            skLineSegment(sketch, "E1482", {"start": v(2.38, -8.1) * mm, "end": v(2.38, -7.14) * mm});
            skLineSegment(sketch, "E1483", {"start": v(2.38, -7.14) * mm, "end": v(1.43, -7.14) * mm});
            skLineSegment(sketch, "E1484", {"start": v(1.43, -7.14) * mm, "end": v(1.43, -8.1) * mm});
            skLineSegment(sketch, "E1485", {"start": v(1.43, -8.1) * mm, "end": v(1.43, -9.05) * mm});
            skLineSegment(sketch, "E1486", {"start": v(1.43, -9.05) * mm, "end": v(0.48, -9.05) * mm});
            skLineSegment(sketch, "E1487", {"start": v(0.48, -9.05) * mm, "end": v(0.48, -10) * mm});
            skLineSegment(sketch, "E1488", {"start": v(0.48, -10) * mm, "end": v(1.43, -10) * mm});
            skLineSegment(sketch, "E1489", {"start": v(1.43, -10) * mm, "end": v(2.38, -10) * mm});
            skLineSegment(sketch, "E1490", {"start": v(2.38, -10) * mm, "end": v(3.33, -10) * mm});
            skLineSegment(sketch, "E1491", {"start": v(3.33, -10) * mm, "end": v(4.29, -10) * mm});
            skLineSegment(sketch, "E1492", {"start": v(4.29, -10) * mm, "end": v(5.24, -10) * mm});
            skLineSegment(sketch, "E1493", {"start": v(5.24, -10) * mm, "end": v(6.2, -10) * mm});
            skLineSegment(sketch, "E1494", {"start": v(6.2, -10) * mm, "end": v(7.14, -10) * mm});
            skLineSegment(sketch, "E1495", {"start": v(7.14, -10) * mm, "end": v(7.13, -9.06) * mm});
            skLineSegment(sketch, "E1496", {"start": v(7.13, -9.06) * mm, "end": v(6.2, -9.05) * mm});
            skLineSegment(sketch, "E1497", {"start": v(6.2, -9.05) * mm, "end": v(6.2, -8.1) * mm});
            skLineSegment(sketch, "E1498", {"start": v(6.2, -8.1) * mm, "end": v(5.24, -8.1) * mm});
            skLineSegment(sketch, "E1499", {"start": v(5.24, -8.1) * mm, "end": v(5.24, -7.14) * mm});
            skLineSegment(sketch, "E1500", {"start": v(5.24, -7.14) * mm, "end": v(6.2, -7.14) * mm});
            skLineSegment(sketch, "E1501", {"start": v(6.2, -7.14) * mm, "end": v(6.2, -6.2) * mm});
            skLineSegment(sketch, "E1502", {"start": v(6.2, -6.2) * mm, "end": v(7.13, -6.18) * mm});
            skLineSegment(sketch, "E1503", {"start": v(7.13, -6.18) * mm, "end": v(7.14, -5.24) * mm});
            skLineSegment(sketch, "E1504", {"start": v(7.14, -5.24) * mm, "end": v(8.1, -5.24) * mm});
            skLineSegment(sketch, "E1505", {"start": v(8.1, -5.24) * mm, "end": v(8.1, -4.29) * mm});
            skLineSegment(sketch, "E1506", {"start": v(8.1, -4.29) * mm, "end": v(9.05, -4.29) * mm});
            skLineSegment(sketch, "E1507", {"start": v(9.05, -4.29) * mm, "end": v(9.04, -3.34) * mm});
            skLineSegment(sketch, "E1508", {"start": v(9.04, -3.34) * mm, "end": v(8.1, -3.33) * mm});
            skLineSegment(sketch, "E1509", {"start": v(8.1, -3.33) * mm, "end": v(8.1, -2.38) * mm});
            skLineSegment(sketch, "E1510", {"start": v(8.1, -2.38) * mm, "end": v(7.14, -2.38) * mm});
            skLineSegment(sketch, "E1511", {"start": v(7.14, -2.38) * mm, "end": v(7.14, -1.43) * mm});
            skLineSegment(sketch, "E1512", {"start": v(7.14, -1.43) * mm, "end": v(8.1, -1.43) * mm});
            skLineSegment(sketch, "E1513", {"start": v(8.1, -1.43) * mm, "end": v(8.1, -0.48) * mm});
            skLineSegment(sketch, "E1514", {"start": v(8.1, -0.48) * mm, "end": v(9.05, -0.48) * mm});
            skLineSegment(sketch, "E1515", {"start": v(9.05, -0.48) * mm, "end": v(9.05, 0.48) * mm});
            skLineSegment(sketch, "E1516", {"start": v(9.05, 0.48) * mm, "end": v(10, 0.48) * mm});
            skLineSegment(sketch, "E1517", {"start": v(10, 0.48) * mm, "end": v(10, 1.43) * mm});
            skLineSegment(sketch, "E1518", {"start": v(10, 1.43) * mm, "end": v(9.05, 1.43) * mm});
            skLineSegment(sketch, "E1519", {"start": v(9.05, 1.43) * mm, "end": v(9.05, 2.38) * mm});
            skLineSegment(sketch, "E1520", {"start": v(4.29, 2.38) * mm, "end": v(4.29, 1.43) * mm});
            skLineSegment(sketch, "E1521", {"start": v(4.29, 1.43) * mm, "end": v(5.23, 1.44) * mm});
            skLineSegment(sketch, "E1522", {"start": v(5.23, 1.44) * mm, "end": v(5.24, 2.38) * mm});
            skLineSegment(sketch, "E1523", {"start": v(5.24, 2.38) * mm, "end": v(4.29, 2.38) * mm});
            skLineSegment(sketch, "E1524", {"start": v(0.48, 3.33) * mm, "end": v(0.48, 4.29) * mm});
            skLineSegment(sketch, "E1525", {"start": v(0.48, 4.29) * mm, "end": v(1.43, 4.29) * mm});
            skLineSegment(sketch, "E1526", {"start": v(1.43, 4.29) * mm, "end": v(1.43, 3.33) * mm});
            skLineSegment(sketch, "E1527", {"start": v(1.43, 3.33) * mm, "end": v(1.43, 2.38) * mm});
            skLineSegment(sketch, "E1528", {"start": v(1.43, 2.38) * mm, "end": v(2.37, 2.4) * mm});
            skLineSegment(sketch, "E1529", {"start": v(2.37, 2.4) * mm, "end": v(2.38, 3.33) * mm});
            skLineSegment(sketch, "E1530", {"start": v(2.38, 3.33) * mm, "end": v(2.38, 4.29) * mm});
            skLineSegment(sketch, "E1531", {"start": v(2.38, 4.29) * mm, "end": v(2.38, 5.24) * mm});
            skLineSegment(sketch, "E1532", {"start": v(2.38, 5.24) * mm, "end": v(1.43, 5.24) * mm});
            skLineSegment(sketch, "E1533", {"start": v(1.43, 5.24) * mm, "end": v(1.43, 6.2) * mm});
            skLineSegment(sketch, "E1534", {"start": v(1.43, 6.2) * mm, "end": v(2.38, 6.2) * mm});
            skLineSegment(sketch, "E1535", {"start": v(2.38, 6.2) * mm, "end": v(2.38, 7.14) * mm});
            skLineSegment(sketch, "E1536", {"start": v(2.38, 7.14) * mm, "end": v(2.38, 8.1) * mm});
            skLineSegment(sketch, "E1537", {"start": v(2.38, 8.1) * mm, "end": v(2.38, 9.05) * mm});
            skLineSegment(sketch, "E1538", {"start": v(2.38, 9.05) * mm, "end": v(1.43, 9.05) * mm});
            skLineSegment(sketch, "E1539", {"start": v(1.43, 9.05) * mm, "end": v(0.48, 9.05) * mm});
            skLineSegment(sketch, "E1540", {"start": v(0.48, 9.05) * mm, "end": v(-0.48, 9.05) * mm});
            skLineSegment(sketch, "E1541", {"start": v(-0.48, 9.05) * mm, "end": v(-0.48, 10) * mm});
            skLineSegment(sketch, "E1542", {"start": v(-0.48, 10) * mm, "end": v(-1.43, 10) * mm});
            skLineSegment(sketch, "E1543", {"start": v(-1.43, 10) * mm, "end": v(-1.43, 9.05) * mm});
            skLineSegment(sketch, "E1544", {"start": v(-1.43, 9.05) * mm, "end": v(-2.38, 9.05) * mm});
            skLineSegment(sketch, "E1545", {"start": v(-2.38, 9.05) * mm, "end": v(-2.38, 8.1) * mm});
            skLineSegment(sketch, "E1546", {"start": v(-2.38, 8.1) * mm, "end": v(-1.43, 8.1) * mm});
            skLineSegment(sketch, "E1547", {"start": v(-1.43, 8.1) * mm, "end": v(-1.43, 7.14) * mm});
            skLineSegment(sketch, "E1548", {"start": v(-1.43, 7.14) * mm, "end": v(-2.38, 7.14) * mm});
            skLineSegment(sketch, "E1549", {"start": v(-2.38, 7.14) * mm, "end": v(-2.38, 6.2) * mm});
            skLineSegment(sketch, "E1550", {"start": v(-2.38, 6.2) * mm, "end": v(-1.43, 6.2) * mm});
            skLineSegment(sketch, "E1551", {"start": v(-1.43, 6.2) * mm, "end": v(-0.49, 6.2) * mm});
            skLineSegment(sketch, "E1552", {"start": v(-0.49, 6.2) * mm, "end": v(-0.48, 7.14) * mm});
            skLineSegment(sketch, "E1553", {"start": v(-0.48, 7.14) * mm, "end": v(-0.48, 8.1) * mm});
            skLineSegment(sketch, "E1554", {"start": v(-0.48, 8.1) * mm, "end": v(0.48, 8.1) * mm});
            skLineSegment(sketch, "E1555", {"start": v(0.48, 8.1) * mm, "end": v(0.48, 7.14) * mm});
            skLineSegment(sketch, "E1556", {"start": v(0.48, 7.14) * mm, "end": v(0.48, 6.2) * mm});
            skLineSegment(sketch, "E1557", {"start": v(0.48, 6.2) * mm, "end": v(-0.48, 6.2) * mm});
            skLineSegment(sketch, "E1558", {"start": v(-0.48, 6.2) * mm, "end": v(-0.48, 5.24) * mm});
            skLineSegment(sketch, "E1559", {"start": v(-0.48, 5.24) * mm, "end": v(-1.43, 5.24) * mm});
            skLineSegment(sketch, "E1560", {"start": v(-1.43, 5.24) * mm, "end": v(-2.38, 5.24) * mm});
            skLineSegment(sketch, "E1561", {"start": v(-2.38, 5.24) * mm, "end": v(-2.38, 4.29) * mm});
            skLineSegment(sketch, "E1562", {"start": v(-2.38, 4.29) * mm, "end": v(-2.38, 3.33) * mm});
            skLineSegment(sketch, "E1563", {"start": v(-2.38, 3.33) * mm, "end": v(-1.43, 3.33) * mm});
            skLineSegment(sketch, "E1564", {"start": v(-1.43, 3.33) * mm, "end": v(-1.43, 4.29) * mm});
            skLineSegment(sketch, "E1565", {"start": v(-1.43, 4.29) * mm, "end": v(-0.48, 4.29) * mm});
            skLineSegment(sketch, "E1566", {"start": v(-0.48, 4.29) * mm, "end": v(-0.48, 3.33) * mm});
            skLineSegment(sketch, "E1567", {"start": v(-0.48, 3.33) * mm, "end": v(-0.47, 2.4) * mm});
            skLineSegment(sketch, "E1568", {"start": v(-0.47, 2.4) * mm, "end": v(0.48, 2.38) * mm});
            skLineSegment(sketch, "E1569", {"start": v(0.48, 2.38) * mm, "end": v(0.48, 3.33) * mm});
            skLineSegment(sketch, "E1570", {"start": v(-8.1, 3.33) * mm, "end": v(-7.14, 3.33) * mm});
            skLineSegment(sketch, "E1571", {"start": v(-7.14, 3.33) * mm, "end": v(-6.2, 3.33) * mm});
            skLineSegment(sketch, "E1572", {"start": v(-6.2, 3.33) * mm, "end": v(-5.24, 3.33) * mm});
            skLineSegment(sketch, "E1573", {"start": v(-5.24, 3.33) * mm, "end": v(-4.29, 3.33) * mm});
            skLineSegment(sketch, "E1574", {"start": v(-4.29, 3.33) * mm, "end": v(-3.33, 3.33) * mm});
            skLineSegment(sketch, "E1575", {"start": v(-3.33, 3.33) * mm, "end": v(-3.33, 4.29) * mm});
            skLineSegment(sketch, "E1576", {"start": v(-3.33, 4.29) * mm, "end": v(-3.33, 5.24) * mm});
            skLineSegment(sketch, "E1577", {"start": v(-3.33, 5.24) * mm, "end": v(-3.33, 6.2) * mm});
            skLineSegment(sketch, "E1578", {"start": v(-3.33, 6.2) * mm, "end": v(-3.33, 7.14) * mm});
            skLineSegment(sketch, "E1579", {"start": v(-3.33, 7.14) * mm, "end": v(-3.33, 8.1) * mm});
            skLineSegment(sketch, "E1580", {"start": v(-3.33, 8.1) * mm, "end": v(-3.33, 9.05) * mm});
            skLineSegment(sketch, "E1581", {"start": v(-3.33, 9.05) * mm, "end": v(-3.33, 10) * mm});
            skLineSegment(sketch, "E1582", {"start": v(-3.33, 10) * mm, "end": v(-4.29, 10) * mm});
            skLineSegment(sketch, "E1583", {"start": v(-4.29, 10) * mm, "end": v(-5.24, 10) * mm});
            skLineSegment(sketch, "E1584", {"start": v(-5.24, 10) * mm, "end": v(-6.2, 10) * mm});
            skLineSegment(sketch, "E1585", {"start": v(-6.2, 10) * mm, "end": v(-7.14, 10) * mm});
            skLineSegment(sketch, "E1586", {"start": v(-7.14, 10) * mm, "end": v(-8.1, 10) * mm});
            skLineSegment(sketch, "E1587", {"start": v(-8.1, 10) * mm, "end": v(-9.05, 10) * mm});
            skLineSegment(sketch, "E1588", {"start": v(-9.05, 10) * mm, "end": v(-10, 10) * mm});
            skLineSegment(sketch, "E1589", {"start": v(-10, 10) * mm, "end": v(-10, 9.05) * mm});
            skLineSegment(sketch, "E1590", {"start": v(-10, 9.05) * mm, "end": v(-10, 8.1) * mm});
            skLineSegment(sketch, "E1591", {"start": v(-10, 8.1) * mm, "end": v(-10, 7.14) * mm});
            skLineSegment(sketch, "E1592", {"start": v(-10, 7.14) * mm, "end": v(-10, 6.2) * mm});
            skLineSegment(sketch, "E1593", {"start": v(-10, 6.2) * mm, "end": v(-10, 5.24) * mm});
            skLineSegment(sketch, "E1594", {"start": v(-10, 5.24) * mm, "end": v(-10, 4.29) * mm});
            skLineSegment(sketch, "E1595", {"start": v(-10, 4.29) * mm, "end": v(-10, 3.33) * mm});
            skLineSegment(sketch, "E1596", {"start": v(-10, 3.33) * mm, "end": v(-9.05, 3.33) * mm});
            skLineSegment(sketch, "E1597", {"start": v(-9.05, 3.33) * mm, "end": v(-8.1, 3.33) * mm});
            skLineSegment(sketch, "E1598", {"start": v(-9.05, 5.24) * mm, "end": v(-9.05, 6.2) * mm});
            skLineSegment(sketch, "E1599", {"start": v(-9.05, 6.2) * mm, "end": v(-9.05, 7.14) * mm});
            skLineSegment(sketch, "E1600", {"start": v(-9.05, 7.14) * mm, "end": v(-9.05, 8.1) * mm});
            skLineSegment(sketch, "E1601", {"start": v(-9.05, 8.1) * mm, "end": v(-9.05, 9.05) * mm});
            skLineSegment(sketch, "E1602", {"start": v(-9.05, 9.05) * mm, "end": v(-8.1, 9.05) * mm});
            skLineSegment(sketch, "E1603", {"start": v(-8.1, 9.05) * mm, "end": v(-7.14, 9.05) * mm});
            skLineSegment(sketch, "E1604", {"start": v(-7.14, 9.05) * mm, "end": v(-6.2, 9.05) * mm});
            skLineSegment(sketch, "E1605", {"start": v(-6.2, 9.05) * mm, "end": v(-5.24, 9.05) * mm});
            skLineSegment(sketch, "E1606", {"start": v(-5.24, 9.05) * mm, "end": v(-4.29, 9.05) * mm});
            skLineSegment(sketch, "E1607", {"start": v(-4.29, 9.05) * mm, "end": v(-4.29, 8.1) * mm});
            skLineSegment(sketch, "E1608", {"start": v(-4.29, 8.1) * mm, "end": v(-4.29, 7.14) * mm});
            skLineSegment(sketch, "E1609", {"start": v(-4.29, 7.14) * mm, "end": v(-4.29, 6.2) * mm});
            skLineSegment(sketch, "E1610", {"start": v(-4.29, 6.2) * mm, "end": v(-4.29, 5.24) * mm});
            skLineSegment(sketch, "E1611", {"start": v(-4.29, 5.24) * mm, "end": v(-4.29, 4.29) * mm});
            skLineSegment(sketch, "E1612", {"start": v(-4.29, 4.29) * mm, "end": v(-5.24, 4.29) * mm});
            skLineSegment(sketch, "E1613", {"start": v(-5.24, 4.29) * mm, "end": v(-6.2, 4.29) * mm});
            skLineSegment(sketch, "E1614", {"start": v(-6.2, 4.29) * mm, "end": v(-7.14, 4.29) * mm});
            skLineSegment(sketch, "E1615", {"start": v(-7.14, 4.29) * mm, "end": v(-8.1, 4.29) * mm});
            skLineSegment(sketch, "E1616", {"start": v(-8.1, 4.29) * mm, "end": v(-9.05, 4.29) * mm});
            skLineSegment(sketch, "E1617", {"start": v(-9.05, 4.29) * mm, "end": v(-9.05, 5.24) * mm});
            skLineSegment(sketch, "E1618", {"start": v(-6.2, 5.24) * mm, "end": v(-5.24, 5.24) * mm});
            skLineSegment(sketch, "E1619", {"start": v(-5.24, 5.24) * mm, "end": v(-5.24, 6.2) * mm});
            skLineSegment(sketch, "E1620", {"start": v(-5.24, 6.2) * mm, "end": v(-5.24, 7.14) * mm});
            skLineSegment(sketch, "E1621", {"start": v(-5.24, 7.14) * mm, "end": v(-5.24, 8.1) * mm});
            skLineSegment(sketch, "E1622", {"start": v(-5.24, 8.1) * mm, "end": v(-6.2, 8.1) * mm});
            skLineSegment(sketch, "E1623", {"start": v(-6.2, 8.1) * mm, "end": v(-7.14, 8.1) * mm});
            skLineSegment(sketch, "E1624", {"start": v(-7.14, 8.1) * mm, "end": v(-8.1, 8.1) * mm});
            skLineSegment(sketch, "E1625", {"start": v(-8.1, 8.1) * mm, "end": v(-8.1, 7.14) * mm});
            skLineSegment(sketch, "E1626", {"start": v(-8.1, 7.14) * mm, "end": v(-8.1, 6.2) * mm});
            skLineSegment(sketch, "E1627", {"start": v(-8.1, 6.2) * mm, "end": v(-8.1, 5.24) * mm});
            skLineSegment(sketch, "E1628", {"start": v(-8.1, 5.24) * mm, "end": v(-7.14, 5.24) * mm});
            skLineSegment(sketch, "E1629", {"start": v(-7.14, 5.24) * mm, "end": v(-6.2, 5.24) * mm});
            skLineSegment(sketch, "E1630", {"start": v(6.2, 8.1) * mm, "end": v(5.24, 8.1) * mm});
            skLineSegment(sketch, "E1631", {"start": v(5.24, 8.1) * mm, "end": v(5.24, 7.14) * mm});
            skLineSegment(sketch, "E1632", {"start": v(5.24, 7.14) * mm, "end": v(5.24, 6.2) * mm});
            skLineSegment(sketch, "E1633", {"start": v(5.24, 6.2) * mm, "end": v(5.24, 5.24) * mm});
            skLineSegment(sketch, "E1634", {"start": v(5.24, 5.24) * mm, "end": v(6.2, 5.24) * mm});
            skLineSegment(sketch, "E1635", {"start": v(6.2, 5.24) * mm, "end": v(7.14, 5.24) * mm});
            skLineSegment(sketch, "E1636", {"start": v(7.14, 5.24) * mm, "end": v(8.1, 5.24) * mm});
            skLineSegment(sketch, "E1637", {"start": v(8.1, 5.24) * mm, "end": v(8.1, 6.2) * mm});
            skLineSegment(sketch, "E1638", {"start": v(8.1, 6.2) * mm, "end": v(8.1, 7.14) * mm});
            skLineSegment(sketch, "E1639", {"start": v(8.1, 7.14) * mm, "end": v(8.1, 8.1) * mm});
            skLineSegment(sketch, "E1640", {"start": v(8.1, 8.1) * mm, "end": v(7.14, 8.1) * mm});
            skLineSegment(sketch, "E1641", {"start": v(7.14, 8.1) * mm, "end": v(6.2, 8.1) * mm});
            skLineSegment(sketch, "E1642", {"start": v(9.05, 10) * mm, "end": v(8.1, 10) * mm});
            skLineSegment(sketch, "E1643", {"start": v(8.1, 10) * mm, "end": v(7.14, 10) * mm});
            skLineSegment(sketch, "E1644", {"start": v(7.14, 10) * mm, "end": v(6.2, 10) * mm});
            skLineSegment(sketch, "E1645", {"start": v(6.2, 10) * mm, "end": v(5.24, 10) * mm});
            skLineSegment(sketch, "E1646", {"start": v(5.24, 10) * mm, "end": v(4.29, 10) * mm});
            skLineSegment(sketch, "E1647", {"start": v(4.29, 10) * mm, "end": v(3.33, 10) * mm});
            skLineSegment(sketch, "E1648", {"start": v(3.33, 10) * mm, "end": v(3.33, 9.05) * mm});
            skLineSegment(sketch, "E1649", {"start": v(3.33, 9.05) * mm, "end": v(3.33, 8.1) * mm});
            skLineSegment(sketch, "E1650", {"start": v(3.33, 8.1) * mm, "end": v(3.33, 7.14) * mm});
            skLineSegment(sketch, "E1651", {"start": v(3.33, 7.14) * mm, "end": v(3.33, 6.2) * mm});
            skLineSegment(sketch, "E1652", {"start": v(3.33, 6.2) * mm, "end": v(3.33, 5.24) * mm});
            skLineSegment(sketch, "E1653", {"start": v(3.33, 5.24) * mm, "end": v(3.33, 4.29) * mm});
            skLineSegment(sketch, "E1654", {"start": v(3.33, 4.29) * mm, "end": v(3.33, 3.33) * mm});
            skLineSegment(sketch, "E1655", {"start": v(3.33, 3.33) * mm, "end": v(4.29, 3.33) * mm});
            skLineSegment(sketch, "E1656", {"start": v(4.29, 3.33) * mm, "end": v(5.24, 3.33) * mm});
            skLineSegment(sketch, "E1657", {"start": v(5.24, 3.33) * mm, "end": v(6.2, 3.33) * mm});
            skLineSegment(sketch, "E1658", {"start": v(6.2, 3.33) * mm, "end": v(7.14, 3.33) * mm});
            skLineSegment(sketch, "E1659", {"start": v(7.14, 3.33) * mm, "end": v(8.1, 3.33) * mm});
            skLineSegment(sketch, "E1660", {"start": v(8.1, 3.33) * mm, "end": v(9.05, 3.33) * mm});
            skLineSegment(sketch, "E1661", {"start": v(9.05, 3.33) * mm, "end": v(10, 3.33) * mm});
            skLineSegment(sketch, "E1662", {"start": v(10, 3.33) * mm, "end": v(10, 4.29) * mm});
            skLineSegment(sketch, "E1663", {"start": v(10, 4.29) * mm, "end": v(10, 5.24) * mm});
            skLineSegment(sketch, "E1664", {"start": v(10, 5.24) * mm, "end": v(10, 6.2) * mm});
            skLineSegment(sketch, "E1665", {"start": v(10, 6.2) * mm, "end": v(10, 7.14) * mm});
            skLineSegment(sketch, "E1666", {"start": v(10, 7.14) * mm, "end": v(10, 8.1) * mm});
            skLineSegment(sketch, "E1667", {"start": v(10, 8.1) * mm, "end": v(10, 9.05) * mm});
            skLineSegment(sketch, "E1668", {"start": v(10, 9.05) * mm, "end": v(10, 10) * mm});
            skLineSegment(sketch, "E1669", {"start": v(10, 10) * mm, "end": v(9.05, 10) * mm});
            skLineSegment(sketch, "E1670", {"start": v(9.05, 8.1) * mm, "end": v(9.05, 7.14) * mm});
            skLineSegment(sketch, "E1671", {"start": v(9.05, 7.14) * mm, "end": v(9.05, 6.2) * mm});
            skLineSegment(sketch, "E1672", {"start": v(9.05, 6.2) * mm, "end": v(9.05, 5.24) * mm});
            skLineSegment(sketch, "E1673", {"start": v(9.05, 5.24) * mm, "end": v(9.05, 4.29) * mm});
            skLineSegment(sketch, "E1674", {"start": v(9.05, 4.29) * mm, "end": v(8.1, 4.29) * mm});
            skLineSegment(sketch, "E1675", {"start": v(8.1, 4.29) * mm, "end": v(7.14, 4.29) * mm});
            skLineSegment(sketch, "E1676", {"start": v(7.14, 4.29) * mm, "end": v(6.2, 4.29) * mm});
            skLineSegment(sketch, "E1677", {"start": v(6.2, 4.29) * mm, "end": v(5.24, 4.29) * mm});
            skLineSegment(sketch, "E1678", {"start": v(5.24, 4.29) * mm, "end": v(4.29, 4.29) * mm});
            skLineSegment(sketch, "E1679", {"start": v(4.29, 4.29) * mm, "end": v(4.29, 5.24) * mm});
            skLineSegment(sketch, "E1680", {"start": v(4.29, 5.24) * mm, "end": v(4.29, 6.2) * mm});
            skLineSegment(sketch, "E1681", {"start": v(4.29, 6.2) * mm, "end": v(4.29, 7.14) * mm});
            skLineSegment(sketch, "E1682", {"start": v(4.29, 7.14) * mm, "end": v(4.29, 8.1) * mm});
            skLineSegment(sketch, "E1683", {"start": v(4.29, 8.1) * mm, "end": v(4.29, 9.05) * mm});
            skLineSegment(sketch, "E1684", {"start": v(4.29, 9.05) * mm, "end": v(5.24, 9.05) * mm});
            skLineSegment(sketch, "E1685", {"start": v(5.24, 9.05) * mm, "end": v(6.2, 9.05) * mm});
            skLineSegment(sketch, "E1686", {"start": v(6.2, 9.05) * mm, "end": v(7.14, 9.05) * mm});
            skLineSegment(sketch, "E1687", {"start": v(7.14, 9.05) * mm, "end": v(8.1, 9.05) * mm});
            skLineSegment(sketch, "E1688", {"start": v(8.1, 9.05) * mm, "end": v(9.05, 9.05) * mm});
            skLineSegment(sketch, "E1689", {"start": v(9.05, 9.05) * mm, "end": v(9.05, 8.1) * mm});
            skSolve(sketch);
        }
        {
            var Q0;
            Q0=qSketchRegion(id+"F10",true);
            var Q1;
            Q1=makeQuery(id+"F10.imprint","IMPRINT",FACE,{"disambiguationData":[TD([[makeQuery(id+"F10.imprint","IMPRINT",EDGE,{"derivedFrom":sQuery(id+"F10.wireOp",EDGE,"E1618")}),1.0]])]});
            var Q2;
            Q2=makeQuery(id+"F10.imprint","IMPRINT",FACE,{"disambiguationData":[TD([[makeQuery(id+"F10.imprint","IMPRINT",EDGE,{"derivedFrom":sQuery(id+"F10.wireOp",EDGE,"E1630")}),1.0]])]});
            var Q3;
            Q3=makeQuery(id+"F10.imprint","IMPRINT",FACE,{"disambiguationData":[TD([[makeQuery(id+"F10.imprint","IMPRINT",EDGE,{"derivedFrom":sQuery(id+"F10.wireOp",EDGE,"E1259")}),1.0]])]});
            extrude(context, id + "F11", {"entities" : qUnion([Q0, Q1, Q2, Q3]), "operationType" : NewBodyOperationType.REMOVE, "oppositeDirection" : true, "depth" : 1 * mm, "offsetDistance" : 25 * mm});
        }
    });
